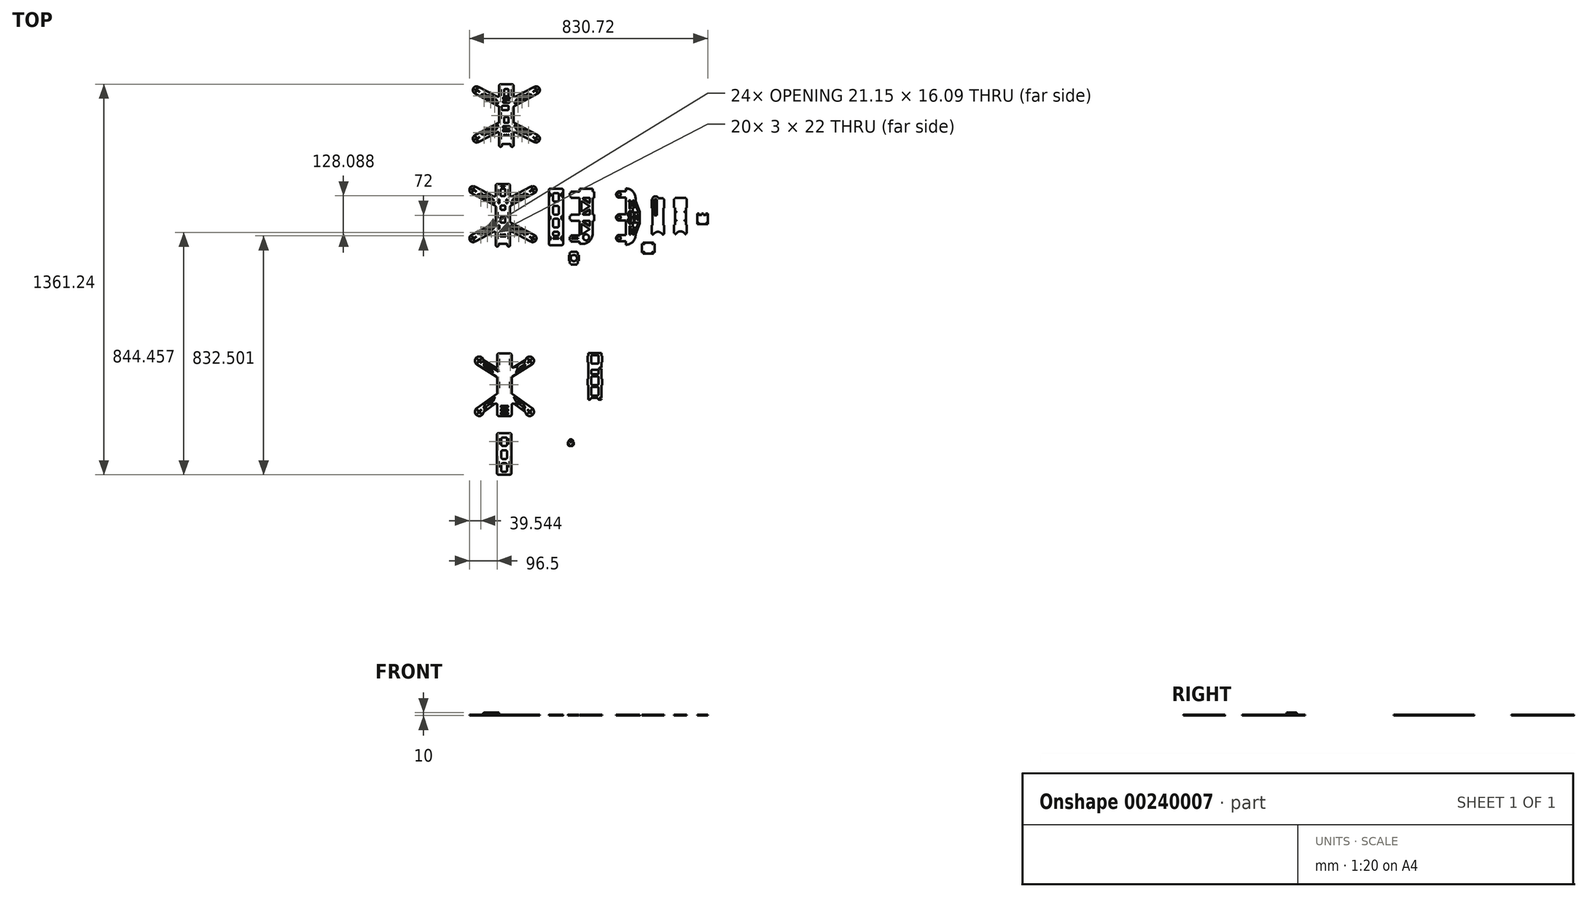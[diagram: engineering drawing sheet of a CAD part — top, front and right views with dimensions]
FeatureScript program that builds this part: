
annotation { "Feature Type Name" : "Feature", "Feature Type Description" : "" }
export const myFeature = defineFeature(function(context is Context, id is Id, definition is map)
    precondition{}
    {
        {
            var Q0;
            Q0=qCreatedBy(makeId("Top.planeOp"),FACE);
            var sketch = newSketch(context, id + "F0", { "sketchPlane" : qUnion([Q0])});
            skLineSegment(sketch, "E0", {"start": v(68.26, -102.02) * mm, "end": v(64.85, -102.02) * mm});
            skCircle(sketch, "E1", {"center": v(68.26, 75.53) * mm, "radius": 3.4 * mm});
            skCircle(sketch, "E2", {"center": v(62.63, 69.85) * mm, "radius": 1.3 * mm});
            skCircle(sketch, "E3", {"center": v(73.9, 81.2) * mm, "radius": 1.3 * mm});
            skCircle(sketch, "E4", {"center": v(61.51, 82.22) * mm, "radius": 1.3 * mm});
            skCircle(sketch, "E5", {"center": v(75, 68.84) * mm, "radius": 1.3 * mm});
            skCircle(sketch, "E6.MirrorC", {"center": v(-101, 82.22) * mm, "radius": 1.3 * mm});
            skCircle(sketch, "E7.MirrorC", {"center": v(-113.37, 81.2) * mm, "radius": 1.3 * mm});
            skCircle(sketch, "E8.MirrorC", {"center": v(-102.1, 69.85) * mm, "radius": 1.3 * mm});
            skCircle(sketch, "E9.MirrorC", {"center": v(-114.49, 68.84) * mm, "radius": 1.3 * mm});
            skCircle(sketch, "E10.MirrorC", {"center": v(-107.74, 75.53) * mm, "radius": 3.4 * mm});
            skArc(sketch, "E11", {"start": v(-93.48, 80.2) * mm, "mid": v(-116.97, 87.35) * mm, "end": v(-115.73, 62.83) * mm});
            skArc(sketch, "E12.MirrorC", {"start": v(-93.03, -104.95) * mm, "mid": v(-117.1, -113.75) * mm, "end": v(-113.86, -88.33) * mm});
            skCircle(sketch, "E13.MirrorC", {"center": v(-107.74, -102.02) * mm, "radius": 3.4 * mm});
            skCircle(sketch, "E14.MirrorC", {"center": v(-102.1, -96.34) * mm, "radius": 1.3 * mm});
            skCircle(sketch, "E15.MirrorC", {"center": v(-101, -108.7) * mm, "radius": 1.3 * mm});
            skCircle(sketch, "E16.MirrorC", {"center": v(-113.37, -107.7) * mm, "radius": 1.3 * mm});
            skCircle(sketch, "E17.MirrorC", {"center": v(-114.49, -95.33) * mm, "radius": 1.3 * mm});
            skLineSegment(sketch, "E18", {"start": v(-19.74, 100.98) * mm, "end": v(-44.74, 100.98) * mm});
            skLineSegment(sketch, "E19.bottom", {"start": v(-39.74, 100.98) * mm, "end": v(0.26, 100.98) * mm});
            skLineSegment(sketch, "E19.top", {"start": v(-39.74, -117.02) * mm, "end": v(0.26, -117.02) * mm});
            skLineSegment(sketch, "E19.left", {"start": v(-44.74, 95.98) * mm, "end": v(-44.74, 57.2) * mm});
            skLineSegment(sketch, "E19.right", {"start": v(5.26, 95.98) * mm, "end": v(5.26, 57.2) * mm});
            skArc(sketch, "E20.MirrorC", {"start": v(53.55, -104.95) * mm, "mid": v(77.62, -113.75) * mm, "end": v(74.38, -88.33) * mm});
            skCircle(sketch, "E21.MirrorC", {"center": v(62.63, -96.34) * mm, "radius": 1.3 * mm});
            skCircle(sketch, "E22.MirrorC", {"center": v(75, -95.33) * mm, "radius": 1.3 * mm});
            skCircle(sketch, "E23.MirrorC", {"center": v(73.9, -107.7) * mm, "radius": 1.3 * mm});
            skCircle(sketch, "E24.MirrorC", {"center": v(61.51, -108.7) * mm, "radius": 1.3 * mm});
            skArc(sketch, "E25.MirrorC", {"start": v(54, 80.2) * mm, "mid": v(77.49, 87.35) * mm, "end": v(76.25, 62.83) * mm});
            skCircle(sketch, "E26.MirrorC", {"center": v(68.26, -102.02) * mm, "radius": 3.4 * mm});
            skLineSegment(sketch, "E27", {"start": v(-52.67, -74.18) * mm, "end": v(-91.05, -101.87) * mm});
            skLineSegment(sketch, "E28", {"start": v(-46.81, -39.96) * mm, "end": v(-113.86, -88.33) * mm});
            skLineSegment(sketch, "E29", {"start": v(-47.08, 19.62) * mm, "end": v(-115.73, 62.83) * mm});
            skLineSegment(sketch, "E30", {"start": v(-52.4, 52.98) * mm, "end": v(-91.4, 77.52) * mm});
            skLineSegment(sketch, "E31.MirrorCS", {"start": v(13.19, -74.18) * mm, "end": v(51.57, -101.87) * mm});
            skLineSegment(sketch, "E32.MirrorCS", {"start": v(7.33, -39.96) * mm, "end": v(74.38, -88.33) * mm});
            skLineSegment(sketch, "E33.MirrorCS", {"start": v(7.6, 19.62) * mm, "end": v(76.25, 62.83) * mm});
            skLineSegment(sketch, "E34.MirrorCS", {"start": v(12.92, 52.98) * mm, "end": v(51.92, 77.52) * mm});
            skLineSegment(sketch, "E35.trimOffspring", {"start": v(-44.74, -78.24) * mm, "end": v(-44.74, -112.02) * mm});
            skLineSegment(sketch, "E36.trimOffspring", {"start": v(5.26, -78.24) * mm, "end": v(5.26, -112.02) * mm});
            skLineSegment(sketch, "E37.trimOffspring", {"start": v(5.26, 15.4) * mm, "end": v(5.26, -35.9) * mm});
            skLineSegment(sketch, "E38.trimOffspring", {"start": v(-44.74, 15.4) * mm, "end": v(-44.74, -35.9) * mm});
            skLineSegment(sketch, "E39.trimOffspring", {"start": v(68.26, -98.62) * mm, "end": v(68.26, -102.02) * mm});
            skPoint(sketch, "E40.visualSharp", {"position": v(-44.74, 100.98) * mm});
            skArc(sketch, "E40.filletArc", {"start": v(-39.74, 100.98) * mm, "mid": v(-43.28, 99.51) * mm, "end": v(-44.74, 95.98) * mm});
            skPoint(sketch, "E41.visualSharp", {"position": v(5.26, 100.98) * mm});
            skArc(sketch, "E41.filletArc", {"start": v(5.26, 95.98) * mm, "mid": v(3.8, 99.51) * mm, "end": v(0.26, 100.98) * mm});
            skPoint(sketch, "E42.visualSharp", {"position": v(5.26, -117.02) * mm});
            skArc(sketch, "E42.filletArc", {"start": v(0.26, -117.02) * mm, "mid": v(3.8, -115.56) * mm, "end": v(5.26, -112.02) * mm});
            skPoint(sketch, "E43.visualSharp", {"position": v(-44.74, -117.02) * mm});
            skArc(sketch, "E43.filletArc", {"start": v(-44.74, -112.02) * mm, "mid": v(-43.28, -115.56) * mm, "end": v(-39.74, -117.02) * mm});
            skPoint(sketch, "E44.visualSharp", {"position": v(5.26, 18.15) * mm});
            skArc(sketch, "E44.filletArc", {"start": v(7.6, 19.62) * mm, "mid": v(5.88, 17.8) * mm, "end": v(5.26, 15.4) * mm});
            skPoint(sketch, "E45.visualSharp", {"position": v(-44.74, 18.15) * mm});
            skArc(sketch, "E45.filletArc", {"start": v(-44.74, 15.4) * mm, "mid": v(-45.36, 17.8) * mm, "end": v(-47.08, 19.62) * mm});
            skPoint(sketch, "E46.visualSharp", {"position": v(-44.74, -38.47) * mm});
            skArc(sketch, "E46.filletArc", {"start": v(-46.81, -39.96) * mm, "mid": v(-45.29, -38.19) * mm, "end": v(-44.74, -35.9) * mm});
            skPoint(sketch, "E47.visualSharp", {"position": v(5.26, -38.47) * mm});
            skArc(sketch, "E47.filletArc", {"start": v(5.26, -35.9) * mm, "mid": v(5.8, -38.19) * mm, "end": v(7.33, -39.96) * mm});
            skPoint(sketch, "E48.visualSharp", {"position": v(5.26, -68.47) * mm});
            skArc(sketch, "E48.filletArc", {"start": v(13.19, -74.18) * mm, "mid": v(7.98, -73.79) * mm, "end": v(5.26, -78.24) * mm});
            skPoint(sketch, "E49.visualSharp", {"position": v(-44.74, -68.47) * mm});
            skArc(sketch, "E49.filletArc", {"start": v(-44.74, -78.24) * mm, "mid": v(-47.46, -73.79) * mm, "end": v(-52.67, -74.18) * mm});
            skPoint(sketch, "E50.visualSharp", {"position": v(-44.74, 48.15) * mm});
            skArc(sketch, "E50.filletArc", {"start": v(-52.4, 52.98) * mm, "mid": v(-47.32, 52.83) * mm, "end": v(-44.74, 57.2) * mm});
            skPoint(sketch, "E51.visualSharp", {"position": v(5.26, 48.15) * mm});
            skArc(sketch, "E51.filletArc", {"start": v(5.26, 57.2) * mm, "mid": v(7.84, 52.83) * mm, "end": v(12.92, 52.98) * mm});
            skPoint(sketch, "E52.visualSharp", {"position": v(-93.05, 78.56) * mm});
            skArc(sketch, "E52.filletArc", {"start": v(-93.48, 80.2) * mm, "mid": v(-92.67, 78.67) * mm, "end": v(-91.4, 77.52) * mm});
            skPoint(sketch, "E53.visualSharp", {"position": v(53.57, 78.56) * mm});
            skArc(sketch, "E53.filletArc", {"start": v(51.92, 77.52) * mm, "mid": v(53.2, 78.67) * mm, "end": v(54, 80.2) * mm});
            skPoint(sketch, "E54.visualSharp", {"position": v(53.3, -103.12) * mm});
            skArc(sketch, "E54.filletArc", {"start": v(53.55, -104.95) * mm, "mid": v(52.85, -103.22) * mm, "end": v(51.57, -101.87) * mm});
            skPoint(sketch, "E55.visualSharp", {"position": v(-92.78, -103.12) * mm});
            skArc(sketch, "E55.filletArc", {"start": v(-91.05, -101.87) * mm, "mid": v(-92.33, -103.22) * mm, "end": v(-93.03, -104.95) * mm});
            skLineSegment(sketch, "E56", {"start": v(-19.74, 100.98) * mm, "end": v(-19.74, -117.02) * mm, "construction": true});
            skLineSegment(sketch, "E57", {"start": v(-41.74, 82.98) * mm, "end": v(-41.74, 60.98) * mm});
            skLineSegment(sketch, "E58", {"start": v(-41.74, 60.98) * mm, "end": v(-38.74, 60.98) * mm});
            skLineSegment(sketch, "E59", {"start": v(-38.74, 60.98) * mm, "end": v(-38.74, 82.98) * mm});
            skLineSegment(sketch, "E60", {"start": v(-38.74, 82.98) * mm, "end": v(-41.74, 82.98) * mm});
            skLineSegment(sketch, "E61", {"start": v(-41.74, 2.98) * mm, "end": v(-41.74, -19.02) * mm});
            skLineSegment(sketch, "E62", {"start": v(-41.74, -19.02) * mm, "end": v(-38.74, -19.02) * mm});
            skLineSegment(sketch, "E63", {"start": v(-38.74, -19.02) * mm, "end": v(-38.74, 2.98) * mm});
            skLineSegment(sketch, "E64", {"start": v(-38.74, 2.98) * mm, "end": v(-41.74, 2.98) * mm});
            skLineSegment(sketch, "E65.MirrorCS", {"start": v(-0.74, 60.98) * mm, "end": v(-0.74, 82.98) * mm});
            skLineSegment(sketch, "E66.MirrorCS", {"start": v(2.26, 60.98) * mm, "end": v(-0.74, 60.98) * mm});
            skLineSegment(sketch, "E67.MirrorCS", {"start": v(2.26, 82.98) * mm, "end": v(2.26, 60.98) * mm});
            skLineSegment(sketch, "E68.MirrorCS", {"start": v(-0.74, 82.98) * mm, "end": v(2.26, 82.98) * mm});
            skLineSegment(sketch, "E69.MirrorCS", {"start": v(-0.74, 2.98) * mm, "end": v(2.26, 2.98) * mm});
            skLineSegment(sketch, "E70.MirrorCS", {"start": v(2.26, 2.98) * mm, "end": v(2.26, -19.02) * mm});
            skLineSegment(sketch, "E71.MirrorCS", {"start": v(-0.74, -19.02) * mm, "end": v(-0.74, 2.98) * mm});
            skLineSegment(sketch, "E72.MirrorCS", {"start": v(2.26, -19.02) * mm, "end": v(-0.74, -19.02) * mm});
            skLineSegment(sketch, "E73.bottom", {"start": v(-9.74, -80.94) * mm, "end": v(-29.74, -80.94) * mm});
            skLineSegment(sketch, "E73.top", {"start": v(-9.74, -86.94) * mm, "end": v(-29.74, -86.94) * mm});
            skLineSegment(sketch, "E73.left", {"start": v(-6.74, -83.94) * mm, "end": v(-6.74, -83.94) * mm});
            skLineSegment(sketch, "E73.right", {"start": v(-32.74, -83.94) * mm, "end": v(-32.74, -83.94) * mm});
            skPoint(sketch, "E74.visualSharp", {"position": v(-32.74, -80.94) * mm});
            skArc(sketch, "E74.filletArc", {"start": v(-29.74, -80.94) * mm, "mid": v(-31.86, -81.81) * mm, "end": v(-32.74, -83.94) * mm});
            skPoint(sketch, "E75.visualSharp", {"position": v(-32.74, -86.94) * mm});
            skArc(sketch, "E75.filletArc", {"start": v(-32.74, -83.94) * mm, "mid": v(-31.86, -86.06) * mm, "end": v(-29.74, -86.94) * mm});
            skPoint(sketch, "E76.visualSharp", {"position": v(-6.74, -80.94) * mm});
            skArc(sketch, "E76.filletArc", {"start": v(-6.74, -83.94) * mm, "mid": v(-7.62, -81.81) * mm, "end": v(-9.74, -80.94) * mm});
            skPoint(sketch, "E77.visualSharp", {"position": v(-6.74, -86.94) * mm});
            skArc(sketch, "E77.filletArc", {"start": v(-9.74, -86.94) * mm, "mid": v(-7.62, -86.06) * mm, "end": v(-6.74, -83.94) * mm});
            skLineSegment(sketch, "E78.bottom", {"start": v(-9.74, -92.94) * mm, "end": v(-29.74, -92.94) * mm});
            skLineSegment(sketch, "E78.top", {"start": v(-9.74, -98.94) * mm, "end": v(-29.74, -98.94) * mm});
            skLineSegment(sketch, "E78.left", {"start": v(-6.74, -95.94) * mm, "end": v(-6.74, -95.94) * mm});
            skLineSegment(sketch, "E78.right", {"start": v(-32.74, -95.94) * mm, "end": v(-32.74, -95.94) * mm});
            skPoint(sketch, "E79.visualSharp", {"position": v(-32.74, -92.94) * mm});
            skArc(sketch, "E79.filletArc", {"start": v(-29.74, -92.94) * mm, "mid": v(-31.86, -93.81) * mm, "end": v(-32.74, -95.94) * mm});
            skPoint(sketch, "E80.visualSharp", {"position": v(-32.74, -98.94) * mm});
            skArc(sketch, "E80.filletArc", {"start": v(-32.74, -95.94) * mm, "mid": v(-31.86, -98.06) * mm, "end": v(-29.74, -98.94) * mm});
            skPoint(sketch, "E81.visualSharp", {"position": v(-6.74, -92.94) * mm});
            skArc(sketch, "E81.filletArc", {"start": v(-6.74, -95.94) * mm, "mid": v(-7.62, -93.81) * mm, "end": v(-9.74, -92.94) * mm});
            skPoint(sketch, "E82.visualSharp", {"position": v(-6.74, -98.94) * mm});
            skArc(sketch, "E82.filletArc", {"start": v(-9.74, -98.94) * mm, "mid": v(-7.62, -98.06) * mm, "end": v(-6.74, -95.94) * mm});
            skLineSegment(sketch, "E83.bottom", {"start": v(-9.74, -104.94) * mm, "end": v(-29.74, -104.94) * mm});
            skLineSegment(sketch, "E83.top", {"start": v(-9.74, -110.94) * mm, "end": v(-29.74, -110.94) * mm});
            skLineSegment(sketch, "E83.left", {"start": v(-6.74, -107.94) * mm, "end": v(-6.74, -107.94) * mm});
            skLineSegment(sketch, "E83.right", {"start": v(-32.74, -107.94) * mm, "end": v(-32.74, -107.94) * mm});
            skPoint(sketch, "E84.visualSharp", {"position": v(-32.74, -104.94) * mm});
            skArc(sketch, "E84.filletArc", {"start": v(-29.74, -104.94) * mm, "mid": v(-31.86, -105.81) * mm, "end": v(-32.74, -107.94) * mm});
            skPoint(sketch, "E85.visualSharp", {"position": v(-32.74, -110.94) * mm});
            skArc(sketch, "E85.filletArc", {"start": v(-32.74, -107.94) * mm, "mid": v(-31.86, -110.06) * mm, "end": v(-29.74, -110.94) * mm});
            skPoint(sketch, "E86.visualSharp", {"position": v(-6.74, -104.94) * mm});
            skArc(sketch, "E86.filletArc", {"start": v(-6.74, -107.94) * mm, "mid": v(-7.62, -105.81) * mm, "end": v(-9.74, -104.94) * mm});
            skPoint(sketch, "E87.visualSharp", {"position": v(-6.74, -110.94) * mm});
            skArc(sketch, "E87.filletArc", {"start": v(-9.74, -110.94) * mm, "mid": v(-7.62, -110.06) * mm, "end": v(-6.74, -107.94) * mm});
            skLineSegment(sketch, "E88", {"start": v(-54.79, -50.65) * mm, "end": v(-75.87, -65.86) * mm});
            skLineSegment(sketch, "E89", {"start": v(-75.2, -67.67) * mm, "end": v(-61.28, -66.51) * mm});
            skLineSegment(sketch, "E90", {"start": v(-53.28, -51.85) * mm, "end": v(-58.77, -64.7) * mm});
            skPoint(sketch, "E91.visualSharp", {"position": v(-78.8, -67.96) * mm});
            skArc(sketch, "E91.filletArc", {"start": v(-75.87, -65.86) * mm, "mid": v(-76.23, -67.02) * mm, "end": v(-75.2, -67.67) * mm});
            skPoint(sketch, "E92.visualSharp", {"position": v(-51.87, -48.54) * mm});
            skArc(sketch, "E92.filletArc", {"start": v(-53.28, -51.85) * mm, "mid": v(-53.58, -50.68) * mm, "end": v(-54.79, -50.65) * mm});
            skPoint(sketch, "E93.visualSharp", {"position": v(-59.48, -66.36) * mm});
            skArc(sketch, "E93.filletArc", {"start": v(-61.28, -66.51) * mm, "mid": v(-59.78, -65.96) * mm, "end": v(-58.77, -64.7) * mm});
            skLineSegment(sketch, "E94", {"start": v(-69.16, -73.35) * mm, "end": v(-90.25, -88.56) * mm});
            skLineSegment(sketch, "E95", {"start": v(-91.75, -87.35) * mm, "end": v(-86.26, -74.5) * mm});
            skLineSegment(sketch, "E96", {"start": v(-83.75, -72.7) * mm, "end": v(-69.83, -71.54) * mm});
            skPoint(sketch, "E97.visualSharp", {"position": v(-93.17, -90.66) * mm});
            skArc(sketch, "E97.filletArc", {"start": v(-91.75, -87.35) * mm, "mid": v(-91.46, -88.53) * mm, "end": v(-90.25, -88.56) * mm});
            skPoint(sketch, "E98.visualSharp", {"position": v(-66.24, -71.24) * mm});
            skArc(sketch, "E98.filletArc", {"start": v(-69.16, -73.35) * mm, "mid": v(-68.8, -72.19) * mm, "end": v(-69.83, -71.54) * mm});
            skPoint(sketch, "E99.visualSharp", {"position": v(-85.56, -72.84) * mm});
            skArc(sketch, "E99.filletArc", {"start": v(-83.75, -72.7) * mm, "mid": v(-85.26, -73.25) * mm, "end": v(-86.26, -74.5) * mm});
            skLineSegment(sketch, "E100.MirrorCS", {"start": v(35.73, -67.67) * mm, "end": v(21.8, -66.51) * mm});
            skLineSegment(sketch, "E101.MirrorCS", {"start": v(29.68, -73.35) * mm, "end": v(50.77, -88.56) * mm});
            skLineSegment(sketch, "E102.MirrorCS", {"start": v(44.27, -72.7) * mm, "end": v(30.35, -71.54) * mm});
            skArc(sketch, "E103.MirrorCS", {"start": v(44.27, -72.7) * mm, "mid": v(45.78, -73.25) * mm, "end": v(46.78, -74.5) * mm});
            skLineSegment(sketch, "E104.MirrorCS", {"start": v(52.27, -87.35) * mm, "end": v(46.78, -74.5) * mm});
            skArc(sketch, "E105.MirrorCS", {"start": v(52.27, -87.35) * mm, "mid": v(51.98, -88.53) * mm, "end": v(50.77, -88.56) * mm});
            skArc(sketch, "E106.MirrorCS", {"start": v(29.68, -73.35) * mm, "mid": v(29.33, -72.19) * mm, "end": v(30.35, -71.54) * mm});
            skArc(sketch, "E107.MirrorCS", {"start": v(36.4, -65.86) * mm, "mid": v(36.75, -67.02) * mm, "end": v(35.73, -67.67) * mm});
            skLineSegment(sketch, "E108.MirrorCS", {"start": v(15.3, -50.65) * mm, "end": v(36.4, -65.86) * mm});
            skLineSegment(sketch, "E109.MirrorCS", {"start": v(13.8, -51.85) * mm, "end": v(19.3, -64.7) * mm});
            skPoint(sketch, "E110.MirrorP", {"position": v(20, -66.36) * mm});
            skArc(sketch, "E111.MirrorCS", {"start": v(21.8, -66.51) * mm, "mid": v(20.3, -65.96) * mm, "end": v(19.3, -64.7) * mm});
            skArc(sketch, "E112.MirrorCS", {"start": v(13.8, -51.85) * mm, "mid": v(14.1, -50.68) * mm, "end": v(15.3, -50.65) * mm});
            skLineSegment(sketch, "E113", {"start": v(-62.1, 33.8) * mm, "end": v(-79.13, 44.52) * mm});
            skLineSegment(sketch, "E114", {"start": v(-64.5, 45.46) * mm, "end": v(-60.63, 35) * mm});
            skLineSegment(sketch, "E115", {"start": v(-67.59, 47.41) * mm, "end": v(-78.7, 46.37) * mm});
            skLineSegment(sketch, "E116", {"start": v(-85.3, 50.07) * mm, "end": v(-74.2, 51.11) * mm});
            skPoint(sketch, "E117.visualSharp", {"position": v(-81.62, 46.1) * mm});
            skArc(sketch, "E117.filletArc", {"start": v(-78.7, 46.37) * mm, "mid": v(-79.57, 45.6) * mm, "end": v(-79.13, 44.52) * mm});
            skPoint(sketch, "E118.visualSharp", {"position": v(-59.62, 32.24) * mm});
            skArc(sketch, "E118.filletArc", {"start": v(-62.1, 33.8) * mm, "mid": v(-60.94, 33.88) * mm, "end": v(-60.63, 35) * mm});
            skLineSegment(sketch, "E119", {"start": v(-73.75, 52.95) * mm, "end": v(-90.78, 63.67) * mm});
            skLineSegment(sketch, "E120", {"start": v(-92.25, 62.48) * mm, "end": v(-88.4, 52.01) * mm});
            skPoint(sketch, "E121.visualSharp", {"position": v(-93.27, 65.24) * mm});
            skArc(sketch, "E121.filletArc", {"start": v(-90.78, 63.67) * mm, "mid": v(-91.94, 63.6) * mm, "end": v(-92.25, 62.48) * mm});
            skPoint(sketch, "E122.newPointA", {"position": v(-71.26, 51.39) * mm});
            skArc(sketch, "E122.filletArc", {"start": v(-74.2, 51.11) * mm, "mid": v(-73.31, 51.88) * mm, "end": v(-73.75, 52.95) * mm});
            skPoint(sketch, "E123.visualSharp", {"position": v(-87.6, 49.85) * mm});
            skArc(sketch, "E123.filletArc", {"start": v(-88.4, 52.01) * mm, "mid": v(-87.17, 50.51) * mm, "end": v(-85.3, 50.07) * mm});
            skPoint(sketch, "E124.visualSharp", {"position": v(-65.3, 47.63) * mm});
            skArc(sketch, "E124.filletArc", {"start": v(-64.5, 45.46) * mm, "mid": v(-65.7, 46.96) * mm, "end": v(-67.59, 47.41) * mm});
            skLineSegment(sketch, "E125.MirrorCS", {"start": v(25.01, 45.46) * mm, "end": v(21.15, 35) * mm});
            skLineSegment(sketch, "E126.MirrorCS", {"start": v(22.62, 33.8) * mm, "end": v(39.65, 44.52) * mm});
            skArc(sketch, "E127.MirrorCS", {"start": v(22.62, 33.8) * mm, "mid": v(21.46, 33.88) * mm, "end": v(21.15, 35) * mm});
            skLineSegment(sketch, "E128.MirrorCS", {"start": v(28.1, 47.41) * mm, "end": v(39.21, 46.37) * mm});
            skArc(sketch, "E129.MirrorCS", {"start": v(39.21, 46.37) * mm, "mid": v(40.1, 45.6) * mm, "end": v(39.65, 44.52) * mm});
            skLineSegment(sketch, "E130.MirrorCS", {"start": v(45.81, 50.07) * mm, "end": v(34.71, 51.11) * mm});
            skLineSegment(sketch, "E131.MirrorCS", {"start": v(34.27, 52.95) * mm, "end": v(51.3, 63.67) * mm});
            skArc(sketch, "E132.MirrorCS", {"start": v(34.71, 51.11) * mm, "mid": v(33.83, 51.88) * mm, "end": v(34.27, 52.95) * mm});
            skArc(sketch, "E133.MirrorCS", {"start": v(48.91, 52.01) * mm, "mid": v(47.7, 50.51) * mm, "end": v(45.81, 50.07) * mm});
            skLineSegment(sketch, "E134.MirrorCS", {"start": v(52.77, 62.48) * mm, "end": v(48.91, 52.01) * mm});
            skArc(sketch, "E135.MirrorCS", {"start": v(51.3, 63.67) * mm, "mid": v(52.46, 63.6) * mm, "end": v(52.77, 62.48) * mm});
            skArc(sketch, "E136.MirrorCS", {"start": v(25.01, 45.46) * mm, "mid": v(26.23, 46.96) * mm, "end": v(28.1, 47.41) * mm});
            skLineSegment(sketch, "E137", {"start": v(-20.69, -176.43) * mm, "end": v(-45.69, -176.43) * mm});
            skLineSegment(sketch, "E138.bottom", {"start": v(-40.69, -176.43) * mm, "end": v(-0.69, -176.43) * mm});
            skPoint(sketch, "E139.visualSharp", {"position": v(-45.69, -176.43) * mm});
            skArc(sketch, "E139.filletArc", {"start": v(-40.69, -176.43) * mm, "mid": v(-44.22, -177.9) * mm, "end": v(-45.69, -181.44) * mm});
            skPoint(sketch, "E140.visualSharp", {"position": v(4.31, -176.43) * mm});
            skArc(sketch, "E140.filletArc", {"start": v(4.31, -181.44) * mm, "mid": v(2.85, -177.9) * mm, "end": v(-0.69, -176.43) * mm});
            skLineSegment(sketch, "E141", {"start": v(-42.69, -194.43) * mm, "end": v(-42.69, -216.43) * mm});
            skLineSegment(sketch, "E142", {"start": v(-42.69, -216.43) * mm, "end": v(-39.69, -216.43) * mm});
            skLineSegment(sketch, "E143", {"start": v(-39.69, -216.43) * mm, "end": v(-39.69, -194.43) * mm});
            skLineSegment(sketch, "E144", {"start": v(-39.69, -194.43) * mm, "end": v(-42.69, -194.43) * mm});
            skLineSegment(sketch, "E145", {"start": v(-42.69, -274.43) * mm, "end": v(-42.69, -296.43) * mm});
            skLineSegment(sketch, "E146", {"start": v(-42.69, -296.43) * mm, "end": v(-39.69, -296.43) * mm});
            skLineSegment(sketch, "E147", {"start": v(-39.69, -296.43) * mm, "end": v(-39.69, -274.43) * mm});
            skLineSegment(sketch, "E148", {"start": v(-39.69, -274.43) * mm, "end": v(-42.69, -274.43) * mm});
            skLineSegment(sketch, "E149", {"start": v(-45.69, -181.44) * mm, "end": v(-45.69, -316.44) * mm});
            skLineSegment(sketch, "E150", {"start": v(4.31, -181.44) * mm, "end": v(4.31, -316.44) * mm});
            skLineSegment(sketch, "E151", {"start": v(-40.69, -321.44) * mm, "end": v(-0.69, -321.44) * mm});
            skPoint(sketch, "E152.visualSharp", {"position": v(-45.69, -321.44) * mm});
            skArc(sketch, "E152.filletArc", {"start": v(-45.69, -316.44) * mm, "mid": v(-44.22, -319.97) * mm, "end": v(-40.69, -321.44) * mm});
            skPoint(sketch, "E153.visualSharp", {"position": v(4.31, -321.44) * mm});
            skArc(sketch, "E153.filletArc", {"start": v(-0.69, -321.44) * mm, "mid": v(2.85, -319.97) * mm, "end": v(4.31, -316.44) * mm});
            skPoint(sketch, "E154.endSnap0", {"position": v(-20.69, -321.44) * mm});
            skLineSegment(sketch, "E155.MirrorCS", {"start": v(-1.69, -216.43) * mm, "end": v(-1.69, -194.43) * mm});
            skLineSegment(sketch, "E156.MirrorCS", {"start": v(1.31, -194.43) * mm, "end": v(1.31, -216.43) * mm});
            skLineSegment(sketch, "E157.MirrorCS", {"start": v(1.31, -216.43) * mm, "end": v(-1.69, -216.43) * mm});
            skLineSegment(sketch, "E158.MirrorCS", {"start": v(-1.69, -194.43) * mm, "end": v(1.31, -194.43) * mm});
            skLineSegment(sketch, "E159.MirrorCS", {"start": v(-1.69, -296.43) * mm, "end": v(-1.69, -274.43) * mm});
            skLineSegment(sketch, "E160.MirrorCS", {"start": v(1.31, -296.43) * mm, "end": v(-1.69, -296.43) * mm});
            skLineSegment(sketch, "E161.MirrorCS", {"start": v(1.31, -274.43) * mm, "end": v(1.31, -296.43) * mm});
            skLineSegment(sketch, "E162.MirrorCS", {"start": v(-1.69, -274.43) * mm, "end": v(1.31, -274.43) * mm});
            skLineSegment(sketch, "E163.bottom", {"start": v(-15.69, -191.43) * mm, "end": v(-25.69, -191.43) * mm});
            skLineSegment(sketch, "E163.top", {"start": v(-15.69, -221.43) * mm, "end": v(-25.69, -221.43) * mm});
            skLineSegment(sketch, "E163.left", {"start": v(-10.69, -196.43) * mm, "end": v(-10.69, -216.43) * mm});
            skLineSegment(sketch, "E163.right", {"start": v(-30.69, -196.43) * mm, "end": v(-30.69, -216.43) * mm});
            skLineSegment(sketch, "E164.bottom", {"start": v(-15.69, -236.43) * mm, "end": v(-25.69, -236.43) * mm});
            skLineSegment(sketch, "E164.top", {"start": v(-15.69, -266.43) * mm, "end": v(-25.69, -266.43) * mm});
            skLineSegment(sketch, "E164.left", {"start": v(-10.69, -241.43) * mm, "end": v(-10.69, -261.43) * mm});
            skLineSegment(sketch, "E164.right", {"start": v(-30.69, -241.43) * mm, "end": v(-30.69, -261.43) * mm});
            skLineSegment(sketch, "E165.bottom", {"start": v(-15.69, -281.43) * mm, "end": v(-25.69, -281.43) * mm});
            skLineSegment(sketch, "E165.top", {"start": v(-15.69, -311.43) * mm, "end": v(-25.69, -311.43) * mm});
            skLineSegment(sketch, "E165.left", {"start": v(-10.69, -286.43) * mm, "end": v(-10.69, -306.43) * mm});
            skLineSegment(sketch, "E165.right", {"start": v(-30.69, -286.43) * mm, "end": v(-30.69, -306.43) * mm});
            skPoint(sketch, "E166.visualSharp", {"position": v(-30.69, -191.43) * mm});
            skArc(sketch, "E166.filletArc", {"start": v(-25.69, -191.43) * mm, "mid": v(-29.22, -192.9) * mm, "end": v(-30.69, -196.43) * mm});
            skPoint(sketch, "E167.visualSharp", {"position": v(-10.69, -191.43) * mm});
            skArc(sketch, "E167.filletArc", {"start": v(-10.69, -196.43) * mm, "mid": v(-12.15, -192.9) * mm, "end": v(-15.69, -191.43) * mm});
            skPoint(sketch, "E168.visualSharp", {"position": v(-10.69, -221.43) * mm});
            skArc(sketch, "E168.filletArc", {"start": v(-15.69, -221.43) * mm, "mid": v(-12.15, -219.97) * mm, "end": v(-10.69, -216.43) * mm});
            skPoint(sketch, "E169.visualSharp", {"position": v(-30.69, -221.43) * mm});
            skArc(sketch, "E169.filletArc", {"start": v(-30.69, -216.43) * mm, "mid": v(-29.22, -219.97) * mm, "end": v(-25.69, -221.43) * mm});
            skPoint(sketch, "E170.visualSharp", {"position": v(-10.69, -236.43) * mm});
            skArc(sketch, "E170.filletArc", {"start": v(-10.69, -241.43) * mm, "mid": v(-12.15, -237.9) * mm, "end": v(-15.69, -236.43) * mm});
            skPoint(sketch, "E171.visualSharp", {"position": v(-30.69, -236.43) * mm});
            skArc(sketch, "E171.filletArc", {"start": v(-25.69, -236.43) * mm, "mid": v(-29.22, -237.9) * mm, "end": v(-30.69, -241.43) * mm});
            skPoint(sketch, "E172.visualSharp", {"position": v(-30.69, -266.43) * mm});
            skArc(sketch, "E172.filletArc", {"start": v(-30.69, -261.43) * mm, "mid": v(-29.22, -264.97) * mm, "end": v(-25.69, -266.43) * mm});
            skPoint(sketch, "E173.visualSharp", {"position": v(-10.69, -266.43) * mm});
            skArc(sketch, "E173.filletArc", {"start": v(-15.69, -266.43) * mm, "mid": v(-12.15, -264.97) * mm, "end": v(-10.69, -261.43) * mm});
            skPoint(sketch, "E174.visualSharp", {"position": v(-10.69, -281.43) * mm});
            skArc(sketch, "E174.filletArc", {"start": v(-10.69, -286.43) * mm, "mid": v(-12.15, -282.9) * mm, "end": v(-15.69, -281.43) * mm});
            skPoint(sketch, "E175.visualSharp", {"position": v(-30.69, -281.43) * mm});
            skArc(sketch, "E175.filletArc", {"start": v(-25.69, -281.43) * mm, "mid": v(-29.22, -282.9) * mm, "end": v(-30.69, -286.43) * mm});
            skPoint(sketch, "E176.visualSharp", {"position": v(-10.69, -311.43) * mm});
            skArc(sketch, "E176.filletArc", {"start": v(-15.69, -311.43) * mm, "mid": v(-12.15, -309.97) * mm, "end": v(-10.69, -306.43) * mm});
            skPoint(sketch, "E177.visualSharp", {"position": v(-30.69, -311.43) * mm});
            skArc(sketch, "E177.filletArc", {"start": v(-30.69, -306.43) * mm, "mid": v(-29.22, -309.97) * mm, "end": v(-25.69, -311.43) * mm});
            skCircle(sketch, "E178", {"center": v(-107.74, 75.53) * mm, "radius": 44.45 * mm, "construction": true});
            skCircle(sketch, "E179", {"center": v(-107.74, 75.53) * mm, "radius": 12.61 * mm, "construction": true});
            skLineSegment(sketch, "E180", {"start": v(-91.67, 74.15) * mm, "end": v(-84.06, 69.35) * mm});
            skLineSegment(sketch, "E181", {"start": v(-84.06, 69.35) * mm, "end": v(-85.65, 66.81) * mm});
            skLineSegment(sketch, "E182", {"start": v(-85.65, 66.81) * mm, "end": v(-93.27, 71.6) * mm});
            skLineSegment(sketch, "E183", {"start": v(-93.27, 71.6) * mm, "end": v(-91.67, 74.15) * mm});
            skLineSegment(sketch, "E184", {"start": v(-65.44, 57.63) * mm, "end": v(-57.82, 52.84) * mm});
            skLineSegment(sketch, "E185", {"start": v(-57.82, 52.84) * mm, "end": v(-59.42, 50.3) * mm});
            skLineSegment(sketch, "E186", {"start": v(-59.42, 50.3) * mm, "end": v(-67.04, 55.1) * mm});
            skLineSegment(sketch, "E187", {"start": v(-67.04, 55.1) * mm, "end": v(-65.44, 57.63) * mm});
            skLineSegment(sketch, "E188", {"start": v(-41.74, 60.98) * mm, "end": v(-41.74, 2.98) * mm, "construction": true});
            skLineSegment(sketch, "E189", {"start": v(-57.82, 52.84) * mm, "end": v(-41.74, 42.72) * mm, "construction": true});
            skLineSegment(sketch, "E190.MirrorCS", {"start": v(18.34, 52.84) * mm, "end": v(19.94, 50.3) * mm});
            skLineSegment(sketch, "E191.MirrorCS", {"start": v(19.94, 50.3) * mm, "end": v(27.55, 55.1) * mm});
            skLineSegment(sketch, "E192.MirrorCS", {"start": v(25.96, 57.63) * mm, "end": v(18.34, 52.84) * mm});
            skLineSegment(sketch, "E193.MirrorCS", {"start": v(27.55, 55.1) * mm, "end": v(25.96, 57.63) * mm});
            skLineSegment(sketch, "E194.MirrorCS", {"start": v(44.58, 69.35) * mm, "end": v(46.17, 66.81) * mm});
            skLineSegment(sketch, "E195.MirrorCS", {"start": v(52.2, 74.15) * mm, "end": v(44.58, 69.35) * mm});
            skLineSegment(sketch, "E196.MirrorCS", {"start": v(46.17, 66.81) * mm, "end": v(53.8, 71.6) * mm});
            skLineSegment(sketch, "E197.MirrorCS", {"start": v(53.8, 71.6) * mm, "end": v(52.2, 74.15) * mm});
            skLineSegment(sketch, "E198", {"start": v(17.67, -73.72) * mm, "end": v(24.97, -78.98) * mm});
            skLineSegment(sketch, "E199", {"start": v(24.97, -78.98) * mm, "end": v(26.72, -76.55) * mm});
            skLineSegment(sketch, "E200", {"start": v(26.72, -76.55) * mm, "end": v(19.42, -71.29) * mm});
            skLineSegment(sketch, "E201", {"start": v(19.42, -71.29) * mm, "end": v(17.67, -73.72) * mm});
            skLineSegment(sketch, "E202", {"start": v(44.57, -89.42) * mm, "end": v(42.81, -91.86) * mm});
            skLineSegment(sketch, "E203", {"start": v(42.81, -91.86) * mm, "end": v(50.1, -97.12) * mm});
            skLineSegment(sketch, "E204", {"start": v(50.1, -97.12) * mm, "end": v(51.87, -94.69) * mm});
            skLineSegment(sketch, "E205", {"start": v(51.87, -94.69) * mm, "end": v(44.57, -89.42) * mm});
            skLineSegment(sketch, "E206", {"start": v(2.26, -19.02) * mm, "end": v(2.26, -81.3) * mm, "construction": true});
            skLineSegment(sketch, "E207", {"start": v(17.67, -73.72) * mm, "end": v(2.26, -62.6) * mm, "construction": true});
            skLineSegment(sketch, "E208.MirrorCS", {"start": v(-57.15, -73.72) * mm, "end": v(-64.45, -78.98) * mm});
            skLineSegment(sketch, "E209.MirrorCS", {"start": v(-58.9, -71.29) * mm, "end": v(-57.15, -73.72) * mm});
            skLineSegment(sketch, "E210.MirrorCS", {"start": v(-66.2, -76.55) * mm, "end": v(-58.9, -71.29) * mm});
            skLineSegment(sketch, "E211.MirrorCS", {"start": v(-64.45, -78.98) * mm, "end": v(-66.2, -76.55) * mm});
            skLineSegment(sketch, "E212.MirrorCS", {"start": v(-89.6, -97.12) * mm, "end": v(-91.35, -94.69) * mm});
            skLineSegment(sketch, "E213.MirrorCS", {"start": v(-91.35, -94.69) * mm, "end": v(-84.05, -89.42) * mm});
            skLineSegment(sketch, "E214.MirrorCS", {"start": v(-82.3, -91.86) * mm, "end": v(-89.6, -97.12) * mm});
            skLineSegment(sketch, "E215.MirrorCS", {"start": v(-84.05, -89.42) * mm, "end": v(-82.3, -91.86) * mm});
            skLineSegment(sketch, "E216", {"start": v(-89.6, -97.12) * mm, "end": v(-30.49, -54.49) * mm, "construction": true});
            skLineSegment(sketch, "E217", {"start": v(-41.74, 2.98) * mm, "end": v(-41.74, -62.6) * mm, "construction": true});
            skCircle(sketch, "E218.MirrorC", {"center": v(68.26, 75.53) * mm, "radius": 44.45 * mm, "construction": true});
            skCircle(sketch, "E219", {"center": v(-107.74, -102.02) * mm, "radius": 44.45 * mm, "construction": true});
            skCircle(sketch, "E220.MirrorC", {"center": v(68.26, -102.02) * mm, "radius": 44.45 * mm, "construction": true});
            skLineSegment(sketch, "E221.bottom", {"start": v(-45, 474.06) * mm, "end": v(-45, 474.06) * mm});
            skLineSegment(sketch, "E221.top", {"start": v(-5, 692.06) * mm, "end": v(-45, 692.06) * mm});
            skLineSegment(sketch, "E221.left", {"start": v(0, 479.06) * mm, "end": v(0, 520.76) * mm});
            skLineSegment(sketch, "E221.right", {"start": v(-50, 479.06) * mm, "end": v(-50, 520.76) * mm});
            skLineSegment(sketch, "E222", {"start": v(-25, 692.06) * mm, "end": v(-25, 474.06) * mm, "construction": true});
            skLineSegment(sketch, "E223", {"start": v(-57.34, 648.94) * mm, "end": v(-122.18, 683.22) * mm});
            skLineSegment(sketch, "E224", {"start": v(-134.94, 659.97) * mm, "end": v(-52.66, 616.47) * mm});
            skLineSegment(sketch, "E225", {"start": v(-25, 515.94) * mm, "end": v(-50, 515.94) * mm, "construction": true});
            skPoint(sketch, "E226.centerSnap0", {"position": v(-134.96, 671.69) * mm});
            skCircle(sketch, "E227", {"center": v(-125, 678.76) * mm, "radius": 1.4 * mm});
            skCircle(sketch, "E228.MirrorC", {"center": v(-132.48, 664.62) * mm, "radius": 1.4 * mm});
            skCircle(sketch, "E229", {"center": v(-128.74, 671.69) * mm, "radius": 3.4 * mm});
            skCircle(sketch, "E230", {"center": v(-120.34, 667.25) * mm, "radius": 1.4 * mm});
            skCircle(sketch, "E231.MirrorC", {"center": v(-137.14, 676.13) * mm, "radius": 1.4 * mm});
            skLineSegment(sketch, "E232", {"start": v(-50, 587.06) * mm, "end": v(0, 587.06) * mm, "construction": true});
            skPoint(sketch, "E233.newPointB", {"position": v(-50, 692.06) * mm});
            skLineSegment(sketch, "E234", {"start": v(-50, 612.05) * mm, "end": v(-50, 562.07) * mm});
            skPoint(sketch, "E235.visualSharp", {"position": v(-50, 615.06) * mm});
            skArc(sketch, "E235.filletArc", {"start": v(-50, 612.05) * mm, "mid": v(-50.72, 614.63) * mm, "end": v(-52.66, 616.47) * mm});
            skLineSegment(sketch, "E236", {"start": v(-50, 653.36) * mm, "end": v(-50, 687.06) * mm});
            skPoint(sketch, "E237.visualSharp", {"position": v(-50, 645.06) * mm});
            skArc(sketch, "E237.filletArc", {"start": v(-57.34, 648.94) * mm, "mid": v(-52.42, 649.08) * mm, "end": v(-50, 653.36) * mm});
            skLineSegment(sketch, "E238.bottom", {"start": v(-47, 674.06) * mm, "end": v(-44, 674.06) * mm});
            skLineSegment(sketch, "E238.top", {"start": v(-47, 652.06) * mm, "end": v(-44, 652.06) * mm});
            skLineSegment(sketch, "E238.left", {"start": v(-47, 674.06) * mm, "end": v(-47, 652.06) * mm});
            skLineSegment(sketch, "E238.right", {"start": v(-44, 674.06) * mm, "end": v(-44, 652.06) * mm});
            skLineSegment(sketch, "E239.bottom", {"start": v(-44, 594.06) * mm, "end": v(-47, 594.06) * mm});
            skLineSegment(sketch, "E239.top", {"start": v(-44, 572.06) * mm, "end": v(-47, 572.06) * mm});
            skLineSegment(sketch, "E239.left", {"start": v(-44, 594.06) * mm, "end": v(-44, 572.06) * mm});
            skLineSegment(sketch, "E239.right", {"start": v(-47, 594.06) * mm, "end": v(-47, 572.06) * mm});
            skArc(sketch, "E240.filletArc", {"start": v(-45, 692.06) * mm, "mid": v(-48.54, 690.6) * mm, "end": v(-50, 687.06) * mm});
            skArc(sketch, "E241.filletArc", {"start": v(-50, 479.06) * mm, "mid": v(-48.54, 475.53) * mm, "end": v(-45, 474.06) * mm});
            skArc(sketch, "E242.filletArc", {"start": v(-5, 474.06) * mm, "mid": v(-1.46, 475.53) * mm, "end": v(0, 479.06) * mm});
            skArc(sketch, "E243.filletArc", {"start": v(0, 687.06) * mm, "mid": v(-1.46, 690.6) * mm, "end": v(-5, 692.06) * mm});
            skLineSegment(sketch, "E244", {"start": v(-111.98, 652.35) * mm, "end": v(-94.81, 643.28) * mm});
            skLineSegment(sketch, "E245", {"start": v(-92, 645.75) * mm, "end": v(-96.59, 657.86) * mm});
            skLineSegment(sketch, "E246", {"start": v(-98.93, 659.1) * mm, "end": v(-111.51, 656.07) * mm});
            skLineSegment(sketch, "E247", {"start": v(-90, 651.74) * mm, "end": v(-85.41, 639.63) * mm});
            skLineSegment(sketch, "E248", {"start": v(-83.08, 638.4) * mm, "end": v(-70.5, 641.42) * mm});
            skLineSegment(sketch, "E249", {"start": v(-70.02, 645.14) * mm, "end": v(-87.19, 654.21) * mm});
            skPoint(sketch, "E250.visualSharp", {"position": v(-91.87, 656.68) * mm});
            skArc(sketch, "E250.filletArc", {"start": v(-87.19, 654.21) * mm, "mid": v(-89.45, 653.94) * mm, "end": v(-90, 651.74) * mm});
            skPoint(sketch, "E251.visualSharp", {"position": v(-84.79, 637.98) * mm});
            skArc(sketch, "E251.filletArc", {"start": v(-85.41, 639.63) * mm, "mid": v(-84.48, 638.57) * mm, "end": v(-83.08, 638.4) * mm});
            skPoint(sketch, "E252.visualSharp", {"position": v(-65.35, 642.66) * mm});
            skArc(sketch, "E252.filletArc", {"start": v(-70.5, 641.42) * mm, "mid": v(-68.97, 643.12) * mm, "end": v(-70.02, 645.14) * mm});
            skPoint(sketch, "E253.visualSharp", {"position": v(-90.14, 640.8) * mm});
            skArc(sketch, "E253.filletArc", {"start": v(-94.81, 643.28) * mm, "mid": v(-92.56, 643.55) * mm, "end": v(-92, 645.75) * mm});
            skPoint(sketch, "E254.visualSharp", {"position": v(-116.66, 654.83) * mm});
            skArc(sketch, "E254.filletArc", {"start": v(-111.51, 656.07) * mm, "mid": v(-113.03, 654.37) * mm, "end": v(-111.98, 652.35) * mm});
            skPoint(sketch, "E255.visualSharp", {"position": v(-97.21, 659.51) * mm});
            skArc(sketch, "E255.filletArc", {"start": v(-96.59, 657.86) * mm, "mid": v(-97.53, 658.92) * mm, "end": v(-98.93, 659.1) * mm});
            skLineSegment(sketch, "E256", {"start": v(-74.77, 632.68) * mm, "end": v(-57.6, 623.6) * mm});
            skLineSegment(sketch, "E257", {"start": v(-54.8, 626.08) * mm, "end": v(-59.38, 638.19) * mm});
            skLineSegment(sketch, "E258", {"start": v(-61.71, 639.42) * mm, "end": v(-74.3, 636.4) * mm});
            skPoint(sketch, "E259.visualSharp", {"position": v(-75.98, 644.4) * mm});
            skArc(sketch, "E260.filletArc", {"start": v(-57.6, 623.6) * mm, "mid": v(-55.34, 623.87) * mm, "end": v(-54.8, 626.08) * mm});
            skArc(sketch, "E261.filletArc", {"start": v(-74.3, 636.4) * mm, "mid": v(-75.82, 634.7) * mm, "end": v(-74.77, 632.68) * mm});
            skPoint(sketch, "E262.visualSharp", {"position": v(-60, 639.84) * mm});
            skArc(sketch, "E262.filletArc", {"start": v(-59.38, 638.19) * mm, "mid": v(-60.31, 639.25) * mm, "end": v(-61.71, 639.42) * mm});
            skLineSegment(sketch, "E263", {"start": v(-38, 483.94) * mm, "end": v(-12, 483.94) * mm});
            skLineSegment(sketch, "E264", {"start": v(-40, 481.94) * mm, "end": v(-40, 479.06) * mm});
            skLineSegment(sketch, "E265", {"start": v(-10, 481.94) * mm, "end": v(-10, 479.06) * mm});
            skArc(sketch, "E266.filletArc", {"start": v(-45, 474.06) * mm, "mid": v(-41.46, 475.53) * mm, "end": v(-40, 479.06) * mm});
            skLineSegment(sketch, "E267", {"start": v(-5, 474.06) * mm, "end": v(-5, 474.06) * mm});
            skPoint(sketch, "E268.visualSharp", {"position": v(-10, 474.06) * mm});
            skArc(sketch, "E268.filletArc", {"start": v(-10, 479.06) * mm, "mid": v(-8.54, 475.53) * mm, "end": v(-5, 474.06) * mm});
            skPoint(sketch, "E269.visualSharp", {"position": v(-40, 483.94) * mm});
            skArc(sketch, "E269.filletArc", {"start": v(-38, 483.94) * mm, "mid": v(-39.41, 483.36) * mm, "end": v(-40, 481.94) * mm});
            skPoint(sketch, "E270.visualSharp", {"position": v(-10, 483.94) * mm});
            skArc(sketch, "E270.filletArc", {"start": v(-10, 481.94) * mm, "mid": v(-10.59, 483.36) * mm, "end": v(-12, 483.94) * mm});
            skCircle(sketch, "E271", {"center": v(-32, 515.94) * mm, "radius": 1 * mm});
            skCircle(sketch, "E272.MirrorC", {"center": v(-18, 515.94) * mm, "radius": 1 * mm});
            skCircle(sketch, "E273", {"center": v(-25, 515.94) * mm, "radius": 1 * mm});
            skLineSegment(sketch, "E274.MirrorCS", {"start": v(-6, 594.06) * mm, "end": v(-6, 572.06) * mm});
            skLineSegment(sketch, "E275.MirrorCS", {"start": v(-6, 572.06) * mm, "end": v(-3, 572.06) * mm});
            skLineSegment(sketch, "E276.MirrorCS", {"start": v(-3, 594.06) * mm, "end": v(-3, 572.06) * mm});
            skLineSegment(sketch, "E277.MirrorCS", {"start": v(-6, 594.06) * mm, "end": v(-3, 594.06) * mm});
            skLineSegment(sketch, "E278.MirrorCS", {"start": v(-3, 652.06) * mm, "end": v(-6, 652.06) * mm});
            skLineSegment(sketch, "E279.MirrorCS", {"start": v(-3, 674.06) * mm, "end": v(-3, 652.06) * mm});
            skLineSegment(sketch, "E280.MirrorCS", {"start": v(-6, 674.06) * mm, "end": v(-6, 652.06) * mm});
            skLineSegment(sketch, "E281.MirrorCS", {"start": v(-3, 674.06) * mm, "end": v(-6, 674.06) * mm});
            skLineSegment(sketch, "E282.bottom", {"start": v(-36.71, 549.06) * mm, "end": v(-40.71, 549.06) * mm});
            skLineSegment(sketch, "E282.top", {"start": v(-36.71, 536.06) * mm, "end": v(-40.71, 536.06) * mm});
            skLineSegment(sketch, "E282.left", {"start": v(-36.71, 549.06) * mm, "end": v(-36.71, 536.06) * mm});
            skLineSegment(sketch, "E282.right", {"start": v(-40.71, 549.06) * mm, "end": v(-40.71, 536.06) * mm});
            skLineSegment(sketch, "E283.MirrorCS", {"start": v(-13.29, 549.06) * mm, "end": v(-13.29, 536.06) * mm});
            skLineSegment(sketch, "E284.MirrorCS", {"start": v(-13.29, 536.06) * mm, "end": v(-9.29, 536.06) * mm});
            skLineSegment(sketch, "E285.MirrorCS", {"start": v(-9.29, 549.06) * mm, "end": v(-9.29, 536.06) * mm});
            skLineSegment(sketch, "E286.MirrorCS", {"start": v(-13.29, 549.06) * mm, "end": v(-9.29, 549.06) * mm});
            skLineSegment(sketch, "E287.MirrorCS", {"start": v(-36.71, 625.06) * mm, "end": v(-40.71, 625.06) * mm});
            skLineSegment(sketch, "E288.MirrorCS", {"start": v(-40.71, 625.06) * mm, "end": v(-40.71, 638.06) * mm});
            skLineSegment(sketch, "E289.MirrorCS", {"start": v(-36.71, 625.06) * mm, "end": v(-36.71, 638.06) * mm});
            skLineSegment(sketch, "E290.MirrorCS", {"start": v(-36.71, 638.06) * mm, "end": v(-40.71, 638.06) * mm});
            skLineSegment(sketch, "E291.MirrorCS", {"start": v(-13.29, 625.06) * mm, "end": v(-13.29, 638.06) * mm});
            skLineSegment(sketch, "E292.MirrorCS", {"start": v(-13.29, 625.06) * mm, "end": v(-9.29, 625.06) * mm});
            skLineSegment(sketch, "E293.MirrorCS", {"start": v(-9.29, 625.06) * mm, "end": v(-9.29, 638.06) * mm});
            skLineSegment(sketch, "E294.MirrorCS", {"start": v(-13.29, 638.06) * mm, "end": v(-9.29, 638.06) * mm});
            skLineSegment(sketch, "E295.bottom", {"start": v(-32, 686.06) * mm, "end": v(-18, 686.06) * mm});
            skLineSegment(sketch, "E295.top", {"start": v(-32, 683.06) * mm, "end": v(-18, 683.06) * mm});
            skLineSegment(sketch, "E295.left", {"start": v(-32, 686.06) * mm, "end": v(-32, 683.06) * mm});
            skLineSegment(sketch, "E295.right", {"start": v(-18, 686.06) * mm, "end": v(-18, 683.06) * mm});
            skCircle(sketch, "E296", {"center": v(-128.74, 671.69) * mm, "radius": 76.2 * mm, "construction": true});
            skLineSegment(sketch, "E297", {"start": v(-128.74, 671.69) * mm, "end": v(-120.34, 667.25) * mm, "construction": true});
            skLineSegment(sketch, "E298", {"start": v(-128.74, 671.69) * mm, "end": v(-125, 678.76) * mm, "construction": true});
            skLineSegment(sketch, "E299", {"start": v(-128.74, 671.69) * mm, "end": v(-137.14, 676.13) * mm, "construction": true});
            skLineSegment(sketch, "E300", {"start": v(-128.74, 671.69) * mm, "end": v(-132.48, 664.62) * mm, "construction": true});
            skLineSegment(sketch, "E301", {"start": v(-50, 653.36) * mm, "end": v(-50, 612.05) * mm, "construction": true});
            skLineSegment(sketch, "E302", {"start": v(-103.55, 673.37) * mm, "end": v(-115.94, 649.93) * mm, "construction": true});
            skLineSegment(sketch, "E303", {"start": v(-109.75, 661.65) * mm, "end": v(-128.74, 671.69) * mm, "construction": true});
            skArc(sketch, "E304", {"start": v(-122.54, 683.41) * mm, "mid": v(-140.46, 677.89) * mm, "end": v(-134.94, 659.97) * mm});
            skLineSegment(sketch, "E305", {"start": v(-128.74, 671.69) * mm, "end": v(-122.54, 683.41) * mm});
            skLineSegment(sketch, "E306", {"start": v(-122.18, 683.22) * mm, "end": v(-122.54, 683.41) * mm});
            skPoint(sketch, "E307.orphan", {"position": v(-151.3, 668.61) * mm});
            skCircle(sketch, "E308.MirrorC", {"center": v(78.74, 671.69) * mm, "radius": 76.2 * mm, "construction": true});
            skCircle(sketch, "E309.MirrorC", {"center": v(-128.74, 502.43) * mm, "radius": 76.2 * mm, "construction": true});
            skCircle(sketch, "E310.MirrorC", {"center": v(78.74, 502.43) * mm, "radius": 76.2 * mm, "construction": true});
            skLineSegment(sketch, "E311.MirrorCS", {"start": v(-134.94, 514.16) * mm, "end": v(-52.66, 557.65) * mm});
            skLineSegment(sketch, "E312.MirrorCS", {"start": v(-57.34, 525.18) * mm, "end": v(-122.18, 490.9) * mm});
            skArc(sketch, "E313.MirrorCS", {"start": v(-122.54, 490.7) * mm, "mid": v(-140.46, 496.23) * mm, "end": v(-134.94, 514.16) * mm});
            skLineSegment(sketch, "E314.MirrorCS", {"start": v(-54.8, 548.04) * mm, "end": v(-59.38, 535.94) * mm});
            skArc(sketch, "E315.MirrorCS", {"start": v(-57.34, 525.18) * mm, "mid": v(-52.42, 525.04) * mm, "end": v(-50, 520.76) * mm});
            skArc(sketch, "E316.MirrorCS", {"start": v(-50, 562.07) * mm, "mid": v(-50.72, 559.5) * mm, "end": v(-52.66, 557.65) * mm});
            skLineSegment(sketch, "E317.MirrorCS", {"start": v(-74.77, 541.44) * mm, "end": v(-57.6, 550.52) * mm});
            skLineSegment(sketch, "E318.MirrorCS", {"start": v(-61.71, 534.7) * mm, "end": v(-74.3, 537.73) * mm});
            skArc(sketch, "E319.MirrorCS", {"start": v(-59.38, 535.94) * mm, "mid": v(-60.31, 534.88) * mm, "end": v(-61.71, 534.7) * mm});
            skArc(sketch, "E320.MirrorCS", {"start": v(-57.6, 550.52) * mm, "mid": v(-55.34, 550.25) * mm, "end": v(-54.8, 548.04) * mm});
            skArc(sketch, "E321.MirrorCS", {"start": v(-74.3, 537.73) * mm, "mid": v(-75.82, 539.43) * mm, "end": v(-74.77, 541.44) * mm});
            skLineSegment(sketch, "E322.MirrorCS", {"start": v(-83.08, 535.73) * mm, "end": v(-70.5, 532.7) * mm});
            skLineSegment(sketch, "E323.MirrorCS", {"start": v(-90, 522.39) * mm, "end": v(-85.41, 534.5) * mm});
            skLineSegment(sketch, "E324.MirrorCS", {"start": v(-70.02, 528.99) * mm, "end": v(-87.19, 519.91) * mm});
            skArc(sketch, "E325.MirrorCS", {"start": v(-70.5, 532.7) * mm, "mid": v(-68.97, 531) * mm, "end": v(-70.02, 528.99) * mm});
            skArc(sketch, "E326.MirrorCS", {"start": v(-85.41, 534.5) * mm, "mid": v(-84.48, 535.55) * mm, "end": v(-83.08, 535.73) * mm});
            skArc(sketch, "E327.MirrorCS", {"start": v(-87.19, 519.91) * mm, "mid": v(-89.45, 520.18) * mm, "end": v(-90, 522.39) * mm});
            skLineSegment(sketch, "E328.MirrorCS", {"start": v(-111.98, 521.77) * mm, "end": v(-94.81, 530.84) * mm});
            skLineSegment(sketch, "E329.MirrorCS", {"start": v(-92, 528.37) * mm, "end": v(-96.59, 516.26) * mm});
            skLineSegment(sketch, "E330.MirrorCS", {"start": v(-98.93, 515.02) * mm, "end": v(-111.51, 518.06) * mm});
            skArc(sketch, "E331.MirrorCS", {"start": v(-96.59, 516.26) * mm, "mid": v(-97.53, 515.2) * mm, "end": v(-98.93, 515.02) * mm});
            skArc(sketch, "E332.MirrorCS", {"start": v(-111.51, 518.06) * mm, "mid": v(-113.03, 519.75) * mm, "end": v(-111.98, 521.77) * mm});
            skArc(sketch, "E333.MirrorCS", {"start": v(-94.81, 530.84) * mm, "mid": v(-92.56, 530.58) * mm, "end": v(-92, 528.37) * mm});
            skCircle(sketch, "E334.MirrorC", {"center": v(-128.74, 502.43) * mm, "radius": 3.4 * mm});
            skCircle(sketch, "E335.MirrorC", {"center": v(-125, 495.36) * mm, "radius": 1.4 * mm});
            skCircle(sketch, "E336.MirrorC", {"center": v(-137.14, 498) * mm, "radius": 1.4 * mm});
            skCircle(sketch, "E337.MirrorC", {"center": v(-132.48, 509.5) * mm, "radius": 1.4 * mm});
            skCircle(sketch, "E338.MirrorC", {"center": v(-120.34, 506.87) * mm, "radius": 1.4 * mm});
            skArc(sketch, "E339.MirrorCS", {"start": v(7.34, 525.18) * mm, "mid": v(2.42, 525.04) * mm, "end": v(0, 520.76) * mm});
            skArc(sketch, "E340.MirrorCS", {"start": v(0, 562.07) * mm, "mid": v(0.72, 559.5) * mm, "end": v(2.66, 557.65) * mm});
            skLineSegment(sketch, "E341.MirrorCS", {"start": v(84.94, 514.16) * mm, "end": v(2.66, 557.65) * mm});
            skLineSegment(sketch, "E342.MirrorCS", {"start": v(7.34, 525.18) * mm, "end": v(72.18, 490.9) * mm});
            skLineSegment(sketch, "E343.MirrorCS", {"start": v(4.8, 548.04) * mm, "end": v(9.38, 535.94) * mm});
            skArc(sketch, "E344.MirrorCS", {"start": v(7.6, 550.52) * mm, "mid": v(5.34, 550.25) * mm, "end": v(4.8, 548.04) * mm});
            skLineSegment(sketch, "E345.MirrorCS", {"start": v(24.77, 541.44) * mm, "end": v(7.6, 550.52) * mm});
            skLineSegment(sketch, "E346.MirrorCS", {"start": v(11.71, 534.7) * mm, "end": v(24.3, 537.73) * mm});
            skArc(sketch, "E347.MirrorCS", {"start": v(9.38, 535.94) * mm, "mid": v(10.31, 534.88) * mm, "end": v(11.71, 534.7) * mm});
            skArc(sketch, "E348.MirrorCS", {"start": v(24.3, 537.73) * mm, "mid": v(25.82, 539.43) * mm, "end": v(24.77, 541.44) * mm});
            skArc(sketch, "E349.MirrorCS", {"start": v(20.5, 532.7) * mm, "mid": v(18.97, 531) * mm, "end": v(20.02, 528.99) * mm});
            skArc(sketch, "E350.MirrorCS", {"start": v(35.41, 534.5) * mm, "mid": v(34.48, 535.55) * mm, "end": v(33.08, 535.73) * mm});
            skArc(sketch, "E351.MirrorCS", {"start": v(37.19, 519.91) * mm, "mid": v(39.45, 520.18) * mm, "end": v(40, 522.39) * mm});
            skLineSegment(sketch, "E352.MirrorCS", {"start": v(20.02, 528.99) * mm, "end": v(37.19, 519.91) * mm});
            skLineSegment(sketch, "E353.MirrorCS", {"start": v(40, 522.39) * mm, "end": v(35.41, 534.5) * mm});
            skLineSegment(sketch, "E354.MirrorCS", {"start": v(33.08, 535.73) * mm, "end": v(20.5, 532.7) * mm});
            skLineSegment(sketch, "E355.MirrorCS", {"start": v(42, 528.37) * mm, "end": v(46.59, 516.26) * mm});
            skLineSegment(sketch, "E356.MirrorCS", {"start": v(61.98, 521.77) * mm, "end": v(44.81, 530.84) * mm});
            skLineSegment(sketch, "E357.MirrorCS", {"start": v(48.93, 515.02) * mm, "end": v(61.51, 518.06) * mm});
            skArc(sketch, "E358.MirrorCS", {"start": v(46.59, 516.26) * mm, "mid": v(47.53, 515.2) * mm, "end": v(48.93, 515.02) * mm});
            skArc(sketch, "E359.MirrorCS", {"start": v(44.81, 530.84) * mm, "mid": v(42.56, 530.58) * mm, "end": v(42, 528.37) * mm});
            skArc(sketch, "E360.MirrorCS", {"start": v(61.51, 518.06) * mm, "mid": v(63.03, 519.75) * mm, "end": v(61.98, 521.77) * mm});
            skArc(sketch, "E361.MirrorCS", {"start": v(72.54, 490.7) * mm, "mid": v(90.46, 496.23) * mm, "end": v(84.94, 514.16) * mm});
            skCircle(sketch, "E362.MirrorC", {"center": v(75, 495.36) * mm, "radius": 1.4 * mm});
            skCircle(sketch, "E363.MirrorC", {"center": v(82.48, 509.5) * mm, "radius": 1.4 * mm});
            skCircle(sketch, "E364.MirrorC", {"center": v(87.14, 498) * mm, "radius": 1.4 * mm});
            skCircle(sketch, "E365.MirrorC", {"center": v(70.34, 506.87) * mm, "radius": 1.4 * mm});
            skCircle(sketch, "E366.MirrorC", {"center": v(78.74, 502.43) * mm, "radius": 3.4 * mm});
            skArc(sketch, "E367.MirrorCS", {"start": v(7.34, 648.94) * mm, "mid": v(2.42, 649.08) * mm, "end": v(0, 653.36) * mm});
            skArc(sketch, "E368.MirrorCS", {"start": v(0, 612.05) * mm, "mid": v(0.72, 614.63) * mm, "end": v(2.66, 616.47) * mm});
            skLineSegment(sketch, "E369.MirrorCS", {"start": v(84.94, 659.97) * mm, "end": v(2.66, 616.47) * mm});
            skLineSegment(sketch, "E370.MirrorCS", {"start": v(7.34, 648.94) * mm, "end": v(72.18, 683.22) * mm});
            skLineSegment(sketch, "E371.MirrorCS", {"start": v(4.8, 626.08) * mm, "end": v(9.38, 638.19) * mm});
            skLineSegment(sketch, "E372.MirrorCS", {"start": v(24.77, 632.68) * mm, "end": v(7.6, 623.6) * mm});
            skLineSegment(sketch, "E373.MirrorCS", {"start": v(11.71, 639.42) * mm, "end": v(24.3, 636.4) * mm});
            skArc(sketch, "E374.MirrorCS", {"start": v(7.6, 623.6) * mm, "mid": v(5.34, 623.87) * mm, "end": v(4.8, 626.08) * mm});
            skArc(sketch, "E375.MirrorCS", {"start": v(24.3, 636.4) * mm, "mid": v(25.82, 634.7) * mm, "end": v(24.77, 632.68) * mm});
            skArc(sketch, "E376.MirrorCS", {"start": v(9.38, 638.19) * mm, "mid": v(10.31, 639.25) * mm, "end": v(11.71, 639.42) * mm});
            skLineSegment(sketch, "E377.MirrorCS", {"start": v(33.08, 638.4) * mm, "end": v(20.5, 641.42) * mm});
            skLineSegment(sketch, "E378.MirrorCS", {"start": v(40, 651.74) * mm, "end": v(35.41, 639.63) * mm});
            skLineSegment(sketch, "E379.MirrorCS", {"start": v(20.02, 645.14) * mm, "end": v(37.19, 654.21) * mm});
            skArc(sketch, "E380.MirrorCS", {"start": v(37.19, 654.21) * mm, "mid": v(39.45, 653.94) * mm, "end": v(40, 651.74) * mm});
            skArc(sketch, "E381.MirrorCS", {"start": v(20.5, 641.42) * mm, "mid": v(18.97, 643.12) * mm, "end": v(20.02, 645.14) * mm});
            skArc(sketch, "E382.MirrorCS", {"start": v(35.41, 639.63) * mm, "mid": v(34.48, 638.57) * mm, "end": v(33.08, 638.4) * mm});
            skArc(sketch, "E383.MirrorCS", {"start": v(44.81, 643.28) * mm, "mid": v(42.56, 643.55) * mm, "end": v(42, 645.75) * mm});
            skLineSegment(sketch, "E384.MirrorCS", {"start": v(42, 645.75) * mm, "end": v(46.59, 657.86) * mm});
            skLineSegment(sketch, "E385.MirrorCS", {"start": v(61.98, 652.35) * mm, "end": v(44.81, 643.28) * mm});
            skLineSegment(sketch, "E386.MirrorCS", {"start": v(48.93, 659.1) * mm, "end": v(61.51, 656.07) * mm});
            skArc(sketch, "E387.MirrorCS", {"start": v(61.51, 656.07) * mm, "mid": v(63.03, 654.37) * mm, "end": v(61.98, 652.35) * mm});
            skArc(sketch, "E388.MirrorCS", {"start": v(46.59, 657.86) * mm, "mid": v(47.53, 658.92) * mm, "end": v(48.93, 659.1) * mm});
            skCircle(sketch, "E389.MirrorC", {"center": v(70.34, 667.25) * mm, "radius": 1.4 * mm});
            skCircle(sketch, "E390.MirrorC", {"center": v(82.48, 664.62) * mm, "radius": 1.4 * mm});
            skCircle(sketch, "E391.MirrorC", {"center": v(87.14, 676.13) * mm, "radius": 1.4 * mm});
            skCircle(sketch, "E392.MirrorC", {"center": v(75, 678.76) * mm, "radius": 1.4 * mm});
            skCircle(sketch, "E393.MirrorC", {"center": v(78.74, 671.69) * mm, "radius": 3.4 * mm});
            skArc(sketch, "E394.MirrorCS", {"start": v(72.54, 683.41) * mm, "mid": v(90.46, 677.89) * mm, "end": v(84.94, 659.97) * mm});
            skLineSegment(sketch, "E395.trimOffspring", {"start": v(0, 653.36) * mm, "end": v(0, 687.06) * mm});
            skLineSegment(sketch, "E396.trimOffspring", {"start": v(0, 562.07) * mm, "end": v(0, 612.05) * mm});
            skPoint(sketch, "E397.centerSnap0", {"position": v(-6, 663.06) * mm});
            skLineSegment(sketch, "E398", {"start": v(-50, 653.36) * mm, "end": v(-50, 612.05) * mm});
            skLineSegment(sketch, "E399", {"start": v(72.18, 683.22) * mm, "end": v(72.54, 683.41) * mm});
            skLineSegment(sketch, "E400", {"start": v(72.18, 490.9) * mm, "end": v(72.54, 490.7) * mm});
            skLineSegment(sketch, "E401", {"start": v(-122.18, 490.9) * mm, "end": v(-122.54, 490.7) * mm});
            skLineSegment(sketch, "E402.bottom", {"start": v(-20, 617.06) * mm, "end": v(-30, 617.06) * mm});
            skLineSegment(sketch, "E402.top", {"start": v(-20, 602.06) * mm, "end": v(-30, 602.06) * mm});
            skLineSegment(sketch, "E402.left", {"start": v(-17, 614.06) * mm, "end": v(-17, 605.06) * mm});
            skLineSegment(sketch, "E402.right", {"start": v(-33, 614.06) * mm, "end": v(-33, 605.06) * mm});
            skLineSegment(sketch, "E403.bottom", {"start": v(-20, 675.06) * mm, "end": v(-30, 675.06) * mm});
            skLineSegment(sketch, "E403.top", {"start": v(-20, 650.06) * mm, "end": v(-30, 650.06) * mm});
            skLineSegment(sketch, "E403.left", {"start": v(-17, 672.06) * mm, "end": v(-17, 653.06) * mm});
            skLineSegment(sketch, "E403.right", {"start": v(-33, 672.06) * mm, "end": v(-33, 653.06) * mm});
            skPoint(sketch, "E404.visualSharp", {"position": v(-33, 675.06) * mm});
            skArc(sketch, "E404.filletArc", {"start": v(-30, 675.06) * mm, "mid": v(-32.12, 674.18) * mm, "end": v(-33, 672.06) * mm});
            skPoint(sketch, "E405.visualSharp", {"position": v(-33, 650.06) * mm});
            skArc(sketch, "E405.filletArc", {"start": v(-33, 653.06) * mm, "mid": v(-32.12, 650.94) * mm, "end": v(-30, 650.06) * mm});
            skPoint(sketch, "E406.visualSharp", {"position": v(-17, 675.06) * mm});
            skArc(sketch, "E406.filletArc", {"start": v(-17, 672.06) * mm, "mid": v(-17.88, 674.18) * mm, "end": v(-20, 675.06) * mm});
            skPoint(sketch, "E407.visualSharp", {"position": v(-17, 650.06) * mm});
            skArc(sketch, "E407.filletArc", {"start": v(-20, 650.06) * mm, "mid": v(-17.88, 650.94) * mm, "end": v(-17, 653.06) * mm});
            skPoint(sketch, "E408.visualSharp", {"position": v(-33, 617.06) * mm});
            skArc(sketch, "E408.filletArc", {"start": v(-30, 617.06) * mm, "mid": v(-32.12, 616.18) * mm, "end": v(-33, 614.06) * mm});
            skPoint(sketch, "E409.visualSharp", {"position": v(-17, 602.06) * mm});
            skArc(sketch, "E409.filletArc", {"start": v(-20, 602.06) * mm, "mid": v(-17.88, 602.94) * mm, "end": v(-17, 605.06) * mm});
            skPoint(sketch, "E410.visualSharp", {"position": v(-17, 617.06) * mm});
            skArc(sketch, "E410.filletArc", {"start": v(-17, 614.06) * mm, "mid": v(-17.88, 616.18) * mm, "end": v(-20, 617.06) * mm});
            skPoint(sketch, "E411.visualSharp", {"position": v(-33, 602.06) * mm});
            skArc(sketch, "E411.filletArc", {"start": v(-33, 605.06) * mm, "mid": v(-32.12, 602.94) * mm, "end": v(-30, 602.06) * mm});
            skLineSegment(sketch, "E412.bottom", {"start": v(-20, 578.06) * mm, "end": v(-30, 578.06) * mm});
            skLineSegment(sketch, "E412.top", {"start": v(-20, 557.06) * mm, "end": v(-30, 557.06) * mm});
            skLineSegment(sketch, "E412.left", {"start": v(-17, 575.06) * mm, "end": v(-17, 560.06) * mm});
            skLineSegment(sketch, "E412.right", {"start": v(-33, 575.06) * mm, "end": v(-33, 560.06) * mm});
            skPoint(sketch, "E413.visualSharp", {"position": v(-33, 578.06) * mm});
            skArc(sketch, "E413.filletArc", {"start": v(-30, 578.06) * mm, "mid": v(-32.12, 577.18) * mm, "end": v(-33, 575.06) * mm});
            skPoint(sketch, "E414.visualSharp", {"position": v(-33, 557.06) * mm});
            skArc(sketch, "E414.filletArc", {"start": v(-33, 560.06) * mm, "mid": v(-32.12, 557.94) * mm, "end": v(-30, 557.06) * mm});
            skPoint(sketch, "E415.visualSharp", {"position": v(-17, 557.06) * mm});
            skArc(sketch, "E415.filletArc", {"start": v(-20, 557.06) * mm, "mid": v(-17.88, 557.94) * mm, "end": v(-17, 560.06) * mm});
            skPoint(sketch, "E416.visualSharp", {"position": v(-17, 578.06) * mm});
            skArc(sketch, "E416.filletArc", {"start": v(-17, 575.06) * mm, "mid": v(-17.88, 577.18) * mm, "end": v(-20, 578.06) * mm});
            skLineSegment(sketch, "E417", {"start": v(-47, 572.06) * mm, "end": v(-47, 522.06) * mm, "construction": true});
            skLineSegment(sketch, "E418", {"start": v(-47, 522.06) * mm, "end": v(-47, 500.06) * mm});
            skLineSegment(sketch, "E419", {"start": v(-47, 500.06) * mm, "end": v(-44, 500.06) * mm});
            skLineSegment(sketch, "E420", {"start": v(-44, 500.06) * mm, "end": v(-44, 522.06) * mm});
            skLineSegment(sketch, "E421", {"start": v(-44, 522.06) * mm, "end": v(-47, 522.06) * mm});
            skLineSegment(sketch, "E422.MirrorCS", {"start": v(-3, 522.06) * mm, "end": v(-3, 500.06) * mm});
            skLineSegment(sketch, "E423.MirrorCS", {"start": v(-6, 500.06) * mm, "end": v(-6, 522.06) * mm});
            skLineSegment(sketch, "E424.MirrorCS", {"start": v(-25, 515.94) * mm, "end": v(0, 515.94) * mm, "construction": true});
            skLineSegment(sketch, "E425.MirrorCS", {"start": v(-6, 522.06) * mm, "end": v(-3, 522.06) * mm});
            skLineSegment(sketch, "E426.MirrorCS", {"start": v(-3, 572.06) * mm, "end": v(-3, 522.06) * mm, "construction": true});
            skLineSegment(sketch, "E427.MirrorCS", {"start": v(-3, 500.06) * mm, "end": v(-6, 500.06) * mm});
            skLineSegment(sketch, "E428", {"start": v(-44, 511.06) * mm, "end": v(-6, 511.06) * mm, "construction": true});
            skLineSegment(sketch, "E429", {"start": v(-35, 511.06) * mm, "end": v(-35, 509.56) * mm});
            skLineSegment(sketch, "E430", {"start": v(-35, 509.56) * mm, "end": v(-25, 509.56) * mm});
            skLineSegment(sketch, "E431.MirrorCS", {"start": v(-35, 512.56) * mm, "end": v(-25, 512.56) * mm});
            skLineSegment(sketch, "E432.MirrorCS", {"start": v(-35, 511.06) * mm, "end": v(-35, 512.56) * mm});
            skLineSegment(sketch, "E433.MirrorCS", {"start": v(-15, 509.56) * mm, "end": v(-25, 509.56) * mm});
            skLineSegment(sketch, "E434.MirrorCS", {"start": v(-15, 512.56) * mm, "end": v(-25, 512.56) * mm});
            skLineSegment(sketch, "E435.MirrorCS", {"start": v(-15, 511.06) * mm, "end": v(-15, 512.56) * mm});
            skLineSegment(sketch, "E436.MirrorCS", {"start": v(-15, 511.06) * mm, "end": v(-15, 509.56) * mm});
            skLineSegment(sketch, "E437.bottom", {"start": v(-33.16, 821.8) * mm, "end": v(-33.16, 821.8) * mm});
            skLineSegment(sketch, "E437.top", {"start": v(6.84, 1039.8) * mm, "end": v(-33.16, 1039.8) * mm});
            skLineSegment(sketch, "E437.left", {"start": v(11.84, 826.8) * mm, "end": v(11.84, 868.5) * mm});
            skLineSegment(sketch, "E437.right", {"start": v(-38.16, 826.8) * mm, "end": v(-38.16, 868.5) * mm});
            skLineSegment(sketch, "E438", {"start": v(-45.5, 996.68) * mm, "end": v(-110.33, 1030.96) * mm});
            skLineSegment(sketch, "E439", {"start": v(-123.1, 1007.7) * mm, "end": v(-40.82, 964.2) * mm});
            skLineSegment(sketch, "E440", {"start": v(-13.16, 863.68) * mm, "end": v(-38.16, 863.68) * mm, "construction": true});
            skPoint(sketch, "E441.centerSnap0", {"position": v(-123.12, 1019.43) * mm});
            skCircle(sketch, "E442", {"center": v(-113.16, 1026.5) * mm, "radius": 1.4 * mm});
            skCircle(sketch, "E443.MirrorC", {"center": v(-120.63, 1012.36) * mm, "radius": 1.4 * mm});
            skCircle(sketch, "E444", {"center": v(-116.9, 1019.43) * mm, "radius": 3.4 * mm});
            skCircle(sketch, "E445", {"center": v(-108.5, 1014.99) * mm, "radius": 1.4 * mm});
            skCircle(sketch, "E446.MirrorC", {"center": v(-125.3, 1023.87) * mm, "radius": 1.4 * mm});
            skLineSegment(sketch, "E447", {"start": v(-38.16, 934.8) * mm, "end": v(11.84, 934.8) * mm, "construction": true});
            skPoint(sketch, "E448.newPointB", {"position": v(-38.16, 1039.8) * mm});
            skLineSegment(sketch, "E449", {"start": v(-38.16, 959.79) * mm, "end": v(-38.16, 909.81) * mm});
            skPoint(sketch, "E450.visualSharp", {"position": v(-38.16, 962.8) * mm});
            skArc(sketch, "E450.filletArc", {"start": v(-38.16, 959.79) * mm, "mid": v(-38.87, 962.37) * mm, "end": v(-40.82, 964.2) * mm});
            skLineSegment(sketch, "E451", {"start": v(-38.16, 1001.1) * mm, "end": v(-38.16, 1034.8) * mm});
            skPoint(sketch, "E452.visualSharp", {"position": v(-38.16, 992.8) * mm});
            skArc(sketch, "E452.filletArc", {"start": v(-45.5, 996.68) * mm, "mid": v(-40.58, 996.82) * mm, "end": v(-38.16, 1001.1) * mm});
            skLineSegment(sketch, "E453.bottom", {"start": v(-35.16, 1021.8) * mm, "end": v(-32.16, 1021.8) * mm});
            skLineSegment(sketch, "E453.top", {"start": v(-35.16, 999.8) * mm, "end": v(-32.16, 999.8) * mm});
            skLineSegment(sketch, "E453.left", {"start": v(-35.16, 1021.8) * mm, "end": v(-35.16, 999.8) * mm});
            skLineSegment(sketch, "E453.right", {"start": v(-32.16, 1021.8) * mm, "end": v(-32.16, 999.8) * mm});
            skLineSegment(sketch, "E454.bottom", {"start": v(-32.16, 941.8) * mm, "end": v(-35.16, 941.8) * mm});
            skLineSegment(sketch, "E454.top", {"start": v(-32.16, 919.8) * mm, "end": v(-35.16, 919.8) * mm});
            skLineSegment(sketch, "E454.left", {"start": v(-32.16, 941.8) * mm, "end": v(-32.16, 919.8) * mm});
            skLineSegment(sketch, "E454.right", {"start": v(-35.16, 941.8) * mm, "end": v(-35.16, 919.8) * mm});
            skArc(sketch, "E455.filletArc", {"start": v(-33.16, 1039.8) * mm, "mid": v(-36.7, 1038.33) * mm, "end": v(-38.16, 1034.8) * mm});
            skArc(sketch, "E456.filletArc", {"start": v(-38.16, 826.8) * mm, "mid": v(-36.7, 823.26) * mm, "end": v(-33.16, 821.8) * mm});
            skArc(sketch, "E457.filletArc", {"start": v(6.84, 821.8) * mm, "mid": v(10.38, 823.26) * mm, "end": v(11.84, 826.8) * mm});
            skArc(sketch, "E458.filletArc", {"start": v(11.84, 1034.8) * mm, "mid": v(10.38, 1038.33) * mm, "end": v(6.84, 1039.8) * mm});
            skLineSegment(sketch, "E459", {"start": v(-100.14, 1000.1) * mm, "end": v(-82.97, 991.02) * mm});
            skLineSegment(sketch, "E460", {"start": v(-80.16, 993.5) * mm, "end": v(-84.75, 1005.6) * mm});
            skLineSegment(sketch, "E461", {"start": v(-87.08, 1006.84) * mm, "end": v(-99.67, 1003.8) * mm});
            skLineSegment(sketch, "E462", {"start": v(-78.15, 999.47) * mm, "end": v(-73.57, 987.37) * mm});
            skLineSegment(sketch, "E463", {"start": v(-71.23, 986.13) * mm, "end": v(-58.65, 989.16) * mm});
            skLineSegment(sketch, "E464", {"start": v(-58.18, 992.87) * mm, "end": v(-75.35, 1001.95) * mm});
            skPoint(sketch, "E465.visualSharp", {"position": v(-80.02, 1004.42) * mm});
            skArc(sketch, "E465.filletArc", {"start": v(-75.35, 1001.95) * mm, "mid": v(-77.6, 1001.68) * mm, "end": v(-78.15, 999.47) * mm});
            skPoint(sketch, "E466.visualSharp", {"position": v(-72.95, 985.72) * mm});
            skArc(sketch, "E466.filletArc", {"start": v(-73.57, 987.37) * mm, "mid": v(-72.63, 986.3) * mm, "end": v(-71.23, 986.13) * mm});
            skPoint(sketch, "E467.visualSharp", {"position": v(-53.5, 990.4) * mm});
            skArc(sketch, "E467.filletArc", {"start": v(-58.65, 989.16) * mm, "mid": v(-57.13, 990.86) * mm, "end": v(-58.18, 992.87) * mm});
            skPoint(sketch, "E468.visualSharp", {"position": v(-78.3, 988.54) * mm});
            skArc(sketch, "E468.filletArc", {"start": v(-82.97, 991.02) * mm, "mid": v(-80.71, 991.28) * mm, "end": v(-80.16, 993.5) * mm});
            skPoint(sketch, "E469.visualSharp", {"position": v(-104.81, 1002.56) * mm});
            skArc(sketch, "E469.filletArc", {"start": v(-99.67, 1003.8) * mm, "mid": v(-101.19, 1002.1) * mm, "end": v(-100.14, 1000.1) * mm});
            skPoint(sketch, "E470.visualSharp", {"position": v(-85.37, 1007.25) * mm});
            skArc(sketch, "E470.filletArc", {"start": v(-84.75, 1005.6) * mm, "mid": v(-85.68, 1006.66) * mm, "end": v(-87.08, 1006.84) * mm});
            skLineSegment(sketch, "E471", {"start": v(-62.92, 980.42) * mm, "end": v(-45.76, 971.34) * mm});
            skLineSegment(sketch, "E472", {"start": v(-42.95, 973.82) * mm, "end": v(-47.53, 985.92) * mm});
            skLineSegment(sketch, "E473", {"start": v(-49.87, 987.16) * mm, "end": v(-62.46, 984.13) * mm});
            skPoint(sketch, "E474.visualSharp", {"position": v(-64.13, 992.14) * mm});
            skArc(sketch, "E475.filletArc", {"start": v(-45.76, 971.34) * mm, "mid": v(-43.5, 971.61) * mm, "end": v(-42.95, 973.82) * mm});
            skArc(sketch, "E476.filletArc", {"start": v(-62.46, 984.13) * mm, "mid": v(-63.97, 982.43) * mm, "end": v(-62.92, 980.42) * mm});
            skPoint(sketch, "E477.visualSharp", {"position": v(-48.16, 987.57) * mm});
            skArc(sketch, "E477.filletArc", {"start": v(-47.53, 985.92) * mm, "mid": v(-48.47, 986.98) * mm, "end": v(-49.87, 987.16) * mm});
            skLineSegment(sketch, "E478", {"start": v(-26.16, 831.68) * mm, "end": v(-0.16, 831.68) * mm});
            skLineSegment(sketch, "E479", {"start": v(-28.16, 829.68) * mm, "end": v(-28.16, 826.8) * mm});
            skLineSegment(sketch, "E480", {"start": v(1.84, 829.68) * mm, "end": v(1.84, 826.8) * mm});
            skArc(sketch, "E481.filletArc", {"start": v(-33.16, 821.8) * mm, "mid": v(-29.62, 823.26) * mm, "end": v(-28.16, 826.8) * mm});
            skLineSegment(sketch, "E482", {"start": v(6.84, 821.8) * mm, "end": v(6.84, 821.8) * mm});
            skPoint(sketch, "E483.visualSharp", {"position": v(1.84, 821.8) * mm});
            skArc(sketch, "E483.filletArc", {"start": v(1.84, 826.8) * mm, "mid": v(3.3, 823.26) * mm, "end": v(6.84, 821.8) * mm});
            skPoint(sketch, "E484.visualSharp", {"position": v(-28.16, 831.68) * mm});
            skArc(sketch, "E484.filletArc", {"start": v(-26.16, 831.68) * mm, "mid": v(-27.57, 831.1) * mm, "end": v(-28.16, 829.68) * mm});
            skPoint(sketch, "E485.visualSharp", {"position": v(1.84, 831.68) * mm});
            skArc(sketch, "E485.filletArc", {"start": v(1.84, 829.68) * mm, "mid": v(1.26, 831.1) * mm, "end": v(-0.16, 831.68) * mm});
            skCircle(sketch, "E486", {"center": v(-20.16, 863.68) * mm, "radius": 1 * mm});
            skCircle(sketch, "E487.MirrorC", {"center": v(-6.16, 863.68) * mm, "radius": 1 * mm});
            skCircle(sketch, "E488", {"center": v(-13.16, 863.68) * mm, "radius": 1 * mm});
            skLineSegment(sketch, "E489.MirrorCS", {"start": v(5.84, 941.8) * mm, "end": v(5.84, 919.8) * mm});
            skLineSegment(sketch, "E490.MirrorCS", {"start": v(5.84, 919.8) * mm, "end": v(8.84, 919.8) * mm});
            skLineSegment(sketch, "E491.MirrorCS", {"start": v(8.84, 941.8) * mm, "end": v(8.84, 919.8) * mm});
            skLineSegment(sketch, "E492.MirrorCS", {"start": v(5.84, 941.8) * mm, "end": v(8.84, 941.8) * mm});
            skLineSegment(sketch, "E493.MirrorCS", {"start": v(8.84, 999.8) * mm, "end": v(5.84, 999.8) * mm});
            skLineSegment(sketch, "E494.MirrorCS", {"start": v(8.84, 1021.8) * mm, "end": v(8.84, 999.8) * mm});
            skLineSegment(sketch, "E495.MirrorCS", {"start": v(5.84, 1021.8) * mm, "end": v(5.84, 999.8) * mm});
            skLineSegment(sketch, "E496.MirrorCS", {"start": v(8.84, 1021.8) * mm, "end": v(5.84, 1021.8) * mm});
            skCircle(sketch, "E497", {"center": v(-116.9, 1019.43) * mm, "radius": 76.2 * mm, "construction": true});
            skLineSegment(sketch, "E498", {"start": v(-116.9, 1019.43) * mm, "end": v(-108.5, 1014.99) * mm, "construction": true});
            skLineSegment(sketch, "E499", {"start": v(-116.9, 1019.43) * mm, "end": v(-113.16, 1026.5) * mm, "construction": true});
            skLineSegment(sketch, "E500", {"start": v(-116.9, 1019.43) * mm, "end": v(-125.3, 1023.87) * mm, "construction": true});
            skLineSegment(sketch, "E501", {"start": v(-116.9, 1019.43) * mm, "end": v(-120.63, 1012.36) * mm, "construction": true});
            skLineSegment(sketch, "E502", {"start": v(-38.16, 1001.1) * mm, "end": v(-38.16, 959.79) * mm, "construction": true});
            skLineSegment(sketch, "E503", {"start": v(-91.7, 1021.1) * mm, "end": v(-104.1, 997.66) * mm, "construction": true});
            skLineSegment(sketch, "E504", {"start": v(-97.9, 1009.39) * mm, "end": v(-116.9, 1019.43) * mm, "construction": true});
            skArc(sketch, "E505", {"start": v(-110.7, 1031.15) * mm, "mid": v(-128.62, 1025.63) * mm, "end": v(-123.1, 1007.7) * mm});
            skLineSegment(sketch, "E506", {"start": v(-116.9, 1019.43) * mm, "end": v(-110.7, 1031.15) * mm});
            skLineSegment(sketch, "E507", {"start": v(-110.33, 1030.96) * mm, "end": v(-110.7, 1031.15) * mm});
            skPoint(sketch, "E508.orphan", {"position": v(-139.45, 1016.35) * mm});
            skCircle(sketch, "E509.MirrorC", {"center": v(90.58, 1019.43) * mm, "radius": 76.2 * mm, "construction": true});
            skCircle(sketch, "E510.MirrorC", {"center": v(-116.9, 850.17) * mm, "radius": 76.2 * mm, "construction": true});
            skCircle(sketch, "E511.MirrorC", {"center": v(90.58, 850.17) * mm, "radius": 76.2 * mm, "construction": true});
            skLineSegment(sketch, "E512.MirrorCS", {"start": v(-123.1, 861.9) * mm, "end": v(-40.82, 905.4) * mm});
            skLineSegment(sketch, "E513.MirrorCS", {"start": v(-45.5, 872.92) * mm, "end": v(-110.33, 838.64) * mm});
            skArc(sketch, "E514.MirrorCS", {"start": v(-110.7, 838.45) * mm, "mid": v(-128.62, 843.97) * mm, "end": v(-123.1, 861.9) * mm});
            skLineSegment(sketch, "E515.MirrorCS", {"start": v(-42.95, 895.78) * mm, "end": v(-47.53, 883.67) * mm});
            skArc(sketch, "E516.MirrorCS", {"start": v(-45.5, 872.92) * mm, "mid": v(-40.58, 872.78) * mm, "end": v(-38.16, 868.5) * mm});
            skArc(sketch, "E517.MirrorCS", {"start": v(-38.16, 909.81) * mm, "mid": v(-38.87, 907.23) * mm, "end": v(-40.82, 905.4) * mm});
            skLineSegment(sketch, "E518.MirrorCS", {"start": v(-62.92, 889.18) * mm, "end": v(-45.76, 898.26) * mm});
            skLineSegment(sketch, "E519.MirrorCS", {"start": v(-49.87, 882.44) * mm, "end": v(-62.46, 885.47) * mm});
            skArc(sketch, "E520.MirrorCS", {"start": v(-47.53, 883.67) * mm, "mid": v(-48.47, 882.61) * mm, "end": v(-49.87, 882.44) * mm});
            skArc(sketch, "E521.MirrorCS", {"start": v(-45.76, 898.26) * mm, "mid": v(-43.5, 897.99) * mm, "end": v(-42.95, 895.78) * mm});
            skArc(sketch, "E522.MirrorCS", {"start": v(-62.46, 885.47) * mm, "mid": v(-63.97, 887.16) * mm, "end": v(-62.92, 889.18) * mm});
            skLineSegment(sketch, "E523.MirrorCS", {"start": v(-71.23, 883.47) * mm, "end": v(-58.65, 880.44) * mm});
            skLineSegment(sketch, "E524.MirrorCS", {"start": v(-78.15, 870.12) * mm, "end": v(-73.57, 882.23) * mm});
            skLineSegment(sketch, "E525.MirrorCS", {"start": v(-58.18, 876.72) * mm, "end": v(-75.35, 867.65) * mm});
            skArc(sketch, "E526.MirrorCS", {"start": v(-58.65, 880.44) * mm, "mid": v(-57.13, 878.74) * mm, "end": v(-58.18, 876.72) * mm});
            skArc(sketch, "E527.MirrorCS", {"start": v(-73.57, 882.23) * mm, "mid": v(-72.63, 883.3) * mm, "end": v(-71.23, 883.47) * mm});
            skArc(sketch, "E528.MirrorCS", {"start": v(-75.35, 867.65) * mm, "mid": v(-77.6, 867.92) * mm, "end": v(-78.15, 870.12) * mm});
            skLineSegment(sketch, "E529.MirrorCS", {"start": v(-100.14, 869.5) * mm, "end": v(-82.97, 878.58) * mm});
            skLineSegment(sketch, "E530.MirrorCS", {"start": v(-80.16, 876.1) * mm, "end": v(-84.75, 864) * mm});
            skLineSegment(sketch, "E531.MirrorCS", {"start": v(-87.08, 862.76) * mm, "end": v(-99.67, 865.8) * mm});
            skArc(sketch, "E532.MirrorCS", {"start": v(-84.75, 864) * mm, "mid": v(-85.68, 862.94) * mm, "end": v(-87.08, 862.76) * mm});
            skArc(sketch, "E533.MirrorCS", {"start": v(-99.67, 865.8) * mm, "mid": v(-101.19, 867.49) * mm, "end": v(-100.14, 869.5) * mm});
            skArc(sketch, "E534.MirrorCS", {"start": v(-82.97, 878.58) * mm, "mid": v(-80.71, 878.31) * mm, "end": v(-80.16, 876.1) * mm});
            skCircle(sketch, "E535.MirrorC", {"center": v(-116.9, 850.17) * mm, "radius": 3.4 * mm});
            skCircle(sketch, "E536.MirrorC", {"center": v(-113.16, 843.1) * mm, "radius": 1.4 * mm});
            skCircle(sketch, "E537.MirrorC", {"center": v(-125.3, 845.73) * mm, "radius": 1.4 * mm});
            skCircle(sketch, "E538.MirrorC", {"center": v(-120.63, 857.24) * mm, "radius": 1.4 * mm});
            skCircle(sketch, "E539.MirrorC", {"center": v(-108.5, 854.61) * mm, "radius": 1.4 * mm});
            skArc(sketch, "E540.MirrorCS", {"start": v(19.18, 872.92) * mm, "mid": v(14.26, 872.78) * mm, "end": v(11.84, 868.5) * mm});
            skArc(sketch, "E541.MirrorCS", {"start": v(11.84, 909.81) * mm, "mid": v(12.56, 907.23) * mm, "end": v(14.5, 905.4) * mm});
            skLineSegment(sketch, "E542.MirrorCS", {"start": v(96.78, 861.9) * mm, "end": v(14.5, 905.4) * mm});
            skLineSegment(sketch, "E543.MirrorCS", {"start": v(19.18, 872.92) * mm, "end": v(84.02, 838.64) * mm});
            skLineSegment(sketch, "E544.MirrorCS", {"start": v(16.64, 895.78) * mm, "end": v(21.22, 883.67) * mm});
            skArc(sketch, "E545.MirrorCS", {"start": v(19.44, 898.26) * mm, "mid": v(17.19, 897.99) * mm, "end": v(16.64, 895.78) * mm});
            skLineSegment(sketch, "E546.MirrorCS", {"start": v(36.61, 889.18) * mm, "end": v(19.44, 898.26) * mm});
            skLineSegment(sketch, "E547.MirrorCS", {"start": v(23.56, 882.44) * mm, "end": v(36.14, 885.47) * mm});
            skArc(sketch, "E548.MirrorCS", {"start": v(21.22, 883.67) * mm, "mid": v(22.16, 882.61) * mm, "end": v(23.56, 882.44) * mm});
            skArc(sketch, "E549.MirrorCS", {"start": v(36.14, 885.47) * mm, "mid": v(37.66, 887.16) * mm, "end": v(36.61, 889.18) * mm});
            skArc(sketch, "E550.MirrorCS", {"start": v(32.33, 880.44) * mm, "mid": v(30.82, 878.74) * mm, "end": v(31.87, 876.72) * mm});
            skArc(sketch, "E551.MirrorCS", {"start": v(47.26, 882.23) * mm, "mid": v(46.32, 883.3) * mm, "end": v(44.92, 883.47) * mm});
            skArc(sketch, "E552.MirrorCS", {"start": v(49.03, 867.65) * mm, "mid": v(51.3, 867.92) * mm, "end": v(51.84, 870.12) * mm});
            skLineSegment(sketch, "E553.MirrorCS", {"start": v(31.87, 876.72) * mm, "end": v(49.03, 867.65) * mm});
            skLineSegment(sketch, "E554.MirrorCS", {"start": v(51.84, 870.12) * mm, "end": v(47.26, 882.23) * mm});
            skLineSegment(sketch, "E555.MirrorCS", {"start": v(44.92, 883.47) * mm, "end": v(32.33, 880.44) * mm});
            skLineSegment(sketch, "E556.MirrorCS", {"start": v(53.85, 876.1) * mm, "end": v(58.43, 864) * mm});
            skLineSegment(sketch, "E557.MirrorCS", {"start": v(73.82, 869.5) * mm, "end": v(56.66, 878.58) * mm});
            skLineSegment(sketch, "E558.MirrorCS", {"start": v(60.77, 862.76) * mm, "end": v(73.36, 865.8) * mm});
            skArc(sketch, "E559.MirrorCS", {"start": v(58.43, 864) * mm, "mid": v(59.37, 862.94) * mm, "end": v(60.77, 862.76) * mm});
            skArc(sketch, "E560.MirrorCS", {"start": v(56.66, 878.58) * mm, "mid": v(54.4, 878.31) * mm, "end": v(53.85, 876.1) * mm});
            skArc(sketch, "E561.MirrorCS", {"start": v(73.36, 865.8) * mm, "mid": v(74.87, 867.49) * mm, "end": v(73.82, 869.5) * mm});
            skArc(sketch, "E562.MirrorCS", {"start": v(84.39, 838.45) * mm, "mid": v(102.3, 843.97) * mm, "end": v(96.78, 861.9) * mm});
            skCircle(sketch, "E563.MirrorC", {"center": v(86.85, 843.1) * mm, "radius": 1.4 * mm});
            skCircle(sketch, "E564.MirrorC", {"center": v(94.32, 857.24) * mm, "radius": 1.4 * mm});
            skCircle(sketch, "E565.MirrorC", {"center": v(98.98, 845.73) * mm, "radius": 1.4 * mm});
            skCircle(sketch, "E566.MirrorC", {"center": v(82.19, 854.61) * mm, "radius": 1.4 * mm});
            skCircle(sketch, "E567.MirrorC", {"center": v(90.58, 850.17) * mm, "radius": 3.4 * mm});
            skArc(sketch, "E568.MirrorCS", {"start": v(19.18, 996.68) * mm, "mid": v(14.26, 996.82) * mm, "end": v(11.84, 1001.1) * mm});
            skArc(sketch, "E569.MirrorCS", {"start": v(11.84, 959.79) * mm, "mid": v(12.56, 962.37) * mm, "end": v(14.5, 964.2) * mm});
            skLineSegment(sketch, "E570.MirrorCS", {"start": v(96.78, 1007.7) * mm, "end": v(14.5, 964.2) * mm});
            skLineSegment(sketch, "E571.MirrorCS", {"start": v(19.18, 996.68) * mm, "end": v(84.02, 1030.96) * mm});
            skLineSegment(sketch, "E572.MirrorCS", {"start": v(16.64, 973.82) * mm, "end": v(21.22, 985.92) * mm});
            skLineSegment(sketch, "E573.MirrorCS", {"start": v(36.61, 980.42) * mm, "end": v(19.44, 971.34) * mm});
            skLineSegment(sketch, "E574.MirrorCS", {"start": v(23.56, 987.16) * mm, "end": v(36.14, 984.13) * mm});
            skArc(sketch, "E575.MirrorCS", {"start": v(19.44, 971.34) * mm, "mid": v(17.19, 971.61) * mm, "end": v(16.64, 973.82) * mm});
            skArc(sketch, "E576.MirrorCS", {"start": v(36.14, 984.13) * mm, "mid": v(37.66, 982.43) * mm, "end": v(36.61, 980.42) * mm});
            skArc(sketch, "E577.MirrorCS", {"start": v(21.22, 985.92) * mm, "mid": v(22.16, 986.98) * mm, "end": v(23.56, 987.16) * mm});
            skLineSegment(sketch, "E578.MirrorCS", {"start": v(44.92, 986.13) * mm, "end": v(32.33, 989.16) * mm});
            skLineSegment(sketch, "E579.MirrorCS", {"start": v(51.84, 999.47) * mm, "end": v(47.26, 987.37) * mm});
            skLineSegment(sketch, "E580.MirrorCS", {"start": v(31.87, 992.87) * mm, "end": v(49.03, 1001.95) * mm});
            skArc(sketch, "E581.MirrorCS", {"start": v(49.03, 1001.95) * mm, "mid": v(51.3, 1001.68) * mm, "end": v(51.84, 999.47) * mm});
            skArc(sketch, "E582.MirrorCS", {"start": v(32.33, 989.16) * mm, "mid": v(30.82, 990.86) * mm, "end": v(31.87, 992.87) * mm});
            skArc(sketch, "E583.MirrorCS", {"start": v(47.26, 987.37) * mm, "mid": v(46.32, 986.3) * mm, "end": v(44.92, 986.13) * mm});
            skArc(sketch, "E584.MirrorCS", {"start": v(56.66, 991.02) * mm, "mid": v(54.4, 991.28) * mm, "end": v(53.85, 993.5) * mm});
            skLineSegment(sketch, "E585.MirrorCS", {"start": v(53.85, 993.5) * mm, "end": v(58.43, 1005.6) * mm});
            skLineSegment(sketch, "E586.MirrorCS", {"start": v(73.82, 1000.1) * mm, "end": v(56.66, 991.02) * mm});
            skLineSegment(sketch, "E587.MirrorCS", {"start": v(60.77, 1006.84) * mm, "end": v(73.36, 1003.8) * mm});
            skArc(sketch, "E588.MirrorCS", {"start": v(73.36, 1003.8) * mm, "mid": v(74.87, 1002.1) * mm, "end": v(73.82, 1000.1) * mm});
            skArc(sketch, "E589.MirrorCS", {"start": v(58.43, 1005.6) * mm, "mid": v(59.37, 1006.66) * mm, "end": v(60.77, 1006.84) * mm});
            skCircle(sketch, "E590.MirrorC", {"center": v(82.19, 1014.99) * mm, "radius": 1.4 * mm});
            skCircle(sketch, "E591.MirrorC", {"center": v(94.32, 1012.36) * mm, "radius": 1.4 * mm});
            skCircle(sketch, "E592.MirrorC", {"center": v(98.98, 1023.87) * mm, "radius": 1.4 * mm});
            skCircle(sketch, "E593.MirrorC", {"center": v(86.85, 1026.5) * mm, "radius": 1.4 * mm});
            skCircle(sketch, "E594.MirrorC", {"center": v(90.58, 1019.43) * mm, "radius": 3.4 * mm});
            skArc(sketch, "E595.MirrorCS", {"start": v(84.39, 1031.15) * mm, "mid": v(102.3, 1025.63) * mm, "end": v(96.78, 1007.7) * mm});
            skLineSegment(sketch, "E596.trimOffspring", {"start": v(11.84, 1001.1) * mm, "end": v(11.84, 1034.8) * mm});
            skLineSegment(sketch, "E597.trimOffspring", {"start": v(11.84, 909.81) * mm, "end": v(11.84, 959.79) * mm});
            skPoint(sketch, "E598.centerSnap0", {"position": v(5.84, 1010.8) * mm});
            skLineSegment(sketch, "E599", {"start": v(-38.16, 1001.1) * mm, "end": v(-38.16, 959.79) * mm});
            skLineSegment(sketch, "E600", {"start": v(84.02, 1030.96) * mm, "end": v(84.39, 1031.15) * mm});
            skLineSegment(sketch, "E601", {"start": v(84.02, 838.64) * mm, "end": v(84.39, 838.45) * mm});
            skLineSegment(sketch, "E602", {"start": v(-110.33, 838.64) * mm, "end": v(-110.7, 838.45) * mm});
            skLineSegment(sketch, "E603.bottom", {"start": v(-8.16, 964.8) * mm, "end": v(-18.16, 964.8) * mm});
            skLineSegment(sketch, "E603.top", {"start": v(-8.16, 949.8) * mm, "end": v(-18.16, 949.8) * mm});
            skLineSegment(sketch, "E603.left", {"start": v(-5.16, 961.8) * mm, "end": v(-5.16, 952.8) * mm});
            skLineSegment(sketch, "E604.bottom", {"start": v(-8.16, 1022.8) * mm, "end": v(-18.16, 1022.8) * mm});
            skLineSegment(sketch, "E604.top", {"start": v(-8.16, 997.8) * mm, "end": v(-18.16, 997.8) * mm});
            skLineSegment(sketch, "E604.left", {"start": v(-5.16, 1019.8) * mm, "end": v(-5.16, 1000.8) * mm});
            skLineSegment(sketch, "E604.right", {"start": v(-21.16, 1019.8) * mm, "end": v(-21.16, 1000.8) * mm});
            skPoint(sketch, "E605.visualSharp", {"position": v(-21.16, 1022.8) * mm});
            skArc(sketch, "E605.filletArc", {"start": v(-18.16, 1022.8) * mm, "mid": v(-20.28, 1021.92) * mm, "end": v(-21.16, 1019.8) * mm});
            skPoint(sketch, "E606.visualSharp", {"position": v(-21.16, 997.8) * mm});
            skArc(sketch, "E606.filletArc", {"start": v(-21.16, 1000.8) * mm, "mid": v(-20.28, 998.68) * mm, "end": v(-18.16, 997.8) * mm});
            skPoint(sketch, "E607.visualSharp", {"position": v(-5.16, 1022.8) * mm});
            skArc(sketch, "E607.filletArc", {"start": v(-5.16, 1019.8) * mm, "mid": v(-6.03, 1021.92) * mm, "end": v(-8.16, 1022.8) * mm});
            skPoint(sketch, "E608.visualSharp", {"position": v(-5.16, 997.8) * mm});
            skArc(sketch, "E608.filletArc", {"start": v(-8.16, 997.8) * mm, "mid": v(-6.03, 998.68) * mm, "end": v(-5.16, 1000.8) * mm});
            skPoint(sketch, "E609.visualSharp", {"position": v(-21.16, 964.8) * mm});
            skPoint(sketch, "E610.visualSharp", {"position": v(-5.16, 949.8) * mm});
            skArc(sketch, "E610.filletArc", {"start": v(-8.16, 949.8) * mm, "mid": v(-6.03, 950.68) * mm, "end": v(-5.16, 952.8) * mm});
            skPoint(sketch, "E611.visualSharp", {"position": v(-5.16, 964.8) * mm});
            skArc(sketch, "E611.filletArc", {"start": v(-5.16, 961.8) * mm, "mid": v(-6.03, 963.92) * mm, "end": v(-8.16, 964.8) * mm});
            skPoint(sketch, "E612.visualSharp", {"position": v(-21.16, 949.8) * mm});
            skLineSegment(sketch, "E613.bottom", {"start": v(-8.16, 925.8) * mm, "end": v(-18.16, 925.8) * mm});
            skLineSegment(sketch, "E613.top", {"start": v(-8.16, 904.8) * mm, "end": v(-18.16, 904.8) * mm});
            skLineSegment(sketch, "E613.left", {"start": v(-5.16, 922.8) * mm, "end": v(-5.16, 907.8) * mm});
            skLineSegment(sketch, "E613.right", {"start": v(-21.16, 922.8) * mm, "end": v(-21.16, 907.8) * mm});
            skPoint(sketch, "E614.visualSharp", {"position": v(-21.16, 925.8) * mm});
            skArc(sketch, "E614.filletArc", {"start": v(-18.16, 925.8) * mm, "mid": v(-20.28, 924.92) * mm, "end": v(-21.16, 922.8) * mm});
            skPoint(sketch, "E615.visualSharp", {"position": v(-21.16, 904.8) * mm});
            skArc(sketch, "E615.filletArc", {"start": v(-21.16, 907.8) * mm, "mid": v(-20.28, 905.68) * mm, "end": v(-18.16, 904.8) * mm});
            skPoint(sketch, "E616.visualSharp", {"position": v(-5.16, 904.8) * mm});
            skArc(sketch, "E616.filletArc", {"start": v(-8.16, 904.8) * mm, "mid": v(-6.03, 905.68) * mm, "end": v(-5.16, 907.8) * mm});
            skPoint(sketch, "E617.visualSharp", {"position": v(-5.16, 925.8) * mm});
            skArc(sketch, "E617.filletArc", {"start": v(-5.16, 922.8) * mm, "mid": v(-6.03, 924.92) * mm, "end": v(-8.16, 925.8) * mm});
            skLineSegment(sketch, "E618", {"start": v(-35.16, 919.8) * mm, "end": v(-35.16, 869.8) * mm, "construction": true});
            skLineSegment(sketch, "E619", {"start": v(-35.16, 869.8) * mm, "end": v(-35.16, 847.8) * mm});
            skLineSegment(sketch, "E620", {"start": v(-35.16, 847.8) * mm, "end": v(-32.16, 847.8) * mm});
            skLineSegment(sketch, "E621", {"start": v(-32.16, 847.8) * mm, "end": v(-32.16, 869.8) * mm});
            skLineSegment(sketch, "E622", {"start": v(-32.16, 869.8) * mm, "end": v(-35.16, 869.8) * mm});
            skLineSegment(sketch, "E623.MirrorCS", {"start": v(8.84, 869.8) * mm, "end": v(8.84, 847.8) * mm});
            skLineSegment(sketch, "E624.MirrorCS", {"start": v(5.84, 847.8) * mm, "end": v(5.84, 869.8) * mm});
            skLineSegment(sketch, "E625.MirrorCS", {"start": v(-13.16, 863.68) * mm, "end": v(11.84, 863.68) * mm, "construction": true});
            skLineSegment(sketch, "E626.MirrorCS", {"start": v(5.84, 869.8) * mm, "end": v(8.84, 869.8) * mm});
            skLineSegment(sketch, "E627.MirrorCS", {"start": v(8.84, 919.8) * mm, "end": v(8.84, 869.8) * mm, "construction": true});
            skLineSegment(sketch, "E628.MirrorCS", {"start": v(8.84, 847.8) * mm, "end": v(5.84, 847.8) * mm});
            skLineSegment(sketch, "E629", {"start": v(-32.16, 858.8) * mm, "end": v(5.84, 858.8) * mm, "construction": true});
            skLineSegment(sketch, "E630", {"start": v(-13.16, 987.8) * mm, "end": v(-23.16, 987.8) * mm});
            skLineSegment(sketch, "E631", {"start": v(-25.16, 989.8) * mm, "end": v(-25.16, 991.8) * mm});
            skLineSegment(sketch, "E632", {"start": v(-23.16, 993.8) * mm, "end": v(-13.16, 993.8) * mm});
            skPoint(sketch, "E633.0.visualSharp", {"position": v(-25.16, 993.8) * mm});
            skArc(sketch, "E633.0.filletArc", {"start": v(-23.16, 993.8) * mm, "mid": v(-24.57, 993.21) * mm, "end": v(-25.16, 991.8) * mm});
            skPoint(sketch, "E634.0.visualSharp", {"position": v(-25.16, 987.8) * mm});
            skArc(sketch, "E634.0.filletArc", {"start": v(-25.16, 989.8) * mm, "mid": v(-24.57, 988.38) * mm, "end": v(-23.16, 987.8) * mm});
            skLineSegment(sketch, "E635.MirrorCS", {"start": v(-3.16, 993.8) * mm, "end": v(-13.16, 993.8) * mm});
            skLineSegment(sketch, "E636.MirrorCS", {"start": v(-13.16, 987.8) * mm, "end": v(-3.16, 987.8) * mm});
            skArc(sketch, "E637.MirrorCS", {"start": v(-1.16, 989.8) * mm, "mid": v(-1.74, 988.38) * mm, "end": v(-3.16, 987.8) * mm});
            skLineSegment(sketch, "E638.MirrorCS", {"start": v(-1.16, 989.8) * mm, "end": v(-1.16, 991.8) * mm});
            skArc(sketch, "E639.MirrorCS", {"start": v(-3.16, 993.8) * mm, "mid": v(-1.74, 993.21) * mm, "end": v(-1.16, 991.8) * mm});
            skLineSegment(sketch, "E640.MirrorCS", {"start": v(-25.16, 979.8) * mm, "end": v(-25.16, 977.8) * mm});
            skArc(sketch, "E641.MirrorCS", {"start": v(-23.16, 975.8) * mm, "mid": v(-24.57, 976.38) * mm, "end": v(-25.16, 977.8) * mm});
            skArc(sketch, "E642.MirrorCS", {"start": v(-25.16, 979.8) * mm, "mid": v(-24.57, 981.21) * mm, "end": v(-23.16, 981.8) * mm});
            skPoint(sketch, "E643.MirrorP", {"position": v(-25.16, 975.8) * mm});
            skPoint(sketch, "E644.MirrorP", {"position": v(-25.16, 981.8) * mm});
            skLineSegment(sketch, "E645.MirrorCS", {"start": v(-1.16, 979.8) * mm, "end": v(-1.16, 977.8) * mm});
            skLineSegment(sketch, "E646.MirrorCS", {"start": v(-3.16, 975.8) * mm, "end": v(-13.16, 975.8) * mm});
            skArc(sketch, "E647.MirrorCS", {"start": v(-1.16, 979.8) * mm, "mid": v(-1.74, 981.21) * mm, "end": v(-3.16, 981.8) * mm});
            skLineSegment(sketch, "E648.MirrorCS", {"start": v(-13.16, 981.8) * mm, "end": v(-3.16, 981.8) * mm});
            skArc(sketch, "E649.MirrorCS", {"start": v(-3.16, 975.8) * mm, "mid": v(-1.74, 976.38) * mm, "end": v(-1.16, 977.8) * mm});
            skLineSegment(sketch, "E650.MirrorCS", {"start": v(-13.16, 981.8) * mm, "end": v(-23.16, 981.8) * mm});
            skLineSegment(sketch, "E651.MirrorCS", {"start": v(-23.16, 975.8) * mm, "end": v(-13.16, 975.8) * mm});
            skLineSegment(sketch, "E652.MirrorCS", {"start": v(-25.16, 889.8) * mm, "end": v(-25.16, 891.8) * mm});
            skLineSegment(sketch, "E653.MirrorCS", {"start": v(-25.16, 879.8) * mm, "end": v(-25.16, 877.8) * mm});
            skArc(sketch, "E654.MirrorCS", {"start": v(-25.16, 879.8) * mm, "mid": v(-24.57, 881.21) * mm, "end": v(-23.16, 881.8) * mm});
            skArc(sketch, "E655.MirrorCS", {"start": v(-23.16, 875.8) * mm, "mid": v(-24.57, 876.38) * mm, "end": v(-25.16, 877.8) * mm});
            skArc(sketch, "E656.MirrorCS", {"start": v(-25.16, 889.8) * mm, "mid": v(-24.57, 888.38) * mm, "end": v(-23.16, 887.8) * mm});
            skArc(sketch, "E657.MirrorCS", {"start": v(-23.16, 893.8) * mm, "mid": v(-24.57, 893.21) * mm, "end": v(-25.16, 891.8) * mm});
            skArc(sketch, "E658.MirrorCS", {"start": v(-3.16, 875.8) * mm, "mid": v(-1.74, 876.38) * mm, "end": v(-1.16, 877.8) * mm});
            skArc(sketch, "E659.MirrorCS", {"start": v(-3.16, 893.8) * mm, "mid": v(-1.74, 893.21) * mm, "end": v(-1.16, 891.8) * mm});
            skArc(sketch, "E660.MirrorCS", {"start": v(-1.16, 879.8) * mm, "mid": v(-1.74, 881.21) * mm, "end": v(-3.16, 881.8) * mm});
            skLineSegment(sketch, "E661.MirrorCS", {"start": v(-1.16, 879.8) * mm, "end": v(-1.16, 877.8) * mm});
            skLineSegment(sketch, "E662.MirrorCS", {"start": v(-1.16, 889.8) * mm, "end": v(-1.16, 891.8) * mm});
            skArc(sketch, "E663.MirrorCS", {"start": v(-1.16, 889.8) * mm, "mid": v(-1.74, 888.38) * mm, "end": v(-3.16, 887.8) * mm});
            skPoint(sketch, "E664.MirrorP", {"position": v(-21.16, 871.8) * mm});
            skLineSegment(sketch, "E665.MirrorCS", {"start": v(-13.16, 881.8) * mm, "end": v(-3.16, 881.8) * mm});
            skLineSegment(sketch, "E666.MirrorCS", {"start": v(-13.16, 829.8) * mm, "end": v(-13.16, 1047.8) * mm, "construction": true});
            skPoint(sketch, "E667.MirrorP", {"position": v(-25.16, 893.8) * mm});
            skLineSegment(sketch, "E668.MirrorCS", {"start": v(-13.16, 881.8) * mm, "end": v(-23.16, 881.8) * mm});
            skLineSegment(sketch, "E669.MirrorCS", {"start": v(-23.16, 893.8) * mm, "end": v(-13.16, 893.8) * mm});
            skPoint(sketch, "E670.MirrorP", {"position": v(-5.16, 871.8) * mm});
            skPoint(sketch, "E671.MirrorP", {"position": v(-25.16, 875.8) * mm});
            skLineSegment(sketch, "E672.MirrorCS", {"start": v(-13.16, 887.8) * mm, "end": v(-23.16, 887.8) * mm});
            skLineSegment(sketch, "E673.MirrorCS", {"start": v(-3.16, 893.8) * mm, "end": v(-13.16, 893.8) * mm});
            skPoint(sketch, "E674.MirrorP", {"position": v(-25.16, 887.8) * mm});
            skLineSegment(sketch, "E675.MirrorCS", {"start": v(-13.16, 887.8) * mm, "end": v(-3.16, 887.8) * mm});
            skPoint(sketch, "E676.MirrorP", {"position": v(-25.16, 881.8) * mm});
            skLineSegment(sketch, "E677.MirrorCS", {"start": v(-3.16, 875.8) * mm, "end": v(-13.16, 875.8) * mm});
            skLineSegment(sketch, "E678.MirrorCS", {"start": v(-23.16, 875.8) * mm, "end": v(-13.16, 875.8) * mm});
            skLineSegment(sketch, "E679", {"start": v(-32.16, 941.8) * mm, "end": v(-32.16, 973.2) * mm, "construction": true});
            skLineSegment(sketch, "E680", {"start": v(-18.16, 964.8) * mm, "end": v(-26.16, 964.8) * mm});
            skLineSegment(sketch, "E681", {"start": v(-29.16, 961.8) * mm, "end": v(-29.16, 952.8) * mm});
            skLineSegment(sketch, "E682", {"start": v(-26.16, 949.8) * mm, "end": v(-18.16, 949.8) * mm});
            skPoint(sketch, "E683.0.visualSharp", {"position": v(-29.16, 964.8) * mm});
            skArc(sketch, "E683.0.filletArc", {"start": v(-26.16, 964.8) * mm, "mid": v(-28.28, 963.92) * mm, "end": v(-29.16, 961.8) * mm});
            skPoint(sketch, "E684.0.visualSharp", {"position": v(-29.16, 949.8) * mm});
            skArc(sketch, "E684.0.filletArc", {"start": v(-29.16, 952.8) * mm, "mid": v(-28.28, 950.68) * mm, "end": v(-26.16, 949.8) * mm});
            skSolve(sketch);
        }
        {
            var Q0;
            Q0 = qSketchRegion(id + "F0", true);
            extrude(context, id + "F1", {"entities" : qUnion([Q0]), "depth" : 3 * mm});
        }
        {
            var Q0;
            Q0=qCreatedBy(makeId("Top.planeOp"),FACE);
            var sketch = newSketch(context, id + "F2", { "sketchPlane" : qUnion([Q0])});
            skPoint(sketch, "E685.endSnap0", {"position": v(266.81, -34.49) * mm});
            skLineSegment(sketch, "E686.MirrorCS", {"start": v(269.81, 70.51) * mm, "end": v(272.81, 70.51) * mm});
            skLineSegment(sketch, "E687.MirrorCS", {"start": v(272.81, 92.51) * mm, "end": v(269.81, 92.51) * mm});
            skLineSegment(sketch, "E688.MirrorCS", {"start": v(272.81, 102.51) * mm, "end": v(272.81, 92.51) * mm});
            skLineSegment(sketch, "E689.MirrorCS", {"start": v(272.81, 102.51) * mm, "end": v(317.81, 102.51) * mm});
            skLineSegment(sketch, "E690.MirrorCS", {"start": v(317.81, 102.51) * mm, "end": v(317.81, 92.51) * mm});
            skLineSegment(sketch, "E691.MirrorCS", {"start": v(320.81, 92.51) * mm, "end": v(320.81, 70.51) * mm});
            skLineSegment(sketch, "E692.MirrorCS", {"start": v(317.81, 92.51) * mm, "end": v(320.81, 92.51) * mm});
            skLineSegment(sketch, "E693.MirrorCS", {"start": v(320.81, 70.51) * mm, "end": v(317.81, 70.51) * mm});
            skLineSegment(sketch, "E694.MirrorCS", {"start": v(317.81, 70.51) * mm, "end": v(317.81, 52.25) * mm});
            skLineSegment(sketch, "E695.MirrorCS", {"start": v(286.31, 95.51) * mm, "end": v(304.31, 95.51) * mm});
            skArc(sketch, "E696.MirrorCS", {"start": v(304.31, 95.51) * mm, "mid": v(307.14, 94.34) * mm, "end": v(308.31, 91.51) * mm});
            skLineSegment(sketch, "E697.MirrorCS", {"start": v(308.31, 91.51) * mm, "end": v(308.31, 69.51) * mm});
            skArc(sketch, "E698.MirrorCS", {"start": v(308.31, 69.51) * mm, "mid": v(307.14, 66.68) * mm, "end": v(304.31, 65.51) * mm});
            skLineSegment(sketch, "E699.MirrorCS", {"start": v(286.31, 65.51) * mm, "end": v(304.31, 65.51) * mm});
            skArc(sketch, "E700.MirrorCS", {"start": v(286.31, 65.51) * mm, "mid": v(283.48, 66.68) * mm, "end": v(282.31, 69.51) * mm});
            skLineSegment(sketch, "E701.MirrorCS", {"start": v(282.31, 91.51) * mm, "end": v(282.31, 69.51) * mm});
            skArc(sketch, "E702.MirrorCS", {"start": v(282.31, 91.51) * mm, "mid": v(283.48, 94.34) * mm, "end": v(286.31, 95.51) * mm});
            skLineSegment(sketch, "E703.MirrorCS", {"start": v(272.81, 70.51) * mm, "end": v(272.81, 12.51) * mm});
            skLineSegment(sketch, "E704.MirrorCS", {"start": v(313.31, 52.25) * mm, "end": v(317.81, 52.25) * mm});
            skLineSegment(sketch, "E705.MirrorCS", {"start": v(313.31, 52.25) * mm, "end": v(310.81, 52.25) * mm});
            skLineSegment(sketch, "E706.MirrorCS", {"start": v(310.81, 52.25) * mm, "end": v(310.81, 48.25) * mm});
            skLineSegment(sketch, "E707.MirrorCS", {"start": v(310.81, 48.25) * mm, "end": v(313.31, 48.25) * mm});
            skLineSegment(sketch, "E708.MirrorCS", {"start": v(313.31, 48.25) * mm, "end": v(317.81, 48.25) * mm});
            skLineSegment(sketch, "E709.MirrorCS", {"start": v(304.31, 44.31) * mm, "end": v(286.31, 44.31) * mm});
            skArc(sketch, "E710.MirrorCS", {"start": v(304.31, 44.31) * mm, "mid": v(307.14, 43.14) * mm, "end": v(308.31, 40.31) * mm});
            skLineSegment(sketch, "E711.MirrorCS", {"start": v(308.31, 40.31) * mm, "end": v(308.31, 32.51) * mm});
            skArc(sketch, "E712.MirrorCS", {"start": v(308.31, 32.51) * mm, "mid": v(307.14, 29.68) * mm, "end": v(304.31, 28.51) * mm});
            skLineSegment(sketch, "E713.MirrorCS", {"start": v(286.31, 28.51) * mm, "end": v(304.31, 28.51) * mm});
            skArc(sketch, "E714.MirrorCS", {"start": v(286.31, 28.51) * mm, "mid": v(283.48, 29.68) * mm, "end": v(282.31, 32.51) * mm});
            skLineSegment(sketch, "E715.MirrorCS", {"start": v(282.31, 40.31) * mm, "end": v(282.31, 32.51) * mm});
            skArc(sketch, "E716.MirrorCS", {"start": v(282.31, 40.31) * mm, "mid": v(283.48, 43.14) * mm, "end": v(286.31, 44.31) * mm});
            skLineSegment(sketch, "E717.MirrorCS", {"start": v(317.81, 48.25) * mm, "end": v(317.81, 12.51) * mm});
            skLineSegment(sketch, "E718.MirrorCS", {"start": v(317.81, 12.51) * mm, "end": v(320.81, 12.51) * mm});
            skLineSegment(sketch, "E719.MirrorCS", {"start": v(272.81, 12.51) * mm, "end": v(269.81, 12.51) * mm});
            skLineSegment(sketch, "E720.MirrorCS", {"start": v(286.31, 21.51) * mm, "end": v(304.31, 21.51) * mm});
            skArc(sketch, "E721.MirrorCS", {"start": v(304.31, 21.51) * mm, "mid": v(307.14, 20.34) * mm, "end": v(308.31, 17.51) * mm});
            skLineSegment(sketch, "E722.MirrorCS", {"start": v(308.31, 17.51) * mm, "end": v(308.31, -4.49) * mm});
            skArc(sketch, "E723.MirrorCS", {"start": v(308.31, -4.49) * mm, "mid": v(307.14, -7.32) * mm, "end": v(304.31, -8.49) * mm});
            skLineSegment(sketch, "E724.MirrorCS", {"start": v(286.31, -8.49) * mm, "end": v(304.31, -8.49) * mm});
            skArc(sketch, "E725.MirrorCS", {"start": v(286.31, -8.49) * mm, "mid": v(283.48, -7.32) * mm, "end": v(282.31, -4.49) * mm});
            skLineSegment(sketch, "E726.MirrorCS", {"start": v(282.31, 17.51) * mm, "end": v(282.31, -4.49) * mm});
            skArc(sketch, "E727.MirrorCS", {"start": v(282.31, 17.51) * mm, "mid": v(283.48, 20.34) * mm, "end": v(286.31, 21.51) * mm});
            skLineSegment(sketch, "E728.MirrorCS", {"start": v(317.81, -9.49) * mm, "end": v(317.81, -53.07) * mm});
            skLineSegment(sketch, "E729.MirrorCS", {"start": v(272.81, -9.49) * mm, "end": v(272.81, -59.49) * mm});
            skLineSegment(sketch, "E730.MirrorCS", {"start": v(269.81, -9.49) * mm, "end": v(272.81, -9.49) * mm});
            skLineSegment(sketch, "E731.MirrorCS", {"start": v(320.81, -9.49) * mm, "end": v(317.81, -9.49) * mm});
            skLineSegment(sketch, "E732.MirrorCS", {"start": v(320.81, 12.51) * mm, "end": v(320.81, -9.49) * mm});
            skLineSegment(sketch, "E733.MirrorCS", {"start": v(286.31, -15.49) * mm, "end": v(304.31, -15.49) * mm});
            skArc(sketch, "E734.MirrorCS", {"start": v(304.31, -15.49) * mm, "mid": v(307.14, -16.66) * mm, "end": v(308.31, -19.49) * mm});
            skLineSegment(sketch, "E735.MirrorCS", {"start": v(308.31, -19.49) * mm, "end": v(308.31, -41.49) * mm});
            skArc(sketch, "E736.MirrorCS", {"start": v(308.31, -41.49) * mm, "mid": v(307.14, -44.32) * mm, "end": v(304.31, -45.49) * mm});
            skLineSegment(sketch, "E737.MirrorCS", {"start": v(286.31, -45.49) * mm, "end": v(304.31, -45.49) * mm});
            skLineSegment(sketch, "E738.MirrorCS", {"start": v(282.31, -19.49) * mm, "end": v(282.31, -41.49) * mm});
            skArc(sketch, "E739.MirrorCS", {"start": v(286.31, -45.49) * mm, "mid": v(283.48, -44.32) * mm, "end": v(282.31, -41.49) * mm});
            skArc(sketch, "E740.MirrorCS", {"start": v(282.31, -19.49) * mm, "mid": v(283.48, -16.66) * mm, "end": v(286.31, -15.49) * mm});
            skLineSegment(sketch, "E741.MirrorCS", {"start": v(310.81, -53.07) * mm, "end": v(310.81, -57.07) * mm});
            skLineSegment(sketch, "E742.MirrorCS", {"start": v(310.81, -57.07) * mm, "end": v(317.81, -57.07) * mm});
            skLineSegment(sketch, "E743.MirrorCS", {"start": v(317.81, -57.07) * mm, "end": v(317.81, -59.49) * mm});
            skLineSegment(sketch, "E744.MirrorCS", {"start": v(312.7, -59.49) * mm, "end": v(317.81, -59.49) * mm});
            skLineSegment(sketch, "E745.MirrorCS", {"start": v(312.7, -59.49) * mm, "end": v(308.26, -59.49) * mm});
            skFitSpline(sketch, "E746.MirrorCS", {"points": [v(308.26, -59.49) * mm, v(306.77, -58.62) * mm, v(305.57, -56.33) * mm], "startDerivative": vector(-3.58, 1.42) * mm, "endDerivative": vector(-1.86, 4.79) * mm});
            skArc(sketch, "E747.MirrorCS", {"start": v(301.68, -53.49) * mm, "mid": v(304.1, -54.26) * mm, "end": v(305.57, -56.33) * mm});
            skLineSegment(sketch, "E748.MirrorCS", {"start": v(295.31, -53.49) * mm, "end": v(285.32, -53.49) * mm});
            skLineSegment(sketch, "E749.MirrorCS", {"start": v(295.31, -53.49) * mm, "end": v(301.79, -53.49) * mm});
            skArc(sketch, "E750.MirrorCS", {"start": v(281.8, -55.6) * mm, "mid": v(283.27, -54.06) * mm, "end": v(285.32, -53.49) * mm});
            skLineSegment(sketch, "E751.MirrorCS", {"start": v(281.8, -55.6) * mm, "end": v(280.57, -57.9) * mm});
            skArc(sketch, "E752.MirrorCS", {"start": v(277.92, -59.49) * mm, "mid": v(279.47, -59.06) * mm, "end": v(280.57, -57.9) * mm});
            skLineSegment(sketch, "E753.MirrorCS", {"start": v(272.81, -59.49) * mm, "end": v(277.92, -59.49) * mm});
            skLineSegment(sketch, "E754", {"start": v(310.81, -53.07) * mm, "end": v(317.81, -53.07) * mm});
            skLineSegment(sketch, "E755", {"start": v(269.81, 12.51) * mm, "end": v(269.81, -9.49) * mm});
            skLineSegment(sketch, "E756", {"start": v(269.81, 92.51) * mm, "end": v(269.81, 70.51) * mm});
            skLineSegment(sketch, "E757.bottom", {"start": v(287.44, 675.43) * mm, "end": v(242.44, 675.43) * mm});
            skLineSegment(sketch, "E757.left", {"start": v(287.44, 675.43) * mm, "end": v(287.44, 665.43) * mm});
            skLineSegment(sketch, "E757.right", {"start": v(242.44, 675.43) * mm, "end": v(242.44, 665.43) * mm});
            skLineSegment(sketch, "E758.MirrorCS", {"start": v(287.44, 665.43) * mm, "end": v(293.44, 665.43) * mm});
            skLineSegment(sketch, "E759.MirrorCS", {"start": v(293.44, 643.43) * mm, "end": v(287.44, 643.43) * mm});
            skLineSegment(sketch, "E760.trimOffspring", {"start": v(287.44, 643.43) * mm, "end": v(287.44, 585.43) * mm});
            skLineSegment(sketch, "E761", {"start": v(293.44, 665.43) * mm, "end": v(293.44, 643.43) * mm});
            skLineSegment(sketch, "E762", {"start": v(242.44, 585.43) * mm, "end": v(242.44, 643.43) * mm});
            skLineSegment(sketch, "E763", {"start": v(242.44, 665.43) * mm, "end": v(211.44, 665.43) * mm});
            skLineSegment(sketch, "E764", {"start": v(211.44, 665.43) * mm, "end": v(211.44, 660.43) * mm});
            skLineSegment(sketch, "E765", {"start": v(211.44, 660.43) * mm, "end": v(208.44, 660.43) * mm});
            skLineSegment(sketch, "E766", {"start": v(208.44, 660.43) * mm, "end": v(208.44, 648.43) * mm});
            skLineSegment(sketch, "E767", {"start": v(208.44, 648.43) * mm, "end": v(211.44, 648.43) * mm});
            skLineSegment(sketch, "E768", {"start": v(242.44, 643.43) * mm, "end": v(211.44, 643.43) * mm});
            skLineSegment(sketch, "E769", {"start": v(211.44, 648.43) * mm, "end": v(211.44, 643.43) * mm});
            skLineSegment(sketch, "E770", {"start": v(242.44, 585.43) * mm, "end": v(211.44, 585.43) * mm});
            skLineSegment(sketch, "E771", {"start": v(211.44, 585.43) * mm, "end": v(211.44, 580.43) * mm});
            skLineSegment(sketch, "E772", {"start": v(211.44, 580.43) * mm, "end": v(208.44, 580.43) * mm});
            skLineSegment(sketch, "E773", {"start": v(208.44, 580.43) * mm, "end": v(208.44, 568.43) * mm});
            skLineSegment(sketch, "E774", {"start": v(208.44, 568.43) * mm, "end": v(211.44, 568.43) * mm});
            skLineSegment(sketch, "E775", {"start": v(242.44, 563.43) * mm, "end": v(211.44, 563.43) * mm});
            skLineSegment(sketch, "E776", {"start": v(211.44, 568.43) * mm, "end": v(211.44, 563.43) * mm});
            skLineSegment(sketch, "E777", {"start": v(242.44, 513.43) * mm, "end": v(211.44, 513.43) * mm});
            skLineSegment(sketch, "E778", {"start": v(211.44, 513.43) * mm, "end": v(211.44, 508.43) * mm});
            skLineSegment(sketch, "E779", {"start": v(211.44, 508.43) * mm, "end": v(208.44, 508.43) * mm});
            skLineSegment(sketch, "E780", {"start": v(208.44, 508.43) * mm, "end": v(208.44, 496.43) * mm});
            skLineSegment(sketch, "E781", {"start": v(208.44, 496.43) * mm, "end": v(211.44, 496.43) * mm});
            skLineSegment(sketch, "E782", {"start": v(242.44, 491.43) * mm, "end": v(211.44, 491.43) * mm});
            skLineSegment(sketch, "E783", {"start": v(211.44, 496.43) * mm, "end": v(211.44, 491.43) * mm});
            skLineSegment(sketch, "E784", {"start": v(242.44, 491.43) * mm, "end": v(242.44, 483.43) * mm});
            skLineSegment(sketch, "E785", {"start": v(242.44, 513.43) * mm, "end": v(242.44, 563.43) * mm});
            skLineSegment(sketch, "E786", {"start": v(242.44, 483.43) * mm, "end": v(252.44, 483.43) * mm});
            skLineSegment(sketch, "E787", {"start": v(287.44, 563.19) * mm, "end": v(287.44, 518.43) * mm});
            skPoint(sketch, "E788.0.visualSharp", {"position": v(287.44, 483.43) * mm});
            skArc(sketch, "E788.0.filletArc", {"start": v(252.44, 483.43) * mm, "mid": v(277.18, 493.68) * mm, "end": v(287.44, 518.43) * mm});
            skLineSegment(sketch, "E789", {"start": v(214.44, 503.93) * mm, "end": v(236.44, 503.93) * mm});
            skLineSegment(sketch, "E790", {"start": v(236.44, 503.93) * mm, "end": v(236.44, 500.93) * mm});
            skLineSegment(sketch, "E791", {"start": v(236.44, 500.93) * mm, "end": v(214.44, 500.93) * mm});
            skLineSegment(sketch, "E792", {"start": v(214.44, 500.93) * mm, "end": v(214.44, 503.93) * mm});
            skLineSegment(sketch, "E793", {"start": v(214.44, 503.93) * mm, "end": v(214.44, 513.43) * mm, "construction": true});
            skLineSegment(sketch, "E794", {"start": v(208.44, 500.93) * mm, "end": v(214.44, 500.93) * mm, "construction": true});
            skLineSegment(sketch, "E795", {"start": v(214.44, 500.93) * mm, "end": v(214.44, 491.43) * mm, "construction": true});
            skLineSegment(sketch, "E796", {"start": v(242.44, 513.43) * mm, "end": v(242.44, 491.43) * mm, "construction": true});
            skLineSegment(sketch, "E797", {"start": v(236.44, 500.93) * mm, "end": v(242.44, 500.93) * mm, "construction": true});
            skLineSegment(sketch, "E798", {"start": v(252.44, 518.43) * mm, "end": v(277.18, 493.68) * mm, "construction": true});
            skCircle(sketch, "E799", {"center": v(264.8, 506.05) * mm, "radius": 10.5 * mm});
            skLineSegment(sketch, "E800", {"start": v(242.44, 665.43) * mm, "end": v(242.44, 643.43) * mm, "construction": true});
            skLineSegment(sketch, "E801", {"start": v(287.44, 665.43) * mm, "end": v(287.44, 643.43) * mm, "construction": true});
            skPoint(sketch, "E802.orphan", {"position": v(242.44, 654.43) * mm});
            skLineSegment(sketch, "E803", {"start": v(248.94, 574.49) * mm, "end": v(202.7, 574.49) * mm, "construction": true});
            skLineSegment(sketch, "E804", {"start": v(287.44, 585.43) * mm, "end": v(292.65, 585.43) * mm});
            skLineSegment(sketch, "E805", {"start": v(292.65, 585.43) * mm, "end": v(292.65, 563.19) * mm});
            skLineSegment(sketch, "E806", {"start": v(287.44, 563.19) * mm, "end": v(292.65, 563.19) * mm});
            skLineSegment(sketch, "E807", {"start": v(278.07, 675.43) * mm, "end": v(278.07, 643.43) * mm, "construction": true});
            skLineSegment(sketch, "E808", {"start": v(287.44, 665.43) * mm, "end": v(242.44, 665.43) * mm, "construction": true});
            skLineSegment(sketch, "E809", {"start": v(287.44, 643.43) * mm, "end": v(278.07, 643.43) * mm, "construction": true});
            skLineSegment(sketch, "E810.trimOffspring", {"start": v(248.94, 643.43) * mm, "end": v(242.44, 643.43) * mm, "construction": true});
            skLineSegment(sketch, "E811", {"start": v(276.07, 643.43) * mm, "end": v(255.72, 643.43) * mm});
            skLineSegment(sketch, "E812", {"start": v(254.64, 639.74) * mm, "end": v(274.99, 626.62) * mm});
            skLineSegment(sketch, "E813", {"start": v(278.07, 628.3) * mm, "end": v(278.07, 641.43) * mm});
            skPoint(sketch, "E814.0.visualSharp", {"position": v(248.94, 643.43) * mm});
            skArc(sketch, "E814.0.filletArc", {"start": v(255.72, 643.43) * mm, "mid": v(253.8, 642) * mm, "end": v(254.64, 639.74) * mm});
            skPoint(sketch, "E815.0.visualSharp", {"position": v(278.07, 643.43) * mm});
            skArc(sketch, "E815.0.filletArc", {"start": v(278.07, 641.43) * mm, "mid": v(277.48, 642.84) * mm, "end": v(276.07, 643.43) * mm});
            skPoint(sketch, "E816.0.visualSharp", {"position": v(278.07, 624.63) * mm});
            skArc(sketch, "E816.0.filletArc", {"start": v(274.99, 626.62) * mm, "mid": v(277.03, 626.54) * mm, "end": v(278.07, 628.3) * mm});
            skLineSegment(sketch, "E817", {"start": v(242.44, 585.43) * mm, "end": v(248.94, 585.43) * mm, "construction": true});
            skLineSegment(sketch, "E818", {"start": v(278.07, 585.43) * mm, "end": v(287.44, 585.43) * mm, "construction": true});
            skLineSegment(sketch, "E819", {"start": v(255.72, 585.43) * mm, "end": v(276.07, 585.43) * mm});
            skLineSegment(sketch, "E820", {"start": v(254.64, 589.1) * mm, "end": v(274.99, 602.23) * mm});
            skLineSegment(sketch, "E821", {"start": v(278.07, 587.43) * mm, "end": v(278.07, 600.55) * mm});
            skPoint(sketch, "E822.0.visualSharp", {"position": v(278.07, 604.22) * mm});
            skArc(sketch, "E822.0.filletArc", {"start": v(278.07, 600.55) * mm, "mid": v(277.03, 602.3) * mm, "end": v(274.99, 602.23) * mm});
            skPoint(sketch, "E823.0.visualSharp", {"position": v(248.94, 585.43) * mm});
            skArc(sketch, "E823.0.filletArc", {"start": v(254.64, 589.1) * mm, "mid": v(253.8, 586.86) * mm, "end": v(255.72, 585.43) * mm});
            skPoint(sketch, "E824.0.visualSharp", {"position": v(278.07, 585.43) * mm});
            skArc(sketch, "E824.0.filletArc", {"start": v(276.07, 585.43) * mm, "mid": v(277.48, 586.01) * mm, "end": v(278.07, 587.43) * mm});
            skLineSegment(sketch, "E825", {"start": v(278.07, 604.22) * mm, "end": v(278.07, 624.63) * mm, "construction": true});
            skLineSegment(sketch, "E826", {"start": v(278.07, 614.43) * mm, "end": v(248.94, 614.43) * mm, "construction": true});
            skLineSegment(sketch, "E827", {"start": v(252.02, 631.23) * mm, "end": v(275.47, 616.1) * mm});
            skLineSegment(sketch, "E828", {"start": v(275.47, 612.74) * mm, "end": v(252.02, 597.62) * mm});
            skLineSegment(sketch, "E829.trimOffspring", {"start": v(248.94, 633.22) * mm, "end": v(248.94, 675.43) * mm, "construction": true});
            skLineSegment(sketch, "E830", {"start": v(248.94, 599.3) * mm, "end": v(248.94, 629.55) * mm});
            skPoint(sketch, "E831.0.visualSharp", {"position": v(248.94, 633.22) * mm});
            skArc(sketch, "E831.0.filletArc", {"start": v(252.02, 631.23) * mm, "mid": v(249.98, 631.3) * mm, "end": v(248.94, 629.55) * mm});
            skPoint(sketch, "E832.0.visualSharp", {"position": v(278.07, 614.43) * mm});
            skArc(sketch, "E832.0.filletArc", {"start": v(275.47, 612.74) * mm, "mid": v(276.38, 614.43) * mm, "end": v(275.47, 616.1) * mm});
            skPoint(sketch, "E833.0.visualSharp", {"position": v(248.94, 595.63) * mm});
            skArc(sketch, "E833.0.filletArc", {"start": v(248.94, 599.3) * mm, "mid": v(249.98, 597.54) * mm, "end": v(252.02, 597.62) * mm});
            skLineSegment(sketch, "E834.MirrorCS", {"start": v(242.44, 563.55) * mm, "end": v(248.94, 563.55) * mm, "construction": true});
            skArc(sketch, "E835.MirrorCS", {"start": v(248.94, 549.67) * mm, "mid": v(249.98, 551.43) * mm, "end": v(252.02, 551.35) * mm});
            skArc(sketch, "E836.MirrorCS", {"start": v(252.02, 517.74) * mm, "mid": v(249.98, 517.67) * mm, "end": v(248.94, 519.42) * mm});
            skArc(sketch, "E837.MirrorCS", {"start": v(276.07, 563.55) * mm, "mid": v(277.48, 562.96) * mm, "end": v(278.07, 561.55) * mm});
            skArc(sketch, "E838.MirrorCS", {"start": v(275.47, 536.23) * mm, "mid": v(276.38, 534.55) * mm, "end": v(275.47, 532.87) * mm});
            skArc(sketch, "E839.MirrorCS", {"start": v(278.07, 548.42) * mm, "mid": v(277.03, 546.67) * mm, "end": v(274.99, 546.74) * mm});
            skLineSegment(sketch, "E840.MirrorCS", {"start": v(248.94, 505.55) * mm, "end": v(242.44, 505.55) * mm, "construction": true});
            skPoint(sketch, "E841.MirrorP", {"position": v(248.94, 505.55) * mm});
            skPoint(sketch, "E842.MirrorP", {"position": v(248.94, 515.75) * mm});
            skPoint(sketch, "E843.MirrorP", {"position": v(278.07, 563.55) * mm});
            skLineSegment(sketch, "E844.MirrorCS", {"start": v(252.02, 517.74) * mm, "end": v(275.47, 532.87) * mm});
            skPoint(sketch, "E845.MirrorP", {"position": v(278.07, 524.34) * mm});
            skLineSegment(sketch, "E846.MirrorCS", {"start": v(255.72, 563.55) * mm, "end": v(276.07, 563.55) * mm});
            skArc(sketch, "E847.MirrorCS", {"start": v(254.64, 559.87) * mm, "mid": v(253.8, 562.11) * mm, "end": v(255.72, 563.55) * mm});
            skLineSegment(sketch, "E848.MirrorCS", {"start": v(248.94, 515.75) * mm, "end": v(248.94, 473.55) * mm, "construction": true});
            skPoint(sketch, "E849.MirrorP", {"position": v(278.07, 544.75) * mm});
            skLineSegment(sketch, "E850.MirrorCS", {"start": v(278.07, 473.55) * mm, "end": v(278.07, 505.55) * mm, "construction": true});
            skLineSegment(sketch, "E851.MirrorCS", {"start": v(278.07, 561.55) * mm, "end": v(278.07, 548.42) * mm});
            skPoint(sketch, "E852.MirrorP", {"position": v(248.94, 553.34) * mm});
            skLineSegment(sketch, "E853.MirrorCS", {"start": v(278.07, 534.55) * mm, "end": v(248.94, 534.55) * mm, "construction": true});
            skLineSegment(sketch, "E854.MirrorCS", {"start": v(248.94, 549.67) * mm, "end": v(248.94, 519.42) * mm});
            skPoint(sketch, "E855.MirrorP", {"position": v(278.07, 505.55) * mm});
            skLineSegment(sketch, "E856.MirrorCS", {"start": v(278.07, 563.55) * mm, "end": v(287.44, 563.55) * mm, "construction": true});
            skPoint(sketch, "E857.MirrorP", {"position": v(248.94, 563.55) * mm});
            skLineSegment(sketch, "E858.MirrorCS", {"start": v(254.64, 559.87) * mm, "end": v(274.99, 546.74) * mm});
            skLineSegment(sketch, "E859.MirrorCS", {"start": v(278.07, 544.75) * mm, "end": v(278.07, 524.34) * mm, "construction": true});
            skLineSegment(sketch, "E860.MirrorCS", {"start": v(287.44, 505.55) * mm, "end": v(278.07, 505.55) * mm, "construction": true});
            skLineSegment(sketch, "E861.MirrorCS", {"start": v(275.47, 536.23) * mm, "end": v(252.02, 551.35) * mm});
            skPoint(sketch, "E862.MirrorP", {"position": v(278.07, 534.55) * mm});
            skLineSegment(sketch, "E863", {"start": v(232.99, 455.91) * mm, "end": v(210.99, 455.91) * mm});
            skLineSegment(sketch, "E864", {"start": v(210.99, 455.91) * mm, "end": v(210.99, 452.91) * mm});
            skLineSegment(sketch, "E865", {"start": v(210.99, 452.91) * mm, "end": v(207.99, 452.91) * mm});
            skLineSegment(sketch, "E866", {"start": v(207.99, 452.91) * mm, "end": v(207.99, 443.91) * mm});
            skLineSegment(sketch, "E867", {"start": v(232.99, 452.91) * mm, "end": v(232.99, 455.91) * mm});
            skLineSegment(sketch, "E868", {"start": v(238.99, 443.91) * mm, "end": v(238.99, 433.91) * mm});
            skLineSegment(sketch, "E869", {"start": v(238.99, 433.91) * mm, "end": v(207.99, 433.91) * mm, "construction": true});
            skLineSegment(sketch, "E870", {"start": v(207.99, 443.91) * mm, "end": v(204.7, 443.91) * mm});
            skLineSegment(sketch, "E871", {"start": v(204.7, 443.91) * mm, "end": v(204.7, 433.91) * mm});
            skLineSegment(sketch, "E872", {"start": v(207.99, 433.91) * mm, "end": v(204.7, 433.91) * mm, "construction": true});
            skLineSegment(sketch, "E873.MirrorCS", {"start": v(207.99, 423.91) * mm, "end": v(204.7, 423.91) * mm});
            skLineSegment(sketch, "E874.MirrorCS", {"start": v(232.99, 414.91) * mm, "end": v(232.99, 411.91) * mm});
            skLineSegment(sketch, "E875.MirrorCS", {"start": v(238.99, 423.91) * mm, "end": v(238.99, 433.91) * mm});
            skLineSegment(sketch, "E876.MirrorCS", {"start": v(210.99, 411.91) * mm, "end": v(210.99, 414.91) * mm});
            skLineSegment(sketch, "E877.MirrorCS", {"start": v(204.7, 423.91) * mm, "end": v(204.7, 433.91) * mm});
            skLineSegment(sketch, "E878.MirrorCS", {"start": v(232.99, 411.91) * mm, "end": v(210.99, 411.91) * mm});
            skLineSegment(sketch, "E879.MirrorCS", {"start": v(210.99, 414.91) * mm, "end": v(207.99, 414.91) * mm});
            skLineSegment(sketch, "E880.MirrorCS", {"start": v(207.99, 414.91) * mm, "end": v(207.99, 423.91) * mm});
            skLineSegment(sketch, "E881", {"start": v(221.99, 455.91) * mm, "end": v(221.99, 411.91) * mm, "construction": true});
            skCircle(sketch, "E882", {"center": v(221.99, 433.91) * mm, "radius": 11 * mm});
            skLineSegment(sketch, "E883", {"start": v(159.84, 675.73) * mm, "end": v(134.84, 675.73) * mm});
            skLineSegment(sketch, "E884.bottom", {"start": v(139.84, 675.73) * mm, "end": v(179.84, 675.73) * mm});
            skPoint(sketch, "E885.visualSharp", {"position": v(134.84, 675.73) * mm});
            skArc(sketch, "E885.filletArc", {"start": v(139.84, 675.73) * mm, "mid": v(136.3, 674.26) * mm, "end": v(134.84, 670.73) * mm});
            skPoint(sketch, "E886.visualSharp", {"position": v(184.84, 675.73) * mm});
            skArc(sketch, "E886.filletArc", {"start": v(184.84, 670.73) * mm, "mid": v(183.38, 674.27) * mm, "end": v(179.84, 675.73) * mm});
            skLineSegment(sketch, "E887", {"start": v(137.84, 660.73) * mm, "end": v(137.84, 648.73) * mm});
            skLineSegment(sketch, "E888", {"start": v(137.84, 648.73) * mm, "end": v(140.84, 648.73) * mm});
            skLineSegment(sketch, "E889", {"start": v(140.84, 648.73) * mm, "end": v(140.84, 660.73) * mm});
            skLineSegment(sketch, "E890", {"start": v(140.84, 660.73) * mm, "end": v(137.84, 660.73) * mm});
            skLineSegment(sketch, "E891", {"start": v(137.84, 580.73) * mm, "end": v(137.84, 568.73) * mm});
            skLineSegment(sketch, "E892", {"start": v(137.84, 568.73) * mm, "end": v(140.84, 568.73) * mm});
            skLineSegment(sketch, "E893", {"start": v(140.84, 568.73) * mm, "end": v(140.84, 580.73) * mm});
            skLineSegment(sketch, "E894", {"start": v(140.84, 580.73) * mm, "end": v(137.84, 580.73) * mm});
            skLineSegment(sketch, "E895", {"start": v(134.84, 670.73) * mm, "end": v(134.84, 483.73) * mm});
            skLineSegment(sketch, "E896", {"start": v(184.84, 670.73) * mm, "end": v(184.84, 483.73) * mm});
            skLineSegment(sketch, "E897", {"start": v(139.84, 478.73) * mm, "end": v(179.84, 478.73) * mm});
            skPoint(sketch, "E898.visualSharp", {"position": v(134.84, 478.73) * mm});
            skArc(sketch, "E898.filletArc", {"start": v(134.84, 483.73) * mm, "mid": v(136.3, 480.2) * mm, "end": v(139.84, 478.73) * mm});
            skPoint(sketch, "E899.visualSharp", {"position": v(184.84, 478.73) * mm});
            skArc(sketch, "E899.filletArc", {"start": v(179.84, 478.73) * mm, "mid": v(183.38, 480.2) * mm, "end": v(184.84, 483.73) * mm});
            skPoint(sketch, "E900.endSnap0", {"position": v(159.84, 478.73) * mm});
            skLineSegment(sketch, "E901.bottom", {"start": v(164.84, 660.73) * mm, "end": v(154.84, 660.73) * mm});
            skLineSegment(sketch, "E901.top", {"start": v(164.84, 630.73) * mm, "end": v(154.84, 630.73) * mm});
            skLineSegment(sketch, "E901.left", {"start": v(169.84, 655.73) * mm, "end": v(169.84, 635.73) * mm});
            skLineSegment(sketch, "E901.right", {"start": v(149.84, 655.73) * mm, "end": v(149.84, 635.73) * mm});
            skLineSegment(sketch, "E902.bottom", {"start": v(164.84, 615.73) * mm, "end": v(154.84, 615.73) * mm});
            skLineSegment(sketch, "E902.top", {"start": v(164.84, 585.73) * mm, "end": v(154.84, 585.73) * mm});
            skLineSegment(sketch, "E902.left", {"start": v(169.84, 610.73) * mm, "end": v(169.84, 590.73) * mm});
            skLineSegment(sketch, "E902.right", {"start": v(149.84, 610.73) * mm, "end": v(149.84, 590.73) * mm});
            skLineSegment(sketch, "E903.bottom", {"start": v(164.84, 570.73) * mm, "end": v(154.84, 570.73) * mm});
            skLineSegment(sketch, "E903.top", {"start": v(164.84, 540.73) * mm, "end": v(154.84, 540.73) * mm});
            skLineSegment(sketch, "E903.left", {"start": v(169.84, 565.73) * mm, "end": v(169.84, 545.73) * mm});
            skLineSegment(sketch, "E903.right", {"start": v(149.84, 565.73) * mm, "end": v(149.84, 545.73) * mm});
            skPoint(sketch, "E904.visualSharp", {"position": v(149.84, 660.73) * mm});
            skArc(sketch, "E904.filletArc", {"start": v(154.84, 660.73) * mm, "mid": v(151.3, 659.27) * mm, "end": v(149.84, 655.73) * mm});
            skPoint(sketch, "E905.visualSharp", {"position": v(169.84, 660.73) * mm});
            skArc(sketch, "E905.filletArc", {"start": v(169.84, 655.73) * mm, "mid": v(168.38, 659.27) * mm, "end": v(164.84, 660.73) * mm});
            skPoint(sketch, "E906.visualSharp", {"position": v(169.84, 630.73) * mm});
            skArc(sketch, "E906.filletArc", {"start": v(164.84, 630.73) * mm, "mid": v(168.38, 632.2) * mm, "end": v(169.84, 635.73) * mm});
            skPoint(sketch, "E907.visualSharp", {"position": v(149.84, 630.73) * mm});
            skArc(sketch, "E907.filletArc", {"start": v(149.84, 635.73) * mm, "mid": v(151.3, 632.2) * mm, "end": v(154.84, 630.73) * mm});
            skPoint(sketch, "E908.visualSharp", {"position": v(169.84, 615.73) * mm});
            skArc(sketch, "E908.filletArc", {"start": v(169.84, 610.73) * mm, "mid": v(168.38, 614.27) * mm, "end": v(164.84, 615.73) * mm});
            skPoint(sketch, "E909.visualSharp", {"position": v(149.84, 615.73) * mm});
            skArc(sketch, "E909.filletArc", {"start": v(154.84, 615.73) * mm, "mid": v(151.3, 614.27) * mm, "end": v(149.84, 610.73) * mm});
            skPoint(sketch, "E910.visualSharp", {"position": v(149.84, 585.73) * mm});
            skArc(sketch, "E910.filletArc", {"start": v(149.84, 590.73) * mm, "mid": v(151.3, 587.2) * mm, "end": v(154.84, 585.73) * mm});
            skPoint(sketch, "E911.visualSharp", {"position": v(169.84, 585.73) * mm});
            skArc(sketch, "E911.filletArc", {"start": v(164.84, 585.73) * mm, "mid": v(168.38, 587.2) * mm, "end": v(169.84, 590.73) * mm});
            skPoint(sketch, "E912.visualSharp", {"position": v(169.84, 570.73) * mm});
            skArc(sketch, "E912.filletArc", {"start": v(169.84, 565.73) * mm, "mid": v(168.38, 569.27) * mm, "end": v(164.84, 570.73) * mm});
            skPoint(sketch, "E913.visualSharp", {"position": v(149.84, 570.73) * mm});
            skArc(sketch, "E913.filletArc", {"start": v(154.84, 570.73) * mm, "mid": v(151.3, 569.27) * mm, "end": v(149.84, 565.73) * mm});
            skPoint(sketch, "E914.visualSharp", {"position": v(169.84, 540.73) * mm});
            skArc(sketch, "E914.filletArc", {"start": v(164.84, 540.73) * mm, "mid": v(168.38, 542.2) * mm, "end": v(169.84, 545.73) * mm});
            skPoint(sketch, "E915.visualSharp", {"position": v(149.84, 540.73) * mm});
            skArc(sketch, "E915.filletArc", {"start": v(149.84, 545.73) * mm, "mid": v(151.3, 542.2) * mm, "end": v(154.84, 540.73) * mm});
            skLineSegment(sketch, "E916", {"start": v(137.84, 508.73) * mm, "end": v(137.84, 496.73) * mm});
            skLineSegment(sketch, "E917", {"start": v(137.84, 496.73) * mm, "end": v(140.84, 496.73) * mm});
            skLineSegment(sketch, "E918", {"start": v(140.84, 496.73) * mm, "end": v(140.84, 508.73) * mm});
            skLineSegment(sketch, "E919", {"start": v(140.84, 508.73) * mm, "end": v(137.84, 508.73) * mm});
            skLineSegment(sketch, "E920", {"start": v(149.84, 555.73) * mm, "end": v(169.84, 555.73) * mm, "construction": true});
            skArc(sketch, "E921.MirrorCS", {"start": v(164.84, 525.73) * mm, "mid": v(168.38, 524.27) * mm, "end": v(169.84, 520.73) * mm});
            skArc(sketch, "E922.MirrorCS", {"start": v(149.84, 520.73) * mm, "mid": v(151.3, 524.27) * mm, "end": v(154.84, 525.73) * mm});
            skPoint(sketch, "E923.MirrorP", {"position": v(169.84, 525.73) * mm});
            skLineSegment(sketch, "E924.MirrorCS", {"start": v(164.84, 525.73) * mm, "end": v(154.84, 525.73) * mm});
            skPoint(sketch, "E925.MirrorP", {"position": v(149.84, 525.73) * mm});
            skLineSegment(sketch, "E926.MirrorCS", {"start": v(169.84, 516.23) * mm, "end": v(169.84, 520.73) * mm});
            skLineSegment(sketch, "E927", {"start": v(159.84, 495.73) * mm, "end": v(159.84, 525.73) * mm, "construction": true});
            skLineSegment(sketch, "E928", {"start": v(149.84, 501.23) * mm, "end": v(159.84, 501.23) * mm});
            skLineSegment(sketch, "E929", {"start": v(149.84, 504.23) * mm, "end": v(159.84, 504.23) * mm});
            skLineSegment(sketch, "E930", {"start": v(154.84, 511.23) * mm, "end": v(164.84, 511.23) * mm});
            skLineSegment(sketch, "E931.trimOffspring", {"start": v(149.84, 516.23) * mm, "end": v(149.84, 520.73) * mm});
            skLineSegment(sketch, "E932", {"start": v(149.84, 504.23) * mm, "end": v(149.84, 501.23) * mm});
            skPoint(sketch, "E933.0.visualSharp", {"position": v(149.84, 511.23) * mm});
            skArc(sketch, "E933.0.filletArc", {"start": v(149.84, 516.23) * mm, "mid": v(151.3, 512.7) * mm, "end": v(154.84, 511.23) * mm});
            skPoint(sketch, "E934.0.visualSharp", {"position": v(169.84, 511.23) * mm});
            skArc(sketch, "E934.0.filletArc", {"start": v(164.84, 511.23) * mm, "mid": v(168.38, 512.7) * mm, "end": v(169.84, 516.23) * mm});
            skLineSegment(sketch, "E935.MirrorCS", {"start": v(178.84, 496.73) * mm, "end": v(178.84, 508.73) * mm});
            skLineSegment(sketch, "E936.MirrorCS", {"start": v(181.84, 496.73) * mm, "end": v(178.84, 496.73) * mm});
            skLineSegment(sketch, "E937.MirrorCS", {"start": v(181.84, 508.73) * mm, "end": v(181.84, 496.73) * mm});
            skLineSegment(sketch, "E938.MirrorCS", {"start": v(178.84, 508.73) * mm, "end": v(181.84, 508.73) * mm});
            skLineSegment(sketch, "E939.MirrorCS", {"start": v(178.84, 580.73) * mm, "end": v(181.84, 580.73) * mm});
            skLineSegment(sketch, "E940.MirrorCS", {"start": v(181.84, 580.73) * mm, "end": v(181.84, 568.73) * mm});
            skLineSegment(sketch, "E941.MirrorCS", {"start": v(178.84, 568.73) * mm, "end": v(178.84, 580.73) * mm});
            skLineSegment(sketch, "E942.MirrorCS", {"start": v(181.84, 568.73) * mm, "end": v(178.84, 568.73) * mm});
            skLineSegment(sketch, "E943.MirrorCS", {"start": v(178.84, 648.73) * mm, "end": v(178.84, 660.73) * mm});
            skLineSegment(sketch, "E944.MirrorCS", {"start": v(178.84, 660.73) * mm, "end": v(181.84, 660.73) * mm});
            skLineSegment(sketch, "E945.MirrorCS", {"start": v(181.84, 660.73) * mm, "end": v(181.84, 648.73) * mm});
            skLineSegment(sketch, "E946.MirrorCS", {"start": v(181.84, 648.73) * mm, "end": v(178.84, 648.73) * mm});
            skLineSegment(sketch, "E947.MirrorCS", {"start": v(169.84, 504.23) * mm, "end": v(169.84, 501.23) * mm});
            skLineSegment(sketch, "E948.MirrorCS", {"start": v(169.84, 501.23) * mm, "end": v(159.84, 501.23) * mm});
            skLineSegment(sketch, "E949.MirrorCS", {"start": v(169.84, 504.23) * mm, "end": v(159.84, 504.23) * mm});
            skLineSegment(sketch, "E950", {"start": v(238.99, 443.91) * mm, "end": v(235.99, 443.91) * mm});
            skLineSegment(sketch, "E951", {"start": v(232.99, 452.91) * mm, "end": v(235.99, 452.91) * mm});
            skLineSegment(sketch, "E952", {"start": v(235.99, 452.91) * mm, "end": v(235.99, 443.91) * mm});
            skLineSegment(sketch, "E953.MirrorCS", {"start": v(238.99, 423.91) * mm, "end": v(235.99, 423.91) * mm});
            skLineSegment(sketch, "E954.MirrorCS", {"start": v(235.99, 414.91) * mm, "end": v(235.99, 423.91) * mm});
            skLineSegment(sketch, "E955.MirrorCS", {"start": v(232.99, 414.91) * mm, "end": v(235.99, 414.91) * mm});
            skLineSegment(sketch, "E956.right", {"start": v(403.28, 676.43) * mm, "end": v(403.28, 666.43) * mm});
            skLineSegment(sketch, "E957", {"start": v(403.28, 586.43) * mm, "end": v(403.28, 644.43) * mm});
            skLineSegment(sketch, "E958", {"start": v(403.28, 666.43) * mm, "end": v(380.28, 666.43) * mm});
            skLineSegment(sketch, "E959", {"start": v(403.28, 644.43) * mm, "end": v(380.28, 644.43) * mm});
            skLineSegment(sketch, "E960", {"start": v(403.28, 586.43) * mm, "end": v(380.28, 586.46) * mm});
            skLineSegment(sketch, "E961", {"start": v(403.28, 564.4) * mm, "end": v(380.28, 564.4) * mm});
            skLineSegment(sketch, "E962", {"start": v(403.28, 514.4) * mm, "end": v(380.28, 514.4) * mm});
            skLineSegment(sketch, "E963", {"start": v(403.28, 492.4) * mm, "end": v(380.28, 492.4) * mm});
            skLineSegment(sketch, "E964", {"start": v(403.28, 514.4) * mm, "end": v(403.28, 564.4) * mm});
            skLineSegment(sketch, "E965", {"start": v(403.28, 666.43) * mm, "end": v(403.28, 644.43) * mm, "construction": true});
            skPoint(sketch, "E966.orphan", {"position": v(403.28, 655.43) * mm});
            skArc(sketch, "E967", {"start": v(380.28, 514.4) * mm, "mid": v(369.28, 503.4) * mm, "end": v(380.28, 492.4) * mm});
            skArc(sketch, "E968", {"start": v(380.28, 586.46) * mm, "mid": v(369.25, 575.43) * mm, "end": v(380.28, 564.4) * mm});
            skArc(sketch, "E969", {"start": v(380.28, 666.43) * mm, "mid": v(369.28, 655.43) * mm, "end": v(380.28, 644.43) * mm});
            skLineSegment(sketch, "E970", {"start": v(403.28, 492.4) * mm, "end": v(403.28, 480.4) * mm});
            skArc(sketch, "E971", {"start": v(403.28, 480.4) * mm, "mid": v(428.19, 491.25) * mm, "end": v(437.2, 516.88) * mm});
            skArc(sketch, "E972", {"start": v(437.14, 642.57) * mm, "mid": v(427.22, 666.51) * mm, "end": v(403.28, 676.43) * mm});
            skLineSegment(sketch, "E973", {"start": v(416.28, 629.43) * mm, "end": v(416.28, 605.43) * mm});
            skLineSegment(sketch, "E974", {"start": v(416.28, 635.43) * mm, "end": v(419.28, 635.43) * mm});
            skLineSegment(sketch, "E975", {"start": v(419.28, 635.43) * mm, "end": v(419.28, 605.43) * mm});
            skLineSegment(sketch, "E976", {"start": v(419.28, 605.43) * mm, "end": v(416.28, 605.43) * mm});
            skLineSegment(sketch, "E977", {"start": v(416.28, 515.43) * mm, "end": v(419.28, 515.43) * mm});
            skLineSegment(sketch, "E978", {"start": v(419.28, 515.43) * mm, "end": v(419.28, 545.43) * mm});
            skLineSegment(sketch, "E979", {"start": v(419.28, 545.43) * mm, "end": v(416.28, 545.43) * mm});
            skLineSegment(sketch, "E980", {"start": v(380.28, 575.43) * mm, "end": v(410.28, 575.43) * mm, "construction": true});
            skLineSegment(sketch, "E981.trimOffspring", {"start": v(416.28, 545.43) * mm, "end": v(416.28, 515.43) * mm});
            skLineSegment(sketch, "E982", {"start": v(416.28, 545.43) * mm, "end": v(416.28, 575.43) * mm, "construction": true});
            skLineSegment(sketch, "E983", {"start": v(416.28, 575.43) * mm, "end": v(416.28, 605.43) * mm, "construction": true});
            skLineSegment(sketch, "E984.bottom", {"start": v(516.83, 642.37) * mm, "end": v(534.1, 642.37) * mm});
            skLineSegment(sketch, "E984.left", {"start": v(496.1, 642.37) * mm, "end": v(496.1, 638.42) * mm});
            skLineSegment(sketch, "E985", {"start": v(496.1, 638.42) * mm, "end": v(493.1, 638.42) * mm});
            skLineSegment(sketch, "E986", {"start": v(493.1, 638.42) * mm, "end": v(493.1, 608.42) * mm});
            skLineSegment(sketch, "E987", {"start": v(493.1, 608.42) * mm, "end": v(496.1, 608.42) * mm});
            skLineSegment(sketch, "E988", {"start": v(496.1, 518.42) * mm, "end": v(493.1, 518.42) * mm});
            skLineSegment(sketch, "E989", {"start": v(493.1, 518.42) * mm, "end": v(493.1, 548.42) * mm});
            skLineSegment(sketch, "E990", {"start": v(493.1, 548.42) * mm, "end": v(496.1, 548.42) * mm});
            skLineSegment(sketch, "E991.trimOffspring", {"start": v(496.1, 518.42) * mm, "end": v(496.1, 515.42) * mm});
            skLineSegment(sketch, "E992.trimOffspring", {"start": v(496.1, 608.42) * mm, "end": v(496.1, 548.42) * mm});
            skLineSegment(sketch, "E993", {"start": v(419.28, 635.43) * mm, "end": v(419.28, 672.4) * mm, "construction": true});
            skLineSegment(sketch, "E994.MirrorCS", {"start": v(534.1, 642.37) * mm, "end": v(534.1, 638.42) * mm});
            skLineSegment(sketch, "E995.MirrorCS", {"start": v(534.1, 638.42) * mm, "end": v(537.1, 638.42) * mm});
            skLineSegment(sketch, "E996.MirrorCS", {"start": v(537.1, 638.42) * mm, "end": v(537.1, 608.42) * mm});
            skLineSegment(sketch, "E997.MirrorCS", {"start": v(537.1, 608.42) * mm, "end": v(534.1, 608.42) * mm});
            skLineSegment(sketch, "E998.MirrorCS", {"start": v(537.1, 548.42) * mm, "end": v(534.1, 548.42) * mm});
            skLineSegment(sketch, "E999.MirrorCS", {"start": v(537.1, 518.42) * mm, "end": v(537.1, 548.42) * mm});
            skLineSegment(sketch, "E1000.MirrorCS", {"start": v(534.1, 518.42) * mm, "end": v(537.1, 518.42) * mm});
            skLineSegment(sketch, "E1001.MirrorCS", {"start": v(534.1, 518.42) * mm, "end": v(534.1, 515.42) * mm});
            skLineSegment(sketch, "E1002", {"start": v(496.1, 515.42) * mm, "end": v(497.42, 515.42) * mm});
            skLineSegment(sketch, "E1003", {"start": v(534.1, 515.42) * mm, "end": v(532.77, 515.42) * mm});
            skArc(sketch, "E1004", {"start": v(531.05, 516.39) * mm, "mid": v(515.1, 525.42) * mm, "end": v(499.14, 516.39) * mm});
            skPoint(sketch, "E1005.0.visualSharp", {"position": v(498.6, 515.42) * mm});
            skArc(sketch, "E1005.0.filletArc", {"start": v(497.42, 515.42) * mm, "mid": v(498.4, 515.68) * mm, "end": v(499.14, 516.39) * mm});
            skPoint(sketch, "E1006.0.visualSharp", {"position": v(531.6, 515.42) * mm});
            skArc(sketch, "E1006.0.filletArc", {"start": v(531.05, 516.39) * mm, "mid": v(531.78, 515.68) * mm, "end": v(532.77, 515.42) * mm});
            skLineSegment(sketch, "E1007", {"start": v(502.1, 583.22) * mm, "end": v(502.1, 638.22) * mm});
            skLineSegment(sketch, "E1008", {"start": v(502.1, 638.22) * mm, "end": v(511.1, 638.22) * mm});
            skLineSegment(sketch, "E1009", {"start": v(511.1, 638.22) * mm, "end": v(511.1, 583.23) * mm});
            skLineSegment(sketch, "E1010", {"start": v(511.1, 583.23) * mm, "end": v(502.1, 583.22) * mm});
            skLineSegment(sketch, "E1011", {"start": v(416.28, 635.43) * mm, "end": v(413.28, 635.43) * mm});
            skLineSegment(sketch, "E1012", {"start": v(413.28, 635.43) * mm, "end": v(413.28, 629.43) * mm});
            skLineSegment(sketch, "E1013", {"start": v(413.28, 629.43) * mm, "end": v(416.28, 629.43) * mm});
            skLineSegment(sketch, "E1014.bottom", {"start": v(574.63, 643.98) * mm, "end": v(612.63, 643.98) * mm});
            skLineSegment(sketch, "E1014.left", {"start": v(574.63, 643.98) * mm, "end": v(574.63, 640.03) * mm});
            skLineSegment(sketch, "E1015", {"start": v(574.63, 640.03) * mm, "end": v(571.63, 640.03) * mm});
            skLineSegment(sketch, "E1016", {"start": v(571.63, 640.03) * mm, "end": v(571.63, 610.03) * mm});
            skLineSegment(sketch, "E1017", {"start": v(571.63, 610.03) * mm, "end": v(574.63, 610.03) * mm});
            skLineSegment(sketch, "E1018", {"start": v(574.63, 520.03) * mm, "end": v(571.63, 520.03) * mm});
            skLineSegment(sketch, "E1019", {"start": v(571.63, 520.03) * mm, "end": v(571.63, 550.03) * mm});
            skLineSegment(sketch, "E1020", {"start": v(571.63, 550.03) * mm, "end": v(574.63, 550.03) * mm});
            skLineSegment(sketch, "E1021.trimOffspring", {"start": v(574.63, 520.03) * mm, "end": v(574.63, 517.03) * mm});
            skLineSegment(sketch, "E1022.trimOffspring", {"start": v(574.63, 610.03) * mm, "end": v(574.63, 550.03) * mm});
            skLineSegment(sketch, "E1023.MirrorCS", {"start": v(612.63, 643.98) * mm, "end": v(612.63, 640.03) * mm});
            skLineSegment(sketch, "E1024.MirrorCS", {"start": v(612.63, 640.03) * mm, "end": v(615.63, 640.03) * mm});
            skLineSegment(sketch, "E1025.MirrorCS", {"start": v(615.63, 640.03) * mm, "end": v(615.63, 610.03) * mm});
            skLineSegment(sketch, "E1026.MirrorCS", {"start": v(615.63, 610.03) * mm, "end": v(612.63, 610.03) * mm});
            skLineSegment(sketch, "E1027.MirrorCS", {"start": v(612.63, 610.03) * mm, "end": v(612.63, 550.03) * mm});
            skLineSegment(sketch, "E1028.MirrorCS", {"start": v(615.63, 550.03) * mm, "end": v(612.63, 550.03) * mm});
            skLineSegment(sketch, "E1029.MirrorCS", {"start": v(615.63, 520.03) * mm, "end": v(615.63, 550.03) * mm});
            skLineSegment(sketch, "E1030.MirrorCS", {"start": v(612.63, 520.03) * mm, "end": v(615.63, 520.03) * mm});
            skLineSegment(sketch, "E1031.MirrorCS", {"start": v(612.63, 520.03) * mm, "end": v(612.63, 517.03) * mm});
            skLineSegment(sketch, "E1032", {"start": v(574.63, 517.03) * mm, "end": v(575.96, 517.03) * mm});
            skLineSegment(sketch, "E1033", {"start": v(612.63, 517.03) * mm, "end": v(611.3, 517.03) * mm});
            skArc(sketch, "E1034", {"start": v(609.6, 518) * mm, "mid": v(593.63, 527.03) * mm, "end": v(577.68, 518) * mm});
            skPoint(sketch, "E1035.0.visualSharp", {"position": v(577.13, 517.03) * mm});
            skArc(sketch, "E1035.0.filletArc", {"start": v(575.96, 517.03) * mm, "mid": v(576.95, 517.29) * mm, "end": v(577.68, 518) * mm});
            skPoint(sketch, "E1036.0.visualSharp", {"position": v(610.13, 517.03) * mm});
            skArc(sketch, "E1036.0.filletArc", {"start": v(609.6, 518) * mm, "mid": v(610.32, 517.29) * mm, "end": v(611.3, 517.03) * mm});
            skLineSegment(sketch, "E1037", {"start": v(574.63, 580.03) * mm, "end": v(612.63, 580.03) * mm, "construction": true});
            skLineSegment(sketch, "E1038", {"start": v(593.63, 643.98) * mm, "end": v(593.63, 527.03) * mm, "construction": true});
            skCircle(sketch, "E1039.MirrorC", {"center": v(578.63, 565.03) * mm, "radius": 1.18 * mm});
            skCircle(sketch, "E1040.MirrorC", {"center": v(608.63, 565.03) * mm, "radius": 1.18 * mm});
            skLineSegment(sketch, "E1041.bottom", {"start": v(655.47, 586.05) * mm, "end": v(685.47, 586.05) * mm, "construction": true});
            skLineSegment(sketch, "E1041.top", {"start": v(655.47, 556.05) * mm, "end": v(685.47, 556.05) * mm, "construction": true});
            skLineSegment(sketch, "E1041.left", {"start": v(655.47, 586.05) * mm, "end": v(655.47, 556.05) * mm, "construction": true});
            skLineSegment(sketch, "E1041.right", {"start": v(685.47, 586.05) * mm, "end": v(685.47, 556.05) * mm, "construction": true});
            skCircle(sketch, "E1042", {"center": v(655.47, 586.05) * mm, "radius": 1.57 * mm});
            skCircle(sketch, "E1043", {"center": v(685.47, 586.05) * mm, "radius": 1.57 * mm});
            skCircle(sketch, "E1044", {"center": v(685.47, 556.05) * mm, "radius": 1.57 * mm});
            skCircle(sketch, "E1045", {"center": v(655.47, 556.05) * mm, "radius": 1.57 * mm});
            skLineSegment(sketch, "E1046", {"start": v(655.47, 571.05) * mm, "end": v(652.22, 571.05) * mm, "construction": true});
            skLineSegment(sketch, "E1047", {"start": v(670.47, 586.05) * mm, "end": v(670.47, 589.3) * mm, "construction": true});
            skLineSegment(sketch, "E1048", {"start": v(685.47, 571.05) * mm, "end": v(688.72, 571.05) * mm, "construction": true});
            skLineSegment(sketch, "E1049", {"start": v(670.47, 556.05) * mm, "end": v(670.47, 552.8) * mm, "construction": true});
            skLineSegment(sketch, "E1050", {"start": v(670.47, 552.8) * mm, "end": v(652.22, 552.8) * mm});
            skLineSegment(sketch, "E1051", {"start": v(652.22, 552.8) * mm, "end": v(652.22, 571.05) * mm});
            skLineSegment(sketch, "E1052", {"start": v(652.22, 571.05) * mm, "end": v(652.22, 589.3) * mm});
            skLineSegment(sketch, "E1053", {"start": v(652.22, 589.3) * mm, "end": v(658.97, 589.3) * mm});
            skLineSegment(sketch, "E1054.MirrorCS", {"start": v(688.72, 589.3) * mm, "end": v(681.97, 589.3) * mm});
            skLineSegment(sketch, "E1055.MirrorCS", {"start": v(688.72, 571.05) * mm, "end": v(688.72, 589.3) * mm});
            skLineSegment(sketch, "E1056.MirrorCS", {"start": v(688.72, 552.8) * mm, "end": v(688.72, 571.05) * mm});
            skLineSegment(sketch, "E1057.MirrorCS", {"start": v(670.47, 552.8) * mm, "end": v(688.72, 552.8) * mm});
            skLineSegment(sketch, "E1058.bottom", {"start": v(666.97, 593.72) * mm, "end": v(658.97, 593.72) * mm, "construction": true});
            skLineSegment(sketch, "E1058.top", {"start": v(666.97, 583.55) * mm, "end": v(658.97, 583.55) * mm});
            skLineSegment(sketch, "E1058.left", {"start": v(666.97, 593.72) * mm, "end": v(666.97, 583.55) * mm});
            skLineSegment(sketch, "E1058.right", {"start": v(658.97, 593.72) * mm, "end": v(658.97, 583.55) * mm});
            skLineSegment(sketch, "E1059.trimOffspring", {"start": v(666.97, 589.3) * mm, "end": v(670.47, 589.3) * mm});
            skLineSegment(sketch, "E1060.MirrorCS", {"start": v(673.97, 593.72) * mm, "end": v(673.97, 583.55) * mm});
            skLineSegment(sketch, "E1061.MirrorCS", {"start": v(681.97, 593.72) * mm, "end": v(681.97, 583.55) * mm});
            skLineSegment(sketch, "E1062.MirrorCS", {"start": v(673.97, 583.55) * mm, "end": v(681.97, 583.55) * mm});
            skLineSegment(sketch, "E1063.trimOffspring", {"start": v(673.97, 589.3) * mm, "end": v(670.47, 589.3) * mm});
            skCircle(sketch, "E1064.MirrorC", {"center": v(578.63, 595.03) * mm, "radius": 1.18 * mm});
            skCircle(sketch, "E1065.MirrorC", {"center": v(608.63, 595.03) * mm, "radius": 1.18 * mm});
            skLineSegment(sketch, "E1066", {"start": v(434.28, 575.43) * mm, "end": v(434.28, 590.43) * mm});
            skLineSegment(sketch, "E1067", {"start": v(431.28, 575.43) * mm, "end": v(431.28, 590.43) * mm});
            skLineSegment(sketch, "E1068", {"start": v(431.28, 590.43) * mm, "end": v(434.28, 590.43) * mm});
            skLineSegment(sketch, "E1069.MirrorCS", {"start": v(431.28, 575.43) * mm, "end": v(431.28, 560.43) * mm});
            skLineSegment(sketch, "E1070.MirrorCS", {"start": v(434.28, 575.43) * mm, "end": v(434.28, 560.43) * mm});
            skLineSegment(sketch, "E1071.MirrorCS", {"start": v(431.28, 560.43) * mm, "end": v(434.28, 560.43) * mm});
            skLineSegment(sketch, "E1072.bottom", {"start": v(466.5, 483.75) * mm, "end": v(496.5, 483.75) * mm, "construction": true});
            skLineSegment(sketch, "E1072.top", {"start": v(466.5, 453.75) * mm, "end": v(496.5, 453.75) * mm, "construction": true});
            skLineSegment(sketch, "E1072.left", {"start": v(466.5, 483.75) * mm, "end": v(466.5, 453.75) * mm, "construction": true});
            skLineSegment(sketch, "E1072.right", {"start": v(496.5, 483.75) * mm, "end": v(496.5, 453.75) * mm, "construction": true});
            skCircle(sketch, "E1073", {"center": v(466.5, 483.75) * mm, "radius": 1.57 * mm});
            skCircle(sketch, "E1074", {"center": v(496.5, 483.75) * mm, "radius": 1.57 * mm});
            skCircle(sketch, "E1075", {"center": v(496.5, 453.75) * mm, "radius": 1.57 * mm});
            skCircle(sketch, "E1076", {"center": v(466.5, 453.75) * mm, "radius": 1.57 * mm});
            skLineSegment(sketch, "E1077", {"start": v(466.5, 468.75) * mm, "end": v(462.5, 468.75) * mm, "construction": true});
            skLineSegment(sketch, "E1078", {"start": v(481.5, 483.75) * mm, "end": v(481.5, 487.75) * mm, "construction": true});
            skLineSegment(sketch, "E1079", {"start": v(496.5, 468.75) * mm, "end": v(500.5, 468.75) * mm, "construction": true});
            skLineSegment(sketch, "E1080", {"start": v(481.5, 453.75) * mm, "end": v(481.5, 449.75) * mm, "construction": true});
            skLineSegment(sketch, "E1081", {"start": v(481.5, 449.75) * mm, "end": v(462.5, 449.75) * mm});
            skLineSegment(sketch, "E1082", {"start": v(462.5, 449.75) * mm, "end": v(462.5, 453.75) * mm});
            skLineSegment(sketch, "E1083", {"start": v(462.5, 483.75) * mm, "end": v(462.5, 487.75) * mm});
            skLineSegment(sketch, "E1084.MirrorCS", {"start": v(500.5, 483.75) * mm, "end": v(500.5, 487.75) * mm});
            skLineSegment(sketch, "E1085.MirrorCS", {"start": v(500.5, 449.75) * mm, "end": v(500.5, 453.75) * mm});
            skLineSegment(sketch, "E1086.MirrorCS", {"start": v(481.5, 449.75) * mm, "end": v(500.5, 449.75) * mm});
            skLineSegment(sketch, "E1087", {"start": v(500.5, 487.75) * mm, "end": v(481.5, 487.75) * mm});
            skLineSegment(sketch, "E1088", {"start": v(462.5, 487.75) * mm, "end": v(481.5, 487.75) * mm});
            skLineSegment(sketch, "E1089", {"start": v(462.5, 483.75) * mm, "end": v(459.5, 483.75) * mm});
            skLineSegment(sketch, "E1090", {"start": v(459.5, 483.75) * mm, "end": v(459.5, 453.75) * mm});
            skLineSegment(sketch, "E1091", {"start": v(459.5, 453.75) * mm, "end": v(462.5, 453.75) * mm});
            skLineSegment(sketch, "E1092.MirrorCS", {"start": v(500.5, 483.75) * mm, "end": v(503.5, 483.75) * mm});
            skLineSegment(sketch, "E1093.MirrorCS", {"start": v(503.5, 483.75) * mm, "end": v(503.5, 453.75) * mm});
            skLineSegment(sketch, "E1094.MirrorCS", {"start": v(503.5, 453.75) * mm, "end": v(500.5, 453.75) * mm});
            skPoint(sketch, "E1095.orphan", {"position": v(500.5, 468.75) * mm});
            skLineSegment(sketch, "E1096", {"start": v(434.28, 575.43) * mm, "end": v(437.14, 575.43) * mm, "construction": true});
            skLineSegment(sketch, "E1097", {"start": v(437.14, 575.43) * mm, "end": v(452.28, 575.43) * mm, "construction": true});
            skLineSegment(sketch, "E1098", {"start": v(452.28, 575.43) * mm, "end": v(452.28, 594.85) * mm});
            skLineSegment(sketch, "E1099.MirrorCS", {"start": v(452.28, 575.43) * mm, "end": v(452.28, 556) * mm});
            skLineSegment(sketch, "E1100", {"start": v(452.07, 554.9) * mm, "end": v(437.4, 518.21) * mm});
            skPoint(sketch, "E1101.0.visualSharp", {"position": v(437.14, 517.55) * mm});
            skArc(sketch, "E1101.0.filletArc", {"start": v(437.4, 518.21) * mm, "mid": v(437.22, 517.56) * mm, "end": v(437.2, 516.88) * mm});
            skLineSegment(sketch, "E1102.MirrorCS", {"start": v(452.07, 595.96) * mm, "end": v(437.4, 632.64) * mm});
            skArc(sketch, "E1103.MirrorCS", {"start": v(437.4, 632.64) * mm, "mid": v(437.22, 633.3) * mm, "end": v(437.2, 633.98) * mm});
            skLineSegment(sketch, "E1104", {"start": v(437.14, 642.57) * mm, "end": v(437.2, 633.98) * mm});
            skPoint(sketch, "E1105.0.visualSharp", {"position": v(452.28, 555.43) * mm});
            skArc(sketch, "E1105.0.filletArc", {"start": v(452.07, 554.9) * mm, "mid": v(452.23, 555.44) * mm, "end": v(452.28, 556) * mm});
            skPoint(sketch, "E1106.0.visualSharp", {"position": v(452.28, 595.43) * mm});
            skArc(sketch, "E1106.0.filletArc", {"start": v(452.28, 594.85) * mm, "mid": v(452.23, 595.42) * mm, "end": v(452.07, 595.96) * mm});
            skLineSegment(sketch, "E1107", {"start": v(441.28, 583.43) * mm, "end": v(441.28, 567.43) * mm});
            skLineSegment(sketch, "E1108", {"start": v(441.28, 567.43) * mm, "end": v(447.28, 567.43) * mm});
            skLineSegment(sketch, "E1109", {"start": v(447.28, 567.43) * mm, "end": v(447.28, 583.43) * mm});
            skLineSegment(sketch, "E1110", {"start": v(447.28, 583.43) * mm, "end": v(441.28, 583.43) * mm});
            skLineSegment(sketch, "E1111", {"start": v(534.1, 608.42) * mm, "end": v(534.1, 548.42) * mm});
            skArc(sketch, "E1112", {"start": v(516.83, 642.37) * mm, "mid": v(506.46, 649.38) * mm, "end": v(496.1, 642.37) * mm});
            skLineSegment(sketch, "E1113", {"start": v(410.28, 600.88) * mm, "end": v(410.28, 591.78) * mm, "construction": true});
            skLineSegment(sketch, "E1114", {"start": v(417.28, 600.72) * mm, "end": v(417.28, 548.7) * mm, "construction": true});
            skLineSegment(sketch, "E1115", {"start": v(414.57, 577.27) * mm, "end": v(421.5, 580.23) * mm});
            skLineSegment(sketch, "E1116", {"start": v(413.07, 580.97) * mm, "end": v(420, 583.94) * mm});
            skLineSegment(sketch, "E1117", {"start": v(420, 587.62) * mm, "end": v(413.07, 590.58) * mm});
            skLineSegment(sketch, "E1118", {"start": v(414.76, 594.21) * mm, "end": v(421.5, 591.33) * mm});
            skLineSegment(sketch, "E1119", {"start": v(415.16, 596.13) * mm, "end": v(422.28, 596.13) * mm});
            skLineSegment(sketch, "E1120.trimOffspring", {"start": v(424.28, 575.43) * mm, "end": v(434.28, 575.43) * mm, "construction": true});
            skLineSegment(sketch, "E1121.trimOffspring", {"start": v(424.28, 581.43) * mm, "end": v(424.28, 590.13) * mm, "construction": true});
            skLineSegment(sketch, "E1122", {"start": v(424.28, 575.43) * mm, "end": v(424.28, 578.4) * mm});
            skLineSegment(sketch, "E1123.trimOffspring", {"start": v(410.28, 579.78) * mm, "end": v(410.28, 548.69) * mm, "construction": true});
            skLineSegment(sketch, "E1124.trimOffspring", {"start": v(424.28, 596.13) * mm, "end": v(424.28, 601.75) * mm, "construction": true});
            skLineSegment(sketch, "E1125", {"start": v(424.28, 594.13) * mm, "end": v(424.28, 593.16) * mm});
            skLineSegment(sketch, "E1126", {"start": v(410.28, 588.75) * mm, "end": v(410.28, 582.81) * mm});
            skPoint(sketch, "E1127.0.visualSharp", {"position": v(410.28, 591.78) * mm});
            skArc(sketch, "E1127.0.filletArc", {"start": v(413.07, 590.58) * mm, "mid": v(411.18, 590.42) * mm, "end": v(410.28, 588.75) * mm});
            skPoint(sketch, "E1128.0.visualSharp", {"position": v(410.28, 579.78) * mm});
            skArc(sketch, "E1128.0.filletArc", {"start": v(410.28, 582.81) * mm, "mid": v(411.18, 581.14) * mm, "end": v(413.07, 580.97) * mm});
            skPoint(sketch, "E1129.0.visualSharp", {"position": v(424.28, 585.78) * mm});
            skArc(sketch, "E1129.0.filletArc", {"start": v(420, 583.94) * mm, "mid": v(421.2, 585.78) * mm, "end": v(420, 587.62) * mm});
            skPoint(sketch, "E1130.0.visualSharp", {"position": v(424.28, 581.43) * mm});
            skArc(sketch, "E1130.0.filletArc", {"start": v(424.28, 578.4) * mm, "mid": v(423.38, 580.06) * mm, "end": v(421.5, 580.23) * mm});
            skPoint(sketch, "E1131.0.visualSharp", {"position": v(410.28, 596.13) * mm});
            skArc(sketch, "E1131.0.filletArc", {"start": v(415.16, 596.13) * mm, "mid": v(414.18, 595.33) * mm, "end": v(414.76, 594.21) * mm});
            skPoint(sketch, "E1132.0.visualSharp", {"position": v(424.28, 590.13) * mm});
            skArc(sketch, "E1132.0.filletArc", {"start": v(421.5, 591.33) * mm, "mid": v(423.38, 591.5) * mm, "end": v(424.28, 593.16) * mm});
            skPoint(sketch, "E1133.0.visualSharp", {"position": v(424.28, 596.13) * mm});
            skArc(sketch, "E1133.0.filletArc", {"start": v(424.28, 594.13) * mm, "mid": v(423.7, 595.55) * mm, "end": v(422.28, 596.13) * mm});
            skLineSegment(sketch, "E1134.MirrorCS", {"start": v(424.28, 556.72) * mm, "end": v(424.28, 557.7) * mm});
            skArc(sketch, "E1135.MirrorCS", {"start": v(424.28, 556.72) * mm, "mid": v(423.7, 555.3) * mm, "end": v(422.28, 554.72) * mm});
            skArc(sketch, "E1136.MirrorCS", {"start": v(420, 566.91) * mm, "mid": v(421.2, 565.08) * mm, "end": v(420, 563.24) * mm});
            skArc(sketch, "E1137.MirrorCS", {"start": v(424.28, 572.46) * mm, "mid": v(423.38, 570.8) * mm, "end": v(421.5, 570.62) * mm});
            skPoint(sketch, "E1138.MirrorP", {"position": v(424.28, 569.43) * mm});
            skArc(sketch, "E1139.MirrorCS", {"start": v(410.28, 568.04) * mm, "mid": v(411.18, 569.71) * mm, "end": v(413.07, 569.88) * mm});
            skArc(sketch, "E1140.MirrorCS", {"start": v(421.5, 559.53) * mm, "mid": v(423.38, 559.36) * mm, "end": v(424.28, 557.7) * mm});
            skPoint(sketch, "E1141.MirrorP", {"position": v(424.28, 560.72) * mm});
            skLineSegment(sketch, "E1142.MirrorCS", {"start": v(420, 563.24) * mm, "end": v(413.07, 560.27) * mm});
            skArc(sketch, "E1143.MirrorCS", {"start": v(415.16, 554.72) * mm, "mid": v(414.18, 555.52) * mm, "end": v(414.76, 556.64) * mm});
            skPoint(sketch, "E1144.MirrorP", {"position": v(424.28, 554.72) * mm});
            skLineSegment(sketch, "E1145.MirrorCS", {"start": v(410.28, 562.1) * mm, "end": v(410.28, 568.04) * mm});
            skPoint(sketch, "E1146.MirrorP", {"position": v(410.28, 571.08) * mm});
            skPoint(sketch, "E1147.MirrorP", {"position": v(424.28, 565.08) * mm});
            skArc(sketch, "E1148.MirrorCS", {"start": v(413.07, 560.27) * mm, "mid": v(411.18, 560.44) * mm, "end": v(410.28, 562.1) * mm});
            skPoint(sketch, "E1149.MirrorP", {"position": v(410.28, 559.08) * mm});
            skLineSegment(sketch, "E1150.MirrorCS", {"start": v(413.07, 569.88) * mm, "end": v(420, 566.91) * mm});
            skPoint(sketch, "E1151.MirrorP", {"position": v(410.28, 554.72) * mm});
            skLineSegment(sketch, "E1152.MirrorCS", {"start": v(415.16, 554.72) * mm, "end": v(422.28, 554.72) * mm});
            skLineSegment(sketch, "E1153.MirrorCS", {"start": v(414.76, 556.64) * mm, "end": v(421.5, 559.53) * mm});
            skLineSegment(sketch, "E1154.MirrorCS", {"start": v(424.28, 569.43) * mm, "end": v(424.28, 560.72) * mm, "construction": true});
            skLineSegment(sketch, "E1155.MirrorCS", {"start": v(414.57, 573.59) * mm, "end": v(421.5, 570.62) * mm});
            skPoint(sketch, "E1156.0.visualSharp", {"position": v(410.28, 575.43) * mm});
            skArc(sketch, "E1156.0.filletArc", {"start": v(414.57, 577.27) * mm, "mid": v(413.36, 575.43) * mm, "end": v(414.57, 573.59) * mm});
            skLineSegment(sketch, "E1157", {"start": v(424.28, 572.46) * mm, "end": v(424.28, 575.43) * mm});
            skLineSegment(sketch, "E1158", {"start": v(440.56, 611.27) * mm, "end": v(446.6, 596.17) * mm});
            skLineSegment(sketch, "E1159", {"start": v(444.74, 593.43) * mm, "end": v(429.7, 593.43) * mm});
            skLineSegment(sketch, "E1160", {"start": v(427.7, 595.43) * mm, "end": v(427.7, 606.92) * mm});
            skPoint(sketch, "E1161.0.visualSharp", {"position": v(427.7, 643.44) * mm});
            skArc(sketch, "E1161.0.filletArc", {"start": v(431.56, 633.8) * mm, "mid": v(429.32, 635.01) * mm, "end": v(427.7, 633.05) * mm});
            skPoint(sketch, "E1162.0.visualSharp", {"position": v(427.7, 593.43) * mm});
            skArc(sketch, "E1162.0.filletArc", {"start": v(427.7, 595.43) * mm, "mid": v(428.28, 594.01) * mm, "end": v(429.7, 593.43) * mm});
            skPoint(sketch, "E1163.0.visualSharp", {"position": v(447.7, 593.43) * mm});
            skArc(sketch, "E1163.0.filletArc", {"start": v(444.74, 593.43) * mm, "mid": v(446.4, 594.3) * mm, "end": v(446.6, 596.17) * mm});
            skLineSegment(sketch, "E1164", {"start": v(439.08, 614.98) * mm, "end": v(427.7, 610.43) * mm, "construction": true});
            skLineSegment(sketch, "E1165", {"start": v(436.48, 616.1) * mm, "end": v(430.44, 613.68) * mm});
            skLineSegment(sketch, "E1166", {"start": v(437.96, 612.38) * mm, "end": v(428.96, 608.78) * mm});
            skArc(sketch, "E1167.0.filletArc", {"start": v(428.96, 608.78) * mm, "mid": v(428.04, 608.04) * mm, "end": v(427.7, 606.92) * mm});
            skPoint(sketch, "E1168.0.newPointB", {"position": v(431.56, 633.8) * mm});
            skArc(sketch, "E1168.0.filletArc", {"start": v(440.56, 611.27) * mm, "mid": v(439.5, 612.36) * mm, "end": v(437.96, 612.38) * mm});
            skLineSegment(sketch, "E1169", {"start": v(437.6, 618.7) * mm, "end": v(431.56, 633.8) * mm});
            skLineSegment(sketch, "E1170", {"start": v(427.7, 615.54) * mm, "end": v(427.7, 633.05) * mm});
            skPoint(sketch, "E1171.0.visualSharp", {"position": v(427.7, 612.58) * mm});
            skArc(sketch, "E1171.0.filletArc", {"start": v(427.7, 615.54) * mm, "mid": v(428.58, 613.88) * mm, "end": v(430.44, 613.68) * mm});
            skPoint(sketch, "E1172.0.visualSharp", {"position": v(438.34, 616.84) * mm});
            skArc(sketch, "E1172.0.filletArc", {"start": v(436.48, 616.1) * mm, "mid": v(437.57, 617.16) * mm, "end": v(437.6, 618.7) * mm});
            skArc(sketch, "E1173.MirrorCS", {"start": v(428.96, 542.08) * mm, "mid": v(428.04, 542.81) * mm, "end": v(427.7, 543.93) * mm});
            skArc(sketch, "E1174.MirrorCS", {"start": v(436.48, 534.76) * mm, "mid": v(437.57, 533.7) * mm, "end": v(437.6, 532.16) * mm});
            skArc(sketch, "E1175.MirrorCS", {"start": v(427.7, 555.43) * mm, "mid": v(428.28, 556.84) * mm, "end": v(429.7, 557.43) * mm});
            skLineSegment(sketch, "E1176.MirrorCS", {"start": v(437.96, 538.47) * mm, "end": v(428.96, 542.08) * mm});
            skPoint(sketch, "E1177.MirrorP", {"position": v(427.7, 538.27) * mm});
            skArc(sketch, "E1178.MirrorCS", {"start": v(427.7, 535.32) * mm, "mid": v(428.58, 536.97) * mm, "end": v(430.44, 537.17) * mm});
            skPoint(sketch, "E1179.MirrorP", {"position": v(438.34, 534.02) * mm});
            skPoint(sketch, "E1180.MirrorP", {"position": v(427.7, 557.43) * mm});
            skLineSegment(sketch, "E1181.MirrorCS", {"start": v(436.48, 534.76) * mm, "end": v(430.44, 537.17) * mm});
            skLineSegment(sketch, "E1182.MirrorCS", {"start": v(427.7, 555.43) * mm, "end": v(427.7, 543.93) * mm});
            skArc(sketch, "E1183.MirrorCS", {"start": v(440.56, 539.59) * mm, "mid": v(439.5, 538.5) * mm, "end": v(437.96, 538.47) * mm});
            skLineSegment(sketch, "E1184.MirrorCS", {"start": v(440.56, 539.59) * mm, "end": v(446.6, 554.68) * mm});
            skArc(sketch, "E1185.MirrorCS", {"start": v(444.74, 557.43) * mm, "mid": v(446.4, 556.55) * mm, "end": v(446.6, 554.68) * mm});
            skLineSegment(sketch, "E1186.MirrorCS", {"start": v(444.74, 557.43) * mm, "end": v(429.7, 557.43) * mm});
            skLineSegment(sketch, "E1187.MirrorCS", {"start": v(437.6, 532.16) * mm, "end": v(431.56, 517.06) * mm});
            skLineSegment(sketch, "E1188.MirrorCS", {"start": v(427.7, 535.32) * mm, "end": v(427.7, 517.8) * mm});
            skArc(sketch, "E1189.MirrorCS", {"start": v(431.56, 517.06) * mm, "mid": v(429.32, 515.84) * mm, "end": v(427.7, 517.8) * mm});
            skCircle(sketch, "E1190", {"center": v(380.28, 655.43) * mm, "radius": 6 * mm});
            skCircle(sketch, "E1191", {"center": v(380.28, 575.43) * mm, "radius": 6 * mm});
            skCircle(sketch, "E1192", {"center": v(380.28, 503.4) * mm, "radius": 6 * mm});
            skSolve(sketch);
        }
        {
            var Q0;
            Q0 = qSketchRegion(id + "F2", true);
            extrude(context, id + "F3", {"entities" : qUnion([Q0]), "depth" : 3 * mm});
        }
        {
            var Q0;
            Q0=makeQuery(id+"F1.opExtrude","SWEPT_FACE",FACE,{"disambiguationData":[OSD([sQuery(id+"F0.wireOp",EDGE,"E184")])]});
            var sketch = newSketch(context, id + "F4", { "sketchPlane" : qUnion([Q0])});
            skLineSegment(sketch, "E1193", {"start": v(-77.08, 0) * mm, "end": v(-77.08, 3) * mm});
            skLineSegment(sketch, "E1194", {"start": v(-77.08, 3) * mm, "end": v(-58.08, 3) * mm});
            skLineSegment(sketch, "E1195", {"start": v(-77.08, 0) * mm, "end": v(-86.08, 0) * mm});
            skLineSegment(sketch, "E1196", {"start": v(-86.08, 0) * mm, "end": v(-86.08, 3) * mm});
            skLineSegment(sketch, "E1197", {"start": v(-86.08, 3) * mm, "end": v(-108.08, 3) * mm});
            skLineSegment(sketch, "E1198", {"start": v(-108.08, 3) * mm, "end": v(-108.08, 0) * mm});
            skLineSegment(sketch, "E1199", {"start": v(-108.08, 0) * mm, "end": v(-117.08, 0) * mm});
            skLineSegment(sketch, "E1200", {"start": v(-117.08, 0) * mm, "end": v(-117.08, 3) * mm});
            skLineSegment(sketch, "E1201", {"start": v(-117.08, 3) * mm, "end": v(-120.26, 3) * mm});
            skLineSegment(sketch, "E1202", {"start": v(-114.39, 10) * mm, "end": v(-58.08, 10) * mm});
            skLineSegment(sketch, "E1203", {"start": v(-58.08, 10) * mm, "end": v(-54.08, 10) * mm});
            skLineSegment(sketch, "E1204", {"start": v(-54.08, 10) * mm, "end": v(-54.08, 3) * mm});
            skLineSegment(sketch, "E1205", {"start": v(-54.08, 3) * mm, "end": v(-58.08, 3) * mm});
            skArc(sketch, "E1206", {"start": v(-114.39, 10) * mm, "mid": v(-118.6, 7.57) * mm, "end": v(-120.26, 3) * mm});
            skSolve(sketch);
        }
        {
            var Q0;
            Q0 = qSketchRegion(id + "F4", true);
            extrude(context, id + "F5", {"entities" : qUnion([Q0]), "operationType" : NewBodyOperationType.ADD, "depth" : 3 * mm});
        }
        {
            var Q0;
            Q0=qCreatedBy(makeId("Top.planeOp"), FACE);
            var sketch = newSketch(context, id + "F6", { "sketchPlane" : qUnion([Q0]), "disableImprinting" : false});
            skLineSegment(sketch, "E1207", {"start": v(211.4, -179.4) * mm, "end": v(211.4, -221.1) * mm, "construction": true});
            skLineSegment(sketch, "E1208", {"start": v(211.4, -215.1) * mm, "end": v(218.14, -215.1) * mm, "construction": true});
            skCircle(sketch, "E1209", {"center": v(218.14, -215.1) * mm, "radius": 1.28 * mm});
            skLineSegment(sketch, "E1210", {"start": v(211.4, -221.1) * mm, "end": v(215.54, -221.1) * mm});
            skLineSegment(sketch, "E1211", {"start": v(221.54, -215.1) * mm, "end": v(221.54, -210.27) * mm});
            skLineSegment(sketch, "E1212.MirrorCS", {"start": v(211.4, -215.1) * mm, "end": v(204.64, -215.1) * mm, "construction": true});
            skCircle(sketch, "E1213.MirrorC", {"center": v(204.64, -215.1) * mm, "radius": 1.28 * mm});
            skLineSegment(sketch, "E1214.MirrorCS", {"start": v(211.4, -221.1) * mm, "end": v(207.24, -221.1) * mm});
            skLineSegment(sketch, "E1215.MirrorCS", {"start": v(201.24, -215.1) * mm, "end": v(201.24, -210.27) * mm});
            skLineSegment(sketch, "E1216", {"start": v(212.21, -198.1) * mm, "end": v(210.57, -198.1) * mm});
            skCircle(sketch, "E1217", {"center": v(211.4, -205.1) * mm, "radius": 3 * mm});
            skPoint(sketch, "E1218.0.visualSharp", {"position": v(201.24, -198.1) * mm});
            skPoint(sketch, "E1219.0.visualSharp", {"position": v(221.54, -198.1) * mm});
            skPoint(sketch, "E1220.0.visualSharp", {"position": v(201.24, -221.1) * mm});
            skArc(sketch, "E1220.0.filletArc", {"start": v(201.24, -215.1) * mm, "mid": v(203, -219.34) * mm, "end": v(207.24, -221.1) * mm});
            skPoint(sketch, "E1221.0.visualSharp", {"position": v(221.54, -221.1) * mm});
            skArc(sketch, "E1221.0.filletArc", {"start": v(215.54, -221.1) * mm, "mid": v(219.79, -219.34) * mm, "end": v(221.54, -215.1) * mm});
            skLineSegment(sketch, "E1222", {"start": v(206.3, -200.51) * mm, "end": v(201.96, -207.68) * mm});
            skPoint(sketch, "E1218.0.filletArc.end.orphan", {"position": v(201.24, -202.66) * mm});
            skPoint(sketch, "E1223.0.visualSharp", {"position": v(201.24, -208.88) * mm});
            skArc(sketch, "E1223.0.filletArc", {"start": v(201.96, -207.68) * mm, "mid": v(201.43, -208.93) * mm, "end": v(201.24, -210.27) * mm});
            skPoint(sketch, "E1224.0.visualSharp", {"position": v(207.75, -198.1) * mm});
            skArc(sketch, "E1224.0.filletArc", {"start": v(210.57, -198.1) * mm, "mid": v(208.12, -198.74) * mm, "end": v(206.3, -200.51) * mm});
            skArc(sketch, "E1225.MirrorCS", {"start": v(212.21, -198.1) * mm, "mid": v(214.67, -198.74) * mm, "end": v(216.5, -200.51) * mm});
            skLineSegment(sketch, "E1226.MirrorCS", {"start": v(216.5, -200.51) * mm, "end": v(220.82, -207.68) * mm});
            skArc(sketch, "E1227.MirrorCS", {"start": v(220.82, -207.68) * mm, "mid": v(221.36, -208.93) * mm, "end": v(221.54, -210.27) * mm});
            skSolve(sketch);
        }
        {
            var Q0;
            Q0 = qSketchRegion(id + "F6", true);
            extrude(context, id + "F7", {"entities" : qUnion([Q0]), "domain" : OperationDomain.MODEL, "flatOperationType" : FlatOperationType.REMOVE, "thickness1" : 5 * mm, "thickness2" : 0 * mm, "thickness" : 5 * mm, "depth" : 3 * mm, "offsetDistance" : 25 * mm, "startOffsetBound" : StartOffsetType.BLIND, "startOffsetDistance" : 25 * mm});
        }
    });
